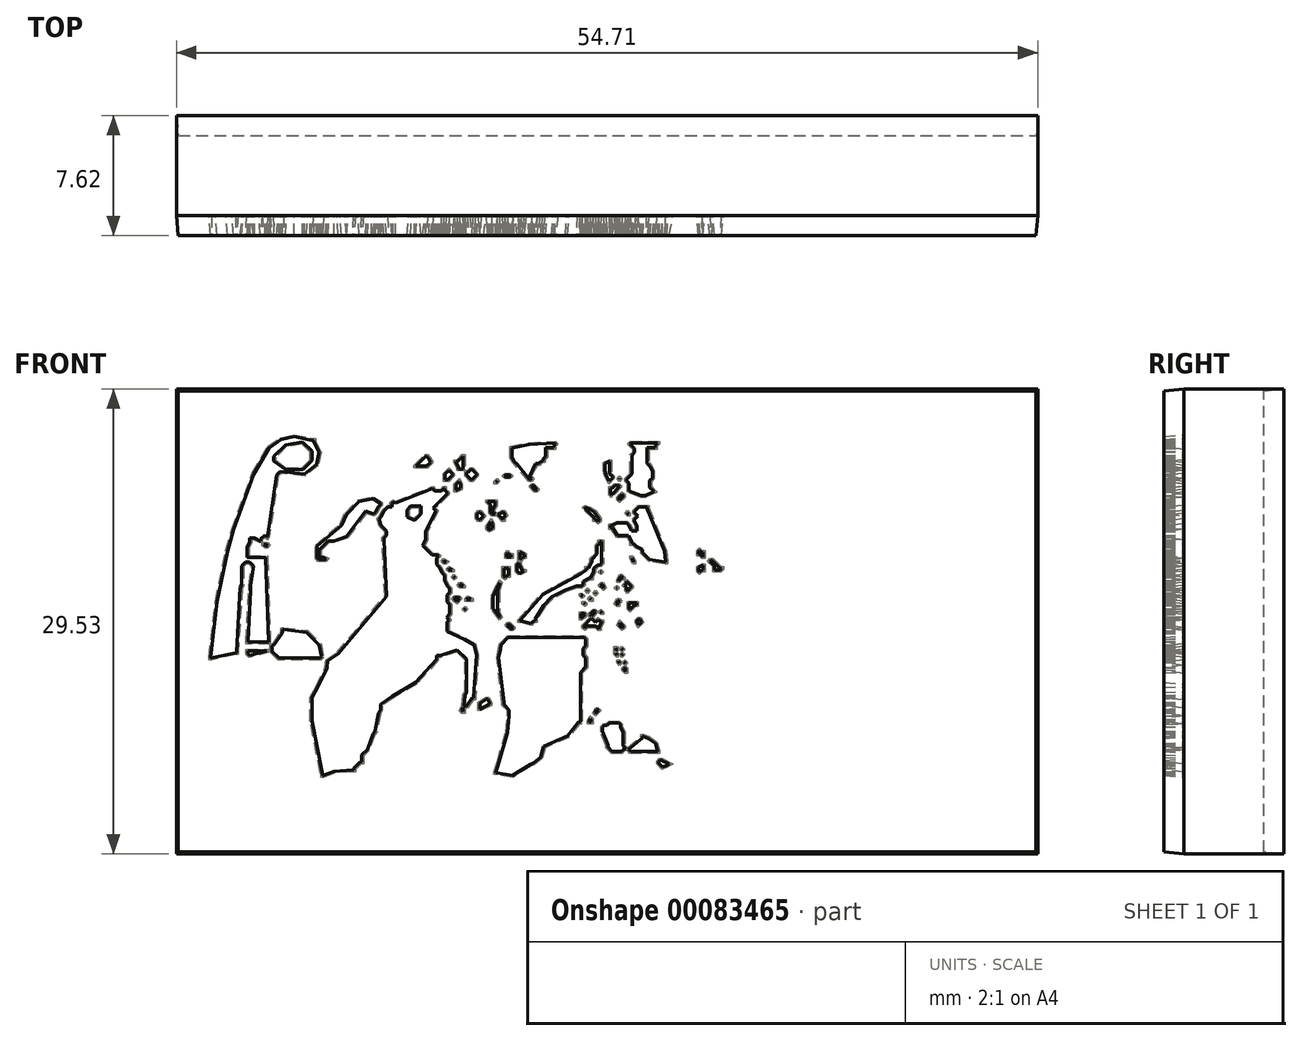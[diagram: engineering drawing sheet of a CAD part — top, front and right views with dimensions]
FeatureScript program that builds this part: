
annotation { "Feature Type Name" : "Feature", "Feature Type Description" : "" }
export const myFeature = defineFeature(function(context is Context, id is Id, definition is map)
    precondition{}
    {
        {
            var Q0;
            Q0=qCreatedBy(makeId("Front.planeOp"),FACE);
            var sketch = newSketch(context, id + "F0", { "sketchPlane" : qUnion([Q0])});
            skLineSegment(sketch, "E0", {"start": v(8.64, 12.87) * mm, "end": v(8.47, 12.87) * mm});
            skLineSegment(sketch, "E1", {"start": v(8.8, 12.87) * mm, "end": v(8.64, 12.87) * mm});
            skLineSegment(sketch, "E2", {"start": v(8.97, 12.87) * mm, "end": v(8.8, 12.87) * mm});
            skLineSegment(sketch, "E3", {"start": v(11, 12.87) * mm, "end": v(10.84, 13.04) * mm});
            skLineSegment(sketch, "E4", {"start": v(10.84, 13.04) * mm, "end": v(9.14, 13.04) * mm});
            skLineSegment(sketch, "E5", {"start": v(9.14, 13.04) * mm, "end": v(8.97, 12.87) * mm});
            skLineSegment(sketch, "E6", {"start": v(11.18, 12.87) * mm, "end": v(11, 12.87) * mm});
            skLineSegment(sketch, "E7", {"start": v(12.53, 12.87) * mm, "end": v(12.36, 12.87) * mm});
            skLineSegment(sketch, "E8", {"start": v(12.7, 12.87) * mm, "end": v(12.53, 12.87) * mm});
            skLineSegment(sketch, "E9", {"start": v(20.32, 12.87) * mm, "end": v(20.15, 12.87) * mm});
            skLineSegment(sketch, "E10", {"start": v(20.49, 12.87) * mm, "end": v(20.32, 12.87) * mm});
            skLineSegment(sketch, "E11", {"start": v(21.5, 12.87) * mm, "end": v(21.34, 13.04) * mm});
            skLineSegment(sketch, "E12", {"start": v(21.34, 13.04) * mm, "end": v(20.83, 13.04) * mm});
            skLineSegment(sketch, "E13", {"start": v(20.83, 13.04) * mm, "end": v(20.49, 12.87) * mm});
            skLineSegment(sketch, "E14", {"start": v(21.67, 12.87) * mm, "end": v(21.5, 12.87) * mm});
            skLineSegment(sketch, "E15", {"start": v(7.11, 12.7) * mm, "end": v(6.94, 12.7) * mm});
            skLineSegment(sketch, "E16", {"start": v(7.28, 12.7) * mm, "end": v(7.11, 12.7) * mm});
            skLineSegment(sketch, "E17", {"start": v(7.45, 12.7) * mm, "end": v(7.28, 12.7) * mm});
            skLineSegment(sketch, "E18", {"start": v(7.79, 12.7) * mm, "end": v(7.62, 12.87) * mm});
            skLineSegment(sketch, "E19", {"start": v(7.62, 12.87) * mm, "end": v(7.45, 12.7) * mm});
            skLineSegment(sketch, "E20", {"start": v(8.13, 12.7) * mm, "end": v(7.79, 12.7) * mm});
            skLineSegment(sketch, "E21", {"start": v(8.3, 12.7) * mm, "end": v(8.13, 12.7) * mm});
            skLineSegment(sketch, "E22", {"start": v(8.3, 12.7) * mm, "end": v(8.47, 12.87) * mm});
            skLineSegment(sketch, "E23", {"start": v(8.64, 12.7) * mm, "end": v(8.64, 12.87) * mm});
            skLineSegment(sketch, "E24", {"start": v(8.97, 12.7) * mm, "end": v(8.97, 12.87) * mm});
            skLineSegment(sketch, "E25", {"start": v(11, 12.7) * mm, "end": v(11, 12.87) * mm});
            skLineSegment(sketch, "E26", {"start": v(11.51, 12.7) * mm, "end": v(11.18, 12.87) * mm});
            skLineSegment(sketch, "E27", {"start": v(11.68, 12.7) * mm, "end": v(11.51, 12.7) * mm});
            skLineSegment(sketch, "E28", {"start": v(11.68, 12.7) * mm, "end": v(11.85, 12.87) * mm});
            skLineSegment(sketch, "E29", {"start": v(11.85, 12.87) * mm, "end": v(12.36, 12.87) * mm});
            skLineSegment(sketch, "E30", {"start": v(12.53, 12.7) * mm, "end": v(12.53, 12.87) * mm});
            skLineSegment(sketch, "E31", {"start": v(12.7, 12.87) * mm, "end": v(13.89, 12.7) * mm});
            skLineSegment(sketch, "E32", {"start": v(13.89, 12.7) * mm, "end": v(15.58, 12.79) * mm});
            skLineSegment(sketch, "E33", {"start": v(15.58, 12.79) * mm, "end": v(20.15, 12.87) * mm});
            skLineSegment(sketch, "E34", {"start": v(20.32, 12.7) * mm, "end": v(20.32, 12.87) * mm});
            skLineSegment(sketch, "E35", {"start": v(21.5, 12.7) * mm, "end": v(21.5, 12.87) * mm});
            skLineSegment(sketch, "E36", {"start": v(-18.8, 12.53) * mm, "end": v(-18.97, 12.53) * mm});
            skLineSegment(sketch, "E37", {"start": v(-18.63, 12.53) * mm, "end": v(-18.8, 12.53) * mm});
            skLineSegment(sketch, "E38", {"start": v(-0.5, 12.53) * mm, "end": v(-0.68, 12.7) * mm});
            skLineSegment(sketch, "E39", {"start": v(-0.68, 12.7) * mm, "end": v(-1.02, 12.53) * mm});
            skLineSegment(sketch, "E40", {"start": v(7.11, 12.53) * mm, "end": v(7.11, 12.7) * mm});
            skLineSegment(sketch, "E41", {"start": v(7.62, 12.53) * mm, "end": v(7.45, 12.7) * mm});
            skLineSegment(sketch, "E42", {"start": v(7.62, 12.53) * mm, "end": v(7.79, 12.7) * mm});
            skLineSegment(sketch, "E43", {"start": v(8.3, 12.53) * mm, "end": v(8.3, 12.7) * mm});
            skLineSegment(sketch, "E44", {"start": v(8.47, 12.53) * mm, "end": v(8.3, 12.53) * mm});
            skLineSegment(sketch, "E45", {"start": v(8.64, 12.53) * mm, "end": v(8.47, 12.53) * mm});
            skLineSegment(sketch, "E46", {"start": v(8.64, 12.53) * mm, "end": v(8.64, 12.7) * mm});
            skLineSegment(sketch, "E47", {"start": v(9.14, 12.53) * mm, "end": v(8.97, 12.7) * mm});
            skLineSegment(sketch, "E48", {"start": v(9.31, 12.53) * mm, "end": v(9.14, 12.53) * mm});
            skLineSegment(sketch, "E49", {"start": v(21.5, 12.53) * mm, "end": v(21.34, 12.53) * mm});
            skLineSegment(sketch, "E50", {"start": v(21.5, 12.53) * mm, "end": v(21.5, 12.7) * mm});
            skLineSegment(sketch, "E51", {"start": v(-18.8, 12.36) * mm, "end": v(-18.8, 12.53) * mm});
            skLineSegment(sketch, "E52", {"start": v(-0.85, 12.36) * mm, "end": v(-1.02, 12.53) * mm});
            skLineSegment(sketch, "E53", {"start": v(-0.68, 12.36) * mm, "end": v(-0.85, 12.36) * mm});
            skLineSegment(sketch, "E54", {"start": v(-0.68, 12.36) * mm, "end": v(-0.5, 12.53) * mm});
            skLineSegment(sketch, "E55", {"start": v(0.85, 12.36) * mm, "end": v(0.68, 12.53) * mm});
            skLineSegment(sketch, "E56", {"start": v(0.68, 12.53) * mm, "end": v(-0.5, 12.53) * mm});
            skLineSegment(sketch, "E57", {"start": v(3.05, 12.36) * mm, "end": v(2.88, 12.36) * mm});
            skLineSegment(sketch, "E58", {"start": v(3.22, 12.36) * mm, "end": v(3.05, 12.36) * mm});
            skLineSegment(sketch, "E59", {"start": v(3.22, 12.36) * mm, "end": v(6.94, 12.7) * mm});
            skLineSegment(sketch, "E60", {"start": v(6.94, 12.36) * mm, "end": v(7.11, 12.53) * mm});
            skLineSegment(sketch, "E61", {"start": v(7.28, 12.36) * mm, "end": v(7.11, 12.53) * mm});
            skLineSegment(sketch, "E62", {"start": v(7.28, 12.36) * mm, "end": v(7.62, 12.53) * mm});
            skLineSegment(sketch, "E63", {"start": v(8.64, 12.36) * mm, "end": v(8.64, 12.53) * mm});
            skLineSegment(sketch, "E64", {"start": v(9.14, 12.36) * mm, "end": v(9.14, 12.53) * mm});
            skLineSegment(sketch, "E65", {"start": v(11.35, 12.36) * mm, "end": v(11.51, 12.7) * mm});
            skLineSegment(sketch, "E66", {"start": v(-8.47, 12.2) * mm, "end": v(-8.64, 12.36) * mm});
            skLineSegment(sketch, "E67", {"start": v(-8.64, 12.36) * mm, "end": v(-10.5, 12.36) * mm});
            skLineSegment(sketch, "E68", {"start": v(-10.5, 12.36) * mm, "end": v(-10.67, 12.2) * mm});
            skLineSegment(sketch, "E69", {"start": v(-10.67, 12.2) * mm, "end": v(-15.92, 12.2) * mm});
            skLineSegment(sketch, "E70", {"start": v(-15.92, 12.2) * mm, "end": v(-16.77, 12.45) * mm});
            skLineSegment(sketch, "E71", {"start": v(-16.77, 12.45) * mm, "end": v(-18.63, 12.53) * mm});
            skLineSegment(sketch, "E72", {"start": v(-8.3, 12.2) * mm, "end": v(-8.47, 12.2) * mm});
            skLineSegment(sketch, "E73", {"start": v(-8.13, 12.2) * mm, "end": v(-8.3, 12.2) * mm});
            skLineSegment(sketch, "E74", {"start": v(-7.96, 12.2) * mm, "end": v(-8.13, 12.2) * mm});
            skLineSegment(sketch, "E75", {"start": v(-7.45, 12.2) * mm, "end": v(-7.96, 12.2) * mm});
            skLineSegment(sketch, "E76", {"start": v(-7.28, 12.2) * mm, "end": v(-7.45, 12.2) * mm});
            skLineSegment(sketch, "E77", {"start": v(-7.11, 12.2) * mm, "end": v(-7.28, 12.2) * mm});
            skLineSegment(sketch, "E78", {"start": v(-3.22, 12.2) * mm, "end": v(-3.39, 12.2) * mm});
            skLineSegment(sketch, "E79", {"start": v(-3.22, 12.2) * mm, "end": v(-1.02, 12.53) * mm});
            skLineSegment(sketch, "E80", {"start": v(-0.85, 12.2) * mm, "end": v(-0.85, 12.36) * mm});
            skLineSegment(sketch, "E81", {"start": v(0.85, 12.2) * mm, "end": v(0.85, 12.36) * mm});
            skLineSegment(sketch, "E82", {"start": v(1.02, 12.2) * mm, "end": v(0.85, 12.2) * mm});
            skLineSegment(sketch, "E83", {"start": v(1.02, 12.2) * mm, "end": v(1.19, 12.36) * mm});
            skLineSegment(sketch, "E84", {"start": v(1.19, 12.36) * mm, "end": v(2.88, 12.36) * mm});
            skLineSegment(sketch, "E85", {"start": v(3.05, 12.2) * mm, "end": v(3.05, 12.36) * mm});
            skLineSegment(sketch, "E86", {"start": v(6.77, 12.2) * mm, "end": v(6.94, 12.36) * mm});
            skLineSegment(sketch, "E87", {"start": v(7.11, 12.2) * mm, "end": v(6.94, 12.36) * mm});
            skLineSegment(sketch, "E88", {"start": v(7.11, 12.2) * mm, "end": v(7.28, 12.36) * mm});
            skLineSegment(sketch, "E89", {"start": v(8.13, 12.2) * mm, "end": v(8.3, 12.53) * mm});
            skLineSegment(sketch, "E90", {"start": v(9.65, 12.2) * mm, "end": v(9.82, 12.36) * mm});
            skLineSegment(sketch, "E91", {"start": v(9.82, 12.36) * mm, "end": v(9.65, 12.53) * mm});
            skLineSegment(sketch, "E92", {"start": v(9.65, 12.53) * mm, "end": v(9.31, 12.53) * mm});
            skLineSegment(sketch, "E93", {"start": v(11.18, 12.2) * mm, "end": v(11, 12.36) * mm});
            skLineSegment(sketch, "E94", {"start": v(11, 12.36) * mm, "end": v(11, 12.7) * mm});
            skLineSegment(sketch, "E95", {"start": v(11.35, 12.2) * mm, "end": v(11.18, 12.2) * mm});
            skLineSegment(sketch, "E96", {"start": v(11.35, 12.2) * mm, "end": v(11.35, 12.36) * mm});
            skLineSegment(sketch, "E97", {"start": v(12.02, 12.2) * mm, "end": v(12.02, 12.36) * mm});
            skLineSegment(sketch, "E98", {"start": v(12.02, 12.36) * mm, "end": v(11.68, 12.7) * mm});
            skLineSegment(sketch, "E99", {"start": v(-8.64, 12.02) * mm, "end": v(-8.47, 12.2) * mm});
            skLineSegment(sketch, "E100", {"start": v(-8.13, 12.02) * mm, "end": v(-8.13, 12.2) * mm});
            skLineSegment(sketch, "E101", {"start": v(-7.28, 12.02) * mm, "end": v(-7.28, 12.2) * mm});
            skLineSegment(sketch, "E102", {"start": v(-6.94, 12.02) * mm, "end": v(-7.11, 12.2) * mm});
            skLineSegment(sketch, "E103", {"start": v(-6.77, 12.02) * mm, "end": v(-6.94, 12.02) * mm});
            skLineSegment(sketch, "E104", {"start": v(-6.6, 12.02) * mm, "end": v(-6.77, 12.02) * mm});
            skLineSegment(sketch, "E105", {"start": v(-6.43, 12.02) * mm, "end": v(-6.6, 12.02) * mm});
            skLineSegment(sketch, "E106", {"start": v(-6.43, 12.02) * mm, "end": v(-5.26, 12.26) * mm});
            skLineSegment(sketch, "E107", {"start": v(-5.26, 12.26) * mm, "end": v(-3.56, 12.36) * mm});
            skLineSegment(sketch, "E108", {"start": v(-3.56, 12.36) * mm, "end": v(-3.39, 12.2) * mm});
            skLineSegment(sketch, "E109", {"start": v(-3.56, 12.02) * mm, "end": v(-3.39, 12.2) * mm});
            skLineSegment(sketch, "E110", {"start": v(-3.22, 12.02) * mm, "end": v(-3.22, 12.2) * mm});
            skLineSegment(sketch, "E111", {"start": v(2.88, 12.02) * mm, "end": v(3.05, 12.2) * mm});
            skLineSegment(sketch, "E112", {"start": v(3.22, 12.02) * mm, "end": v(3.05, 12.2) * mm});
            skLineSegment(sketch, "E113", {"start": v(6.77, 12.02) * mm, "end": v(6.77, 12.2) * mm});
            skLineSegment(sketch, "E114", {"start": v(6.94, 12.02) * mm, "end": v(6.77, 12.02) * mm});
            skLineSegment(sketch, "E115", {"start": v(6.94, 12.02) * mm, "end": v(7.11, 12.2) * mm});
            skLineSegment(sketch, "E116", {"start": v(8.13, 12.02) * mm, "end": v(7.96, 12.02) * mm});
            skLineSegment(sketch, "E117", {"start": v(8.13, 12.02) * mm, "end": v(8.13, 12.2) * mm});
            skLineSegment(sketch, "E118", {"start": v(8.64, 12.02) * mm, "end": v(8.64, 12.36) * mm});
            skLineSegment(sketch, "E119", {"start": v(9.14, 12.02) * mm, "end": v(9.14, 12.36) * mm});
            skLineSegment(sketch, "E120", {"start": v(9.65, 12.02) * mm, "end": v(9.48, 12.02) * mm});
            skLineSegment(sketch, "E121", {"start": v(9.65, 12.02) * mm, "end": v(9.65, 12.2) * mm});
            skLineSegment(sketch, "E122", {"start": v(9.82, 12.02) * mm, "end": v(9.65, 12.02) * mm});
            skLineSegment(sketch, "E123", {"start": v(11.35, 12.2) * mm, "end": v(11.51, 12.02) * mm});
            skLineSegment(sketch, "E124", {"start": v(11.51, 12.02) * mm, "end": v(11.85, 12.02) * mm});
            skLineSegment(sketch, "E125", {"start": v(11.85, 12.02) * mm, "end": v(12.02, 12.2) * mm});
            skLineSegment(sketch, "E126", {"start": v(-8.8, 11.85) * mm, "end": v(-8.64, 12.02) * mm});
            skLineSegment(sketch, "E127", {"start": v(-8.47, 11.85) * mm, "end": v(-8.64, 12.02) * mm});
            skLineSegment(sketch, "E128", {"start": v(-8.47, 11.85) * mm, "end": v(-8.13, 12.02) * mm});
            skLineSegment(sketch, "E129", {"start": v(-7.28, 12.02) * mm, "end": v(-7.11, 11.85) * mm});
            skLineSegment(sketch, "E130", {"start": v(-7.11, 11.85) * mm, "end": v(-6.94, 12.02) * mm});
            skLineSegment(sketch, "E131", {"start": v(-6.77, 11.85) * mm, "end": v(-6.77, 12.02) * mm});
            skLineSegment(sketch, "E132", {"start": v(-6.43, 11.85) * mm, "end": v(-6.43, 12.02) * mm});
            skLineSegment(sketch, "E133", {"start": v(-3.73, 11.85) * mm, "end": v(-3.9, 11.85) * mm});
            skLineSegment(sketch, "E134", {"start": v(-3.56, 11.85) * mm, "end": v(-3.73, 11.85) * mm});
            skLineSegment(sketch, "E135", {"start": v(-3.56, 11.85) * mm, "end": v(-3.56, 12.02) * mm});
            skLineSegment(sketch, "E136", {"start": v(-3.22, 11.85) * mm, "end": v(-3.22, 12.02) * mm});
            skLineSegment(sketch, "E137", {"start": v(-3.05, 11.85) * mm, "end": v(-3.22, 11.85) * mm});
            skLineSegment(sketch, "E138", {"start": v(2.7, 11.85) * mm, "end": v(2.54, 11.85) * mm});
            skLineSegment(sketch, "E139", {"start": v(2.88, 11.85) * mm, "end": v(2.7, 11.85) * mm});
            skLineSegment(sketch, "E140", {"start": v(2.88, 11.85) * mm, "end": v(2.88, 12.02) * mm});
            skLineSegment(sketch, "E141", {"start": v(3.22, 11.85) * mm, "end": v(3.22, 12.02) * mm});
            skLineSegment(sketch, "E142", {"start": v(3.39, 11.85) * mm, "end": v(3.22, 11.85) * mm});
            skLineSegment(sketch, "E143", {"start": v(8.64, 11.85) * mm, "end": v(8.64, 12.02) * mm});
            skLineSegment(sketch, "E144", {"start": v(8.8, 11.85) * mm, "end": v(8.64, 11.85) * mm});
            skLineSegment(sketch, "E145", {"start": v(8.97, 11.85) * mm, "end": v(8.8, 11.85) * mm});
            skLineSegment(sketch, "E146", {"start": v(9.14, 11.85) * mm, "end": v(8.97, 11.85) * mm});
            skLineSegment(sketch, "E147", {"start": v(9.14, 11.85) * mm, "end": v(9.14, 12.02) * mm});
            skLineSegment(sketch, "E148", {"start": v(9.31, 11.85) * mm, "end": v(9.14, 11.85) * mm});
            skLineSegment(sketch, "E149", {"start": v(9.31, 11.85) * mm, "end": v(9.48, 12.02) * mm});
            skLineSegment(sketch, "E150", {"start": v(-8.97, 11.68) * mm, "end": v(-8.8, 11.85) * mm});
            skLineSegment(sketch, "E151", {"start": v(-8.64, 11.68) * mm, "end": v(-8.8, 11.85) * mm});
            skLineSegment(sketch, "E152", {"start": v(-8.64, 11.68) * mm, "end": v(-8.47, 11.85) * mm});
            skLineSegment(sketch, "E153", {"start": v(-4.06, 11.68) * mm, "end": v(-4.06, 11.85) * mm});
            skLineSegment(sketch, "E154", {"start": v(-4.06, 11.85) * mm, "end": v(-3.9, 11.85) * mm});
            skLineSegment(sketch, "E155", {"start": v(-3.56, 11.68) * mm, "end": v(-3.56, 11.85) * mm});
            skLineSegment(sketch, "E156", {"start": v(-3.22, 11.68) * mm, "end": v(-3.22, 11.85) * mm});
            skLineSegment(sketch, "E157", {"start": v(-2.7, 11.68) * mm, "end": v(-2.7, 11.85) * mm});
            skLineSegment(sketch, "E158", {"start": v(-2.7, 11.85) * mm, "end": v(-2.88, 12.02) * mm});
            skLineSegment(sketch, "E159", {"start": v(-2.88, 12.02) * mm, "end": v(-3.05, 11.85) * mm});
            skLineSegment(sketch, "E160", {"start": v(2.37, 11.68) * mm, "end": v(2.37, 11.85) * mm});
            skLineSegment(sketch, "E161", {"start": v(2.37, 11.85) * mm, "end": v(2.54, 11.85) * mm});
            skLineSegment(sketch, "E162", {"start": v(2.88, 11.68) * mm, "end": v(2.88, 11.85) * mm});
            skLineSegment(sketch, "E163", {"start": v(3.22, 11.68) * mm, "end": v(3.22, 11.85) * mm});
            skLineSegment(sketch, "E164", {"start": v(3.73, 11.68) * mm, "end": v(3.73, 11.85) * mm});
            skLineSegment(sketch, "E165", {"start": v(3.73, 11.85) * mm, "end": v(3.56, 12.02) * mm});
            skLineSegment(sketch, "E166", {"start": v(3.56, 12.02) * mm, "end": v(3.39, 11.85) * mm});
            skLineSegment(sketch, "E167", {"start": v(8.47, 11.68) * mm, "end": v(8.13, 12.02) * mm});
            skLineSegment(sketch, "E168", {"start": v(8.47, 11.68) * mm, "end": v(8.64, 11.85) * mm});
            skLineSegment(sketch, "E169", {"start": v(9.14, 11.68) * mm, "end": v(9.14, 11.85) * mm});
            skLineSegment(sketch, "E170", {"start": v(22.52, 11.68) * mm, "end": v(21.5, 12.53) * mm});
            skLineSegment(sketch, "E171", {"start": v(-11.68, 11.51) * mm, "end": v(-11.51, 11.68) * mm});
            skLineSegment(sketch, "E172", {"start": v(-11.35, 11.51) * mm, "end": v(-11.51, 11.68) * mm});
            skLineSegment(sketch, "E173", {"start": v(-9.31, 11.51) * mm, "end": v(-9.48, 11.51) * mm});
            skLineSegment(sketch, "E174", {"start": v(-9.14, 11.51) * mm, "end": v(-9.31, 11.51) * mm});
            skLineSegment(sketch, "E175", {"start": v(-9.14, 11.51) * mm, "end": v(-8.97, 11.68) * mm});
            skLineSegment(sketch, "E176", {"start": v(-8.8, 11.51) * mm, "end": v(-8.97, 11.68) * mm});
            skLineSegment(sketch, "E177", {"start": v(-8.8, 11.51) * mm, "end": v(-8.64, 11.68) * mm});
            skLineSegment(sketch, "E178", {"start": v(-4.06, 11.51) * mm, "end": v(-4.06, 11.68) * mm});
            skLineSegment(sketch, "E179", {"start": v(-3.22, 11.51) * mm, "end": v(-3.22, 11.68) * mm});
            skLineSegment(sketch, "E180", {"start": v(-1.19, 11.51) * mm, "end": v(-0.85, 12.2) * mm});
            skLineSegment(sketch, "E181", {"start": v(1.19, 11.51) * mm, "end": v(1.02, 11.51) * mm});
            skLineSegment(sketch, "E182", {"start": v(1.19, 11.51) * mm, "end": v(1.35, 11.68) * mm});
            skLineSegment(sketch, "E183", {"start": v(1.35, 11.68) * mm, "end": v(1.35, 11.85) * mm});
            skLineSegment(sketch, "E184", {"start": v(1.35, 11.85) * mm, "end": v(1.02, 12.2) * mm});
            skLineSegment(sketch, "E185", {"start": v(2.37, 11.51) * mm, "end": v(2.37, 11.68) * mm});
            skLineSegment(sketch, "E186", {"start": v(2.54, 11.51) * mm, "end": v(2.37, 11.51) * mm});
            skLineSegment(sketch, "E187", {"start": v(2.88, 11.51) * mm, "end": v(2.88, 11.68) * mm});
            skLineSegment(sketch, "E188", {"start": v(3.73, 11.51) * mm, "end": v(3.56, 11.51) * mm});
            skLineSegment(sketch, "E189", {"start": v(3.73, 11.51) * mm, "end": v(3.73, 11.68) * mm});
            skLineSegment(sketch, "E190", {"start": v(6.43, 11.51) * mm, "end": v(6.77, 12.02) * mm});
            skLineSegment(sketch, "E191", {"start": v(8.64, 11.51) * mm, "end": v(8.47, 11.68) * mm});
            skLineSegment(sketch, "E192", {"start": v(8.8, 11.51) * mm, "end": v(8.64, 11.51) * mm});
            skLineSegment(sketch, "E193", {"start": v(9.14, 11.51) * mm, "end": v(9.14, 11.68) * mm});
            skLineSegment(sketch, "E194", {"start": v(9.31, 11.51) * mm, "end": v(9.14, 11.51) * mm});
            skLineSegment(sketch, "E195", {"start": v(9.48, 11.51) * mm, "end": v(9.31, 11.51) * mm});
            skLineSegment(sketch, "E196", {"start": v(9.65, 11.51) * mm, "end": v(9.48, 11.51) * mm});
            skLineSegment(sketch, "E197", {"start": v(9.82, 11.51) * mm, "end": v(9.65, 11.51) * mm});
            skLineSegment(sketch, "E198", {"start": v(9.82, 11.51) * mm, "end": v(10, 11.51) * mm});
            skLineSegment(sketch, "E199", {"start": v(10, 11.51) * mm, "end": v(10.16, 11.68) * mm});
            skLineSegment(sketch, "E200", {"start": v(10.16, 11.68) * mm, "end": v(9.82, 12.02) * mm});
            skLineSegment(sketch, "E201", {"start": v(22.52, 11.51) * mm, "end": v(22.52, 11.68) * mm});
            skLineSegment(sketch, "E202", {"start": v(22.7, 11.51) * mm, "end": v(22.52, 11.51) * mm});
            skLineSegment(sketch, "E203", {"start": v(-11.51, 11.35) * mm, "end": v(-11.68, 11.51) * mm});
            skLineSegment(sketch, "E204", {"start": v(-11.51, 11.35) * mm, "end": v(-11.35, 11.51) * mm});
            skLineSegment(sketch, "E205", {"start": v(-9.31, 11.35) * mm, "end": v(-9.31, 11.51) * mm});
            skLineSegment(sketch, "E206", {"start": v(-8.97, 11.35) * mm, "end": v(-9.14, 11.51) * mm});
            skLineSegment(sketch, "E207", {"start": v(-8.8, 11.35) * mm, "end": v(-8.97, 11.35) * mm});
            skLineSegment(sketch, "E208", {"start": v(-8.8, 11.35) * mm, "end": v(-8.8, 11.51) * mm});
            skLineSegment(sketch, "E209", {"start": v(-6.43, 11.35) * mm, "end": v(-6.43, 11.85) * mm});
            skLineSegment(sketch, "E210", {"start": v(-4.06, 11.35) * mm, "end": v(-4.06, 11.51) * mm});
            skLineSegment(sketch, "E211", {"start": v(-3.9, 11.35) * mm, "end": v(-4.06, 11.35) * mm});
            skLineSegment(sketch, "E212", {"start": v(-3.56, 11.35) * mm, "end": v(-3.56, 11.68) * mm});
            skLineSegment(sketch, "E213", {"start": v(-3.22, 11.35) * mm, "end": v(-3.22, 11.51) * mm});
            skLineSegment(sketch, "E214", {"start": v(-3.05, 11.35) * mm, "end": v(-3.22, 11.35) * mm});
            skLineSegment(sketch, "E215", {"start": v(-3.05, 11.35) * mm, "end": v(-2.7, 11.68) * mm});
            skLineSegment(sketch, "E216", {"start": v(-1.19, 11.35) * mm, "end": v(-1.19, 11.51) * mm});
            skLineSegment(sketch, "E217", {"start": v(-1.02, 11.35) * mm, "end": v(-1.19, 11.35) * mm});
            skLineSegment(sketch, "E218", {"start": v(-1.02, 11.35) * mm, "end": v(0.85, 12.2) * mm});
            skLineSegment(sketch, "E219", {"start": v(0.17, 11.35) * mm, "end": v(0.34, 11.51) * mm});
            skLineSegment(sketch, "E220", {"start": v(0.34, 11.51) * mm, "end": v(1.02, 11.51) * mm});
            skLineSegment(sketch, "E221", {"start": v(1.19, 11.35) * mm, "end": v(1.19, 11.51) * mm});
            skLineSegment(sketch, "E222", {"start": v(2.37, 11.35) * mm, "end": v(2.37, 11.51) * mm});
            skLineSegment(sketch, "E223", {"start": v(2.7, 11.35) * mm, "end": v(2.54, 11.51) * mm});
            skLineSegment(sketch, "E224", {"start": v(2.88, 11.35) * mm, "end": v(2.7, 11.35) * mm});
            skLineSegment(sketch, "E225", {"start": v(2.88, 11.35) * mm, "end": v(2.88, 11.51) * mm});
            skLineSegment(sketch, "E226", {"start": v(3.39, 11.35) * mm, "end": v(3.22, 11.68) * mm});
            skLineSegment(sketch, "E227", {"start": v(3.39, 11.35) * mm, "end": v(3.56, 11.51) * mm});
            skLineSegment(sketch, "E228", {"start": v(6.43, 11.35) * mm, "end": v(6.27, 11.35) * mm});
            skLineSegment(sketch, "E229", {"start": v(6.43, 11.35) * mm, "end": v(6.43, 11.51) * mm});
            skLineSegment(sketch, "E230", {"start": v(7.96, 11.35) * mm, "end": v(7.62, 11.68) * mm});
            skLineSegment(sketch, "E231", {"start": v(7.62, 11.68) * mm, "end": v(7.96, 12.02) * mm});
            skLineSegment(sketch, "E232", {"start": v(8.13, 11.35) * mm, "end": v(7.96, 11.35) * mm});
            skLineSegment(sketch, "E233", {"start": v(8.13, 11.35) * mm, "end": v(8.47, 11.68) * mm});
            skLineSegment(sketch, "E234", {"start": v(8.64, 11.35) * mm, "end": v(8.64, 11.51) * mm});
            skLineSegment(sketch, "E235", {"start": v(8.97, 11.35) * mm, "end": v(8.8, 11.51) * mm});
            skLineSegment(sketch, "E236", {"start": v(8.97, 11.35) * mm, "end": v(9.14, 11.51) * mm});
            skLineSegment(sketch, "E237", {"start": v(9.65, 11.35) * mm, "end": v(9.65, 11.51) * mm});
            skLineSegment(sketch, "E238", {"start": v(-10, 11.18) * mm, "end": v(-10.16, 11.18) * mm});
            skLineSegment(sketch, "E239", {"start": v(-9.82, 11.18) * mm, "end": v(-10, 11.18) * mm});
            skLineSegment(sketch, "E240", {"start": v(-9.82, 11.18) * mm, "end": v(-9.48, 11.51) * mm});
            skLineSegment(sketch, "E241", {"start": v(-9.31, 11.18) * mm, "end": v(-9.31, 11.35) * mm});
            skLineSegment(sketch, "E242", {"start": v(-9.14, 11.18) * mm, "end": v(-9.31, 11.18) * mm});
            skLineSegment(sketch, "E243", {"start": v(-9.14, 11.18) * mm, "end": v(-8.97, 11.35) * mm});
            skLineSegment(sketch, "E244", {"start": v(-8.8, 11.18) * mm, "end": v(-8.8, 11.35) * mm});
            skLineSegment(sketch, "E245", {"start": v(-6.6, 11.18) * mm, "end": v(-6.77, 11.35) * mm});
            skLineSegment(sketch, "E246", {"start": v(-6.77, 11.35) * mm, "end": v(-6.77, 11.85) * mm});
            skLineSegment(sketch, "E247", {"start": v(-6.6, 11.18) * mm, "end": v(-6.43, 11.35) * mm});
            skLineSegment(sketch, "E248", {"start": v(-4.23, 11.18) * mm, "end": v(-4.06, 11.35) * mm});
            skLineSegment(sketch, "E249", {"start": v(-3.73, 11.18) * mm, "end": v(-3.9, 11.35) * mm});
            skLineSegment(sketch, "E250", {"start": v(-3.73, 11.18) * mm, "end": v(-3.56, 11.35) * mm});
            skLineSegment(sketch, "E251", {"start": v(-3.39, 11.18) * mm, "end": v(-3.56, 11.35) * mm});
            skLineSegment(sketch, "E252", {"start": v(-3.39, 11.18) * mm, "end": v(-3.22, 11.35) * mm});
            skLineSegment(sketch, "E253", {"start": v(-1.19, 11.18) * mm, "end": v(-1.19, 11.35) * mm});
            skLineSegment(sketch, "E254", {"start": v(0, 11.18) * mm, "end": v(-0.17, 11.18) * mm});
            skLineSegment(sketch, "E255", {"start": v(0, 11.18) * mm, "end": v(0.17, 11.35) * mm});
            skLineSegment(sketch, "E256", {"start": v(1.19, 11.18) * mm, "end": v(1.19, 11.35) * mm});
            skLineSegment(sketch, "E257", {"start": v(3.05, 11.18) * mm, "end": v(2.88, 11.35) * mm});
            skLineSegment(sketch, "E258", {"start": v(3.39, 11.18) * mm, "end": v(3.39, 11.35) * mm});
            skLineSegment(sketch, "E259", {"start": v(6.43, 11.18) * mm, "end": v(6.43, 11.35) * mm});
            skLineSegment(sketch, "E260", {"start": v(7.96, 11.18) * mm, "end": v(7.96, 11.35) * mm});
            skLineSegment(sketch, "E261", {"start": v(-11.35, 11) * mm, "end": v(-11.51, 11.35) * mm});
            skLineSegment(sketch, "E262", {"start": v(-11.35, 11) * mm, "end": v(-11.18, 11.18) * mm});
            skLineSegment(sketch, "E263", {"start": v(-11.18, 11.18) * mm, "end": v(-11.35, 11.51) * mm});
            skLineSegment(sketch, "E264", {"start": v(-10.33, 11) * mm, "end": v(-10.33, 11.18) * mm});
            skLineSegment(sketch, "E265", {"start": v(-10.33, 11.18) * mm, "end": v(-10.16, 11.18) * mm});
            skLineSegment(sketch, "E266", {"start": v(-10, 11) * mm, "end": v(-10, 11.18) * mm});
            skLineSegment(sketch, "E267", {"start": v(-9.31, 11) * mm, "end": v(-9.31, 11.18) * mm});
            skLineSegment(sketch, "E268", {"start": v(-6.27, 11) * mm, "end": v(-6.43, 11.35) * mm});
            skLineSegment(sketch, "E269", {"start": v(-4.23, 11) * mm, "end": v(-4.4, 11) * mm});
            skLineSegment(sketch, "E270", {"start": v(-4.23, 11) * mm, "end": v(-4.23, 11.18) * mm});
            skLineSegment(sketch, "E271", {"start": v(-3.9, 11) * mm, "end": v(-3.73, 11.18) * mm});
            skLineSegment(sketch, "E272", {"start": v(-3.39, 11) * mm, "end": v(-3.39, 11.18) * mm});
            skLineSegment(sketch, "E273", {"start": v(-2.7, 11) * mm, "end": v(-3.05, 11.35) * mm});
            skLineSegment(sketch, "E274", {"start": v(-2.54, 11) * mm, "end": v(-2.7, 11) * mm});
            skLineSegment(sketch, "E275", {"start": v(-2.54, 11) * mm, "end": v(-2.37, 11.18) * mm});
            skLineSegment(sketch, "E276", {"start": v(-2.37, 11.18) * mm, "end": v(-2.37, 11.35) * mm});
            skLineSegment(sketch, "E277", {"start": v(-2.37, 11.35) * mm, "end": v(-2.7, 11.68) * mm});
            skLineSegment(sketch, "E278", {"start": v(-0.5, 11) * mm, "end": v(-0.68, 11) * mm});
            skLineSegment(sketch, "E279", {"start": v(-0.5, 11) * mm, "end": v(-0.17, 11.18) * mm});
            skLineSegment(sketch, "E280", {"start": v(0, 11) * mm, "end": v(0, 11.18) * mm});
            skLineSegment(sketch, "E281", {"start": v(0.34, 11) * mm, "end": v(0.17, 11.35) * mm});
            skLineSegment(sketch, "E282", {"start": v(1.19, 11) * mm, "end": v(1.02, 11) * mm});
            skLineSegment(sketch, "E283", {"start": v(1.19, 11) * mm, "end": v(1.19, 11.18) * mm});
            skLineSegment(sketch, "E284", {"start": v(2.88, 11) * mm, "end": v(2.7, 11) * mm});
            skLineSegment(sketch, "E285", {"start": v(2.88, 11) * mm, "end": v(3.05, 11.18) * mm});
            skLineSegment(sketch, "E286", {"start": v(3.22, 11) * mm, "end": v(3.05, 11.18) * mm});
            skLineSegment(sketch, "E287", {"start": v(3.22, 11) * mm, "end": v(3.39, 11.18) * mm});
            skLineSegment(sketch, "E288", {"start": v(3.56, 11) * mm, "end": v(3.39, 11.18) * mm});
            skLineSegment(sketch, "E289", {"start": v(3.56, 11) * mm, "end": v(3.9, 11.35) * mm});
            skLineSegment(sketch, "E290", {"start": v(3.9, 11.35) * mm, "end": v(3.73, 11.51) * mm});
            skLineSegment(sketch, "E291", {"start": v(6.1, 11) * mm, "end": v(6.27, 11.35) * mm});
            skLineSegment(sketch, "E292", {"start": v(7.96, 11) * mm, "end": v(7.96, 11.18) * mm});
            skLineSegment(sketch, "E293", {"start": v(8.64, 11) * mm, "end": v(8.64, 11.35) * mm});
            skLineSegment(sketch, "E294", {"start": v(9.14, 11) * mm, "end": v(8.97, 11.35) * mm});
            skLineSegment(sketch, "E295", {"start": v(9.82, 11) * mm, "end": v(9.65, 11.35) * mm});
            skLineSegment(sketch, "E296", {"start": v(13.38, 11) * mm, "end": v(13.38, 11.35) * mm});
            skLineSegment(sketch, "E297", {"start": v(13.38, 11.35) * mm, "end": v(13.04, 11.68) * mm});
            skLineSegment(sketch, "E298", {"start": v(13.04, 11.68) * mm, "end": v(12.36, 11.68) * mm});
            skLineSegment(sketch, "E299", {"start": v(12.36, 11.68) * mm, "end": v(12.02, 12.2) * mm});
            skLineSegment(sketch, "E300", {"start": v(21.34, 12.53) * mm, "end": v(21, 12.53) * mm});
            skLineSegment(sketch, "E301", {"start": v(21, 12.53) * mm, "end": v(20.62, 12.04) * mm});
            skLineSegment(sketch, "E302", {"start": v(20.62, 12.04) * mm, "end": v(20.49, 11.85) * mm});
            skLineSegment(sketch, "E303", {"start": v(20.49, 11.85) * mm, "end": v(20.66, 11.35) * mm});
            skLineSegment(sketch, "E304", {"start": v(20.66, 11.35) * mm, "end": v(21, 11) * mm});
            skLineSegment(sketch, "E305", {"start": v(21, 11) * mm, "end": v(21.84, 11) * mm});
            skLineSegment(sketch, "E306", {"start": v(21.84, 11) * mm, "end": v(22.34, 11.38) * mm});
            skLineSegment(sketch, "E307", {"start": v(22.34, 11.38) * mm, "end": v(22.52, 11.51) * mm});
            skLineSegment(sketch, "E308", {"start": v(-12.53, 10.84) * mm, "end": v(-11.85, 11.51) * mm});
            skLineSegment(sketch, "E309", {"start": v(-11.85, 11.51) * mm, "end": v(-11.68, 11.51) * mm});
            skLineSegment(sketch, "E310", {"start": v(-8.8, 10.84) * mm, "end": v(-8.8, 11.18) * mm});
            skLineSegment(sketch, "E311", {"start": v(-6.43, 10.84) * mm, "end": v(-6.6, 11.18) * mm});
            skLineSegment(sketch, "E312", {"start": v(-6.43, 10.84) * mm, "end": v(-6.27, 11) * mm});
            skLineSegment(sketch, "E313", {"start": v(-6.1, 10.84) * mm, "end": v(-6.27, 11) * mm});
            skLineSegment(sketch, "E314", {"start": v(-4.57, 10.84) * mm, "end": v(-4.74, 10.84) * mm});
            skLineSegment(sketch, "E315", {"start": v(-4.57, 10.84) * mm, "end": v(-4.4, 11) * mm});
            skLineSegment(sketch, "E316", {"start": v(-4.06, 10.84) * mm, "end": v(-4.23, 11) * mm});
            skLineSegment(sketch, "E317", {"start": v(-4.06, 10.84) * mm, "end": v(-3.9, 11) * mm});
            skLineSegment(sketch, "E318", {"start": v(-3.73, 10.84) * mm, "end": v(-3.9, 11) * mm});
            skLineSegment(sketch, "E319", {"start": v(-3.56, 10.84) * mm, "end": v(-3.73, 10.84) * mm});
            skLineSegment(sketch, "E320", {"start": v(-3.56, 10.84) * mm, "end": v(-3.39, 11) * mm});
            skLineSegment(sketch, "E321", {"start": v(-2.54, 10.84) * mm, "end": v(-2.54, 11) * mm});
            skLineSegment(sketch, "E322", {"start": v(-1.19, 10.84) * mm, "end": v(-1.19, 11.18) * mm});
            skLineSegment(sketch, "E323", {"start": v(-0.85, 10.84) * mm, "end": v(-0.68, 11) * mm});
            skLineSegment(sketch, "E324", {"start": v(-0.5, 10.84) * mm, "end": v(-0.5, 11) * mm});
            skLineSegment(sketch, "E325", {"start": v(0, 10.84) * mm, "end": v(0, 11) * mm});
            skLineSegment(sketch, "E326", {"start": v(0.17, 10.84) * mm, "end": v(0, 10.84) * mm});
            skLineSegment(sketch, "E327", {"start": v(0.34, 10.84) * mm, "end": v(0.17, 10.84) * mm});
            skLineSegment(sketch, "E328", {"start": v(0.34, 10.84) * mm, "end": v(0.34, 11) * mm});
            skLineSegment(sketch, "E329", {"start": v(0.5, 10.84) * mm, "end": v(0.34, 10.84) * mm});
            skLineSegment(sketch, "E330", {"start": v(0.5, 10.84) * mm, "end": v(1.02, 11) * mm});
            skLineSegment(sketch, "E331", {"start": v(1.19, 10.84) * mm, "end": v(1.19, 11) * mm});
            skLineSegment(sketch, "E332", {"start": v(2.54, 10.84) * mm, "end": v(2.37, 11) * mm});
            skLineSegment(sketch, "E333", {"start": v(2.37, 11) * mm, "end": v(2.37, 11.35) * mm});
            skLineSegment(sketch, "E334", {"start": v(2.54, 10.84) * mm, "end": v(2.7, 11) * mm});
            skLineSegment(sketch, "E335", {"start": v(2.88, 10.84) * mm, "end": v(2.88, 11) * mm});
            skLineSegment(sketch, "E336", {"start": v(6.27, 10.84) * mm, "end": v(6.1, 11) * mm});
            skLineSegment(sketch, "E337", {"start": v(6.27, 10.84) * mm, "end": v(6.43, 11.18) * mm});
            skLineSegment(sketch, "E338", {"start": v(8.13, 10.84) * mm, "end": v(7.96, 10.84) * mm});
            skLineSegment(sketch, "E339", {"start": v(7.96, 10.84) * mm, "end": v(7.96, 11) * mm});
            skLineSegment(sketch, "E340", {"start": v(8.47, 10.84) * mm, "end": v(8.13, 10.84) * mm});
            skLineSegment(sketch, "E341", {"start": v(8.64, 10.84) * mm, "end": v(8.47, 10.84) * mm});
            skLineSegment(sketch, "E342", {"start": v(8.64, 10.84) * mm, "end": v(8.64, 11) * mm});
            skLineSegment(sketch, "E343", {"start": v(9.14, 10.84) * mm, "end": v(9.14, 11) * mm});
            skLineSegment(sketch, "E344", {"start": v(9.31, 10.84) * mm, "end": v(9.14, 10.84) * mm});
            skLineSegment(sketch, "E345", {"start": v(9.65, 10.84) * mm, "end": v(9.31, 10.84) * mm});
            skLineSegment(sketch, "E346", {"start": v(9.82, 10.84) * mm, "end": v(9.65, 10.84) * mm});
            skLineSegment(sketch, "E347", {"start": v(9.82, 10.84) * mm, "end": v(9.82, 11) * mm});
            skLineSegment(sketch, "E348", {"start": v(10, 10.84) * mm, "end": v(9.82, 10.84) * mm});
            skLineSegment(sketch, "E349", {"start": v(13.38, 10.84) * mm, "end": v(13.2, 10.84) * mm});
            skLineSegment(sketch, "E350", {"start": v(13.38, 10.84) * mm, "end": v(13.38, 11) * mm});
            skLineSegment(sketch, "E351", {"start": v(14.56, 10.84) * mm, "end": v(14.22, 11.68) * mm});
            skLineSegment(sketch, "E352", {"start": v(14.22, 11.68) * mm, "end": v(13.56, 12.06) * mm});
            skLineSegment(sketch, "E353", {"start": v(13.56, 12.06) * mm, "end": v(13.36, 12.13) * mm});
            skLineSegment(sketch, "E354", {"start": v(13.36, 12.13) * mm, "end": v(12.87, 12.2) * mm});
            skLineSegment(sketch, "E355", {"start": v(12.87, 12.2) * mm, "end": v(12.53, 12.53) * mm});
            skLineSegment(sketch, "E356", {"start": v(12.53, 12.53) * mm, "end": v(12.53, 12.7) * mm});
            skLineSegment(sketch, "E357", {"start": v(-21.34, 11.18) * mm, "end": v(-20.84, 10.8) * mm});
            skLineSegment(sketch, "E358", {"start": v(-20.84, 10.8) * mm, "end": v(-20.66, 10.67) * mm});
            skLineSegment(sketch, "E359", {"start": v(-20.66, 10.67) * mm, "end": v(-19.64, 10.67) * mm});
            skLineSegment(sketch, "E360", {"start": v(-19.64, 10.67) * mm, "end": v(-19.13, 11.18) * mm});
            skLineSegment(sketch, "E361", {"start": v(-19.13, 11.18) * mm, "end": v(-19.13, 11.68) * mm});
            skLineSegment(sketch, "E362", {"start": v(-19.13, 11.68) * mm, "end": v(-19.64, 12.2) * mm});
            skLineSegment(sketch, "E363", {"start": v(-19.64, 12.2) * mm, "end": v(-20.66, 12.02) * mm});
            skLineSegment(sketch, "E364", {"start": v(-20.66, 12.02) * mm, "end": v(-21.34, 11.35) * mm});
            skLineSegment(sketch, "E365", {"start": v(-21.34, 11.35) * mm, "end": v(-21.34, 11.18) * mm});
            skLineSegment(sketch, "E366", {"start": v(-12.53, 10.67) * mm, "end": v(-12.53, 10.84) * mm});
            skLineSegment(sketch, "E367", {"start": v(-12.36, 10.67) * mm, "end": v(-12.53, 10.67) * mm});
            skLineSegment(sketch, "E368", {"start": v(-12.36, 10.67) * mm, "end": v(-11.68, 10.67) * mm});
            skLineSegment(sketch, "E369", {"start": v(-11.68, 10.67) * mm, "end": v(-11.35, 11) * mm});
            skLineSegment(sketch, "E370", {"start": v(-10.33, 10.67) * mm, "end": v(-10.33, 11) * mm});
            skLineSegment(sketch, "E371", {"start": v(-9.82, 10.67) * mm, "end": v(-10, 11) * mm});
            skLineSegment(sketch, "E372", {"start": v(-9.31, 10.67) * mm, "end": v(-9.31, 11) * mm});
            skLineSegment(sketch, "E373", {"start": v(-8.8, 10.67) * mm, "end": v(-8.97, 10.67) * mm});
            skLineSegment(sketch, "E374", {"start": v(-8.8, 10.67) * mm, "end": v(-8.8, 10.84) * mm});
            skLineSegment(sketch, "E375", {"start": v(-6.27, 10.67) * mm, "end": v(-6.43, 10.84) * mm});
            skLineSegment(sketch, "E376", {"start": v(-6.27, 10.67) * mm, "end": v(-6.1, 10.84) * mm});
            skLineSegment(sketch, "E377", {"start": v(-4.57, 10.67) * mm, "end": v(-4.57, 10.84) * mm});
            skLineSegment(sketch, "E378", {"start": v(-4.06, 10.67) * mm, "end": v(-4.06, 10.84) * mm});
            skLineSegment(sketch, "E379", {"start": v(-3.73, 10.67) * mm, "end": v(-3.73, 10.84) * mm});
            skLineSegment(sketch, "E380", {"start": v(-3.22, 10.67) * mm, "end": v(-3.39, 11) * mm});
            skLineSegment(sketch, "E381", {"start": v(-2.54, 10.67) * mm, "end": v(-2.54, 10.84) * mm});
            skLineSegment(sketch, "E382", {"start": v(-1.19, 10.67) * mm, "end": v(-1.19, 10.84) * mm});
            skLineSegment(sketch, "E383", {"start": v(-1.02, 10.67) * mm, "end": v(-1.19, 10.67) * mm});
            skLineSegment(sketch, "E384", {"start": v(-1.02, 10.67) * mm, "end": v(-0.85, 10.84) * mm});
            skLineSegment(sketch, "E385", {"start": v(-0.68, 10.67) * mm, "end": v(-0.85, 10.84) * mm});
            skLineSegment(sketch, "E386", {"start": v(-0.5, 10.67) * mm, "end": v(-0.68, 10.67) * mm});
            skLineSegment(sketch, "E387", {"start": v(-0.5, 10.67) * mm, "end": v(-0.5, 10.84) * mm});
            skLineSegment(sketch, "E388", {"start": v(0, 10.67) * mm, "end": v(0, 10.84) * mm});
            skLineSegment(sketch, "E389", {"start": v(2.88, 10.67) * mm, "end": v(2.88, 10.84) * mm});
            skLineSegment(sketch, "E390", {"start": v(3.39, 10.67) * mm, "end": v(3.22, 11) * mm});
            skLineSegment(sketch, "E391", {"start": v(3.39, 10.67) * mm, "end": v(3.56, 11) * mm});
            skLineSegment(sketch, "E392", {"start": v(5.93, 10.67) * mm, "end": v(6.1, 11) * mm});
            skLineSegment(sketch, "E393", {"start": v(8.64, 10.67) * mm, "end": v(8.64, 10.84) * mm});
            skLineSegment(sketch, "E394", {"start": v(9.82, 10.67) * mm, "end": v(9.82, 10.84) * mm});
            skLineSegment(sketch, "E395", {"start": v(10.16, 10.67) * mm, "end": v(10, 10.84) * mm});
            skLineSegment(sketch, "E396", {"start": v(10.33, 10.67) * mm, "end": v(10.16, 10.67) * mm});
            skLineSegment(sketch, "E397", {"start": v(13.04, 10.67) * mm, "end": v(13.2, 10.84) * mm});
            skLineSegment(sketch, "E398", {"start": v(13.38, 10.67) * mm, "end": v(13.38, 10.84) * mm});
            skLineSegment(sketch, "E399", {"start": v(-12.53, 10.5) * mm, "end": v(-12.53, 10.67) * mm});
            skLineSegment(sketch, "E400", {"start": v(-9.82, 10.5) * mm, "end": v(-9.82, 10.67) * mm});
            skLineSegment(sketch, "E401", {"start": v(-9.65, 10.5) * mm, "end": v(-9.82, 10.5) * mm});
            skLineSegment(sketch, "E402", {"start": v(-9.48, 10.5) * mm, "end": v(-9.65, 10.5) * mm});
            skLineSegment(sketch, "E403", {"start": v(-9.31, 10.5) * mm, "end": v(-9.48, 10.5) * mm});
            skLineSegment(sketch, "E404", {"start": v(-9.31, 10.5) * mm, "end": v(-9.31, 10.67) * mm});
            skLineSegment(sketch, "E405", {"start": v(-9.14, 10.5) * mm, "end": v(-9.31, 10.5) * mm});
            skLineSegment(sketch, "E406", {"start": v(-9.14, 10.5) * mm, "end": v(-8.97, 10.67) * mm});
            skLineSegment(sketch, "E407", {"start": v(-4.91, 10.5) * mm, "end": v(-4.74, 10.84) * mm});
            skLineSegment(sketch, "E408", {"start": v(-3.9, 10.5) * mm, "end": v(-4.06, 10.5) * mm});
            skLineSegment(sketch, "E409", {"start": v(-4.06, 10.5) * mm, "end": v(-4.06, 10.67) * mm});
            skLineSegment(sketch, "E410", {"start": v(-3.73, 10.5) * mm, "end": v(-3.9, 10.5) * mm});
            skLineSegment(sketch, "E411", {"start": v(-3.73, 10.5) * mm, "end": v(-3.73, 10.67) * mm});
            skLineSegment(sketch, "E412", {"start": v(-3.22, 10.5) * mm, "end": v(-3.22, 10.67) * mm});
            skLineSegment(sketch, "E413", {"start": v(-3.05, 10.5) * mm, "end": v(-3.22, 10.5) * mm});
            skLineSegment(sketch, "E414", {"start": v(-2.7, 10.5) * mm, "end": v(-3.05, 10.5) * mm});
            skLineSegment(sketch, "E415", {"start": v(-2.7, 10.5) * mm, "end": v(-2.54, 10.5) * mm});
            skLineSegment(sketch, "E416", {"start": v(-2.54, 10.5) * mm, "end": v(-2.54, 10.67) * mm});
            skLineSegment(sketch, "E417", {"start": v(-1.19, 10.5) * mm, "end": v(-1.19, 10.67) * mm});
            skLineSegment(sketch, "E418", {"start": v(-0.5, 10.5) * mm, "end": v(-0.5, 10.67) * mm});
            skLineSegment(sketch, "E419", {"start": v(2.7, 10.5) * mm, "end": v(2.54, 10.84) * mm});
            skLineSegment(sketch, "E420", {"start": v(2.7, 10.5) * mm, "end": v(2.88, 10.67) * mm});
            skLineSegment(sketch, "E421", {"start": v(2.88, 10.67) * mm, "end": v(3.05, 10.5) * mm});
            skLineSegment(sketch, "E422", {"start": v(3.05, 10.5) * mm, "end": v(3.39, 10.67) * mm});
            skLineSegment(sketch, "E423", {"start": v(5.76, 10.5) * mm, "end": v(5.93, 10.67) * mm});
            skLineSegment(sketch, "E424", {"start": v(6.1, 10.5) * mm, "end": v(5.93, 10.67) * mm});
            skLineSegment(sketch, "E425", {"start": v(6.1, 10.5) * mm, "end": v(6.27, 10.84) * mm});
            skLineSegment(sketch, "E426", {"start": v(8.64, 10.67) * mm, "end": v(8.8, 10.5) * mm});
            skLineSegment(sketch, "E427", {"start": v(8.8, 10.5) * mm, "end": v(9.14, 10.84) * mm});
            skLineSegment(sketch, "E428", {"start": v(10.33, 10.5) * mm, "end": v(10.33, 10.67) * mm});
            skLineSegment(sketch, "E429", {"start": v(11.51, 10.5) * mm, "end": v(11.2, 10.7) * mm});
            skLineSegment(sketch, "E430", {"start": v(11.2, 10.7) * mm, "end": v(11, 10.84) * mm});
            skLineSegment(sketch, "E431", {"start": v(11, 10.84) * mm, "end": v(10.5, 10.84) * mm});
            skLineSegment(sketch, "E432", {"start": v(10.5, 10.84) * mm, "end": v(10.33, 10.67) * mm});
            skLineSegment(sketch, "E433", {"start": v(11.68, 10.5) * mm, "end": v(11.51, 10.5) * mm});
            skLineSegment(sketch, "E434", {"start": v(11.85, 10.5) * mm, "end": v(11.68, 10.5) * mm});
            skLineSegment(sketch, "E435", {"start": v(12.87, 10.5) * mm, "end": v(12.53, 10.67) * mm});
            skLineSegment(sketch, "E436", {"start": v(12.53, 10.67) * mm, "end": v(12.18, 10.55) * mm});
            skLineSegment(sketch, "E437", {"start": v(12.18, 10.55) * mm, "end": v(11.85, 10.5) * mm});
            skLineSegment(sketch, "E438", {"start": v(13.04, 10.5) * mm, "end": v(12.87, 10.5) * mm});
            skLineSegment(sketch, "E439", {"start": v(13.04, 10.5) * mm, "end": v(13.04, 10.67) * mm});
            skLineSegment(sketch, "E440", {"start": v(22.52, 10.5) * mm, "end": v(22.52, 10.67) * mm});
            skLineSegment(sketch, "E441", {"start": v(22.52, 10.67) * mm, "end": v(22.35, 10.67) * mm});
            skLineSegment(sketch, "E442", {"start": v(-10, 10.33) * mm, "end": v(-10.33, 10.67) * mm});
            skLineSegment(sketch, "E443", {"start": v(-10, 10.33) * mm, "end": v(-9.82, 10.5) * mm});
            skLineSegment(sketch, "E444", {"start": v(-9.31, 10.33) * mm, "end": v(-9.31, 10.5) * mm});
            skLineSegment(sketch, "E445", {"start": v(-6.43, 10.33) * mm, "end": v(-6.27, 10.67) * mm});
            skLineSegment(sketch, "E446", {"start": v(-4.74, 10.33) * mm, "end": v(-4.91, 10.5) * mm});
            skLineSegment(sketch, "E447", {"start": v(-4.74, 10.33) * mm, "end": v(-4.57, 10.67) * mm});
            skLineSegment(sketch, "E448", {"start": v(-3.22, 10.33) * mm, "end": v(-3.22, 10.5) * mm});
            skLineSegment(sketch, "E449", {"start": v(5.59, 10.33) * mm, "end": v(5.76, 10.5) * mm});
            skLineSegment(sketch, "E450", {"start": v(5.93, 10.33) * mm, "end": v(5.76, 10.5) * mm});
            skLineSegment(sketch, "E451", {"start": v(5.93, 10.33) * mm, "end": v(6.1, 10.5) * mm});
            skLineSegment(sketch, "E452", {"start": v(9.65, 10.33) * mm, "end": v(9.82, 10.67) * mm});
            skLineSegment(sketch, "E453", {"start": v(11.68, 10.33) * mm, "end": v(11.68, 10.5) * mm});
            skLineSegment(sketch, "E454", {"start": v(13.72, 10.33) * mm, "end": v(13.38, 10.67) * mm});
            skLineSegment(sketch, "E455", {"start": v(13.89, 10.33) * mm, "end": v(13.72, 10.33) * mm});
            skLineSegment(sketch, "E456", {"start": v(13.89, 10.33) * mm, "end": v(14.56, 10.84) * mm});
            skLineSegment(sketch, "E457", {"start": v(20.32, 12.7) * mm, "end": v(20.18, 12.34) * mm});
            skLineSegment(sketch, "E458", {"start": v(20.18, 12.34) * mm, "end": v(19.98, 11.68) * mm});
            skLineSegment(sketch, "E459", {"start": v(19.98, 11.68) * mm, "end": v(20.15, 11.18) * mm});
            skLineSegment(sketch, "E460", {"start": v(20.15, 11.18) * mm, "end": v(20.83, 10.5) * mm});
            skLineSegment(sketch, "E461", {"start": v(20.83, 10.5) * mm, "end": v(21.34, 10.33) * mm});
            skLineSegment(sketch, "E462", {"start": v(21.34, 10.33) * mm, "end": v(22.2, 10.63) * mm});
            skLineSegment(sketch, "E463", {"start": v(22.2, 10.63) * mm, "end": v(22.35, 10.67) * mm});
            skLineSegment(sketch, "E464", {"start": v(-10, 10.16) * mm, "end": v(-10, 10.33) * mm});
            skLineSegment(sketch, "E465", {"start": v(-9.82, 10.16) * mm, "end": v(-10, 10.16) * mm});
            skLineSegment(sketch, "E466", {"start": v(-9.31, 10.16) * mm, "end": v(-9.48, 10.16) * mm});
            skLineSegment(sketch, "E467", {"start": v(-9.31, 10.16) * mm, "end": v(-9.31, 10.33) * mm});
            skLineSegment(sketch, "E468", {"start": v(-6.94, 10.16) * mm, "end": v(-6.77, 10.33) * mm});
            skLineSegment(sketch, "E469", {"start": v(-6.77, 10.33) * mm, "end": v(-6.43, 10.33) * mm});
            skLineSegment(sketch, "E470", {"start": v(-6.27, 10.16) * mm, "end": v(-6.43, 10.33) * mm});
            skLineSegment(sketch, "E471", {"start": v(-3.73, 10.5) * mm, "end": v(-3.39, 10.16) * mm});
            skLineSegment(sketch, "E472", {"start": v(-3.39, 10.16) * mm, "end": v(-3.22, 10.33) * mm});
            skLineSegment(sketch, "E473", {"start": v(0.17, 10.16) * mm, "end": v(0, 10.33) * mm});
            skLineSegment(sketch, "E474", {"start": v(0, 10.33) * mm, "end": v(0, 10.67) * mm});
            skLineSegment(sketch, "E475", {"start": v(5.76, 10.16) * mm, "end": v(5.59, 10.33) * mm});
            skLineSegment(sketch, "E476", {"start": v(5.93, 10.16) * mm, "end": v(5.76, 10.16) * mm});
            skLineSegment(sketch, "E477", {"start": v(5.93, 10.16) * mm, "end": v(5.93, 10.33) * mm});
            skLineSegment(sketch, "E478", {"start": v(6.1, 10.16) * mm, "end": v(5.93, 10.16) * mm});
            skLineSegment(sketch, "E479", {"start": v(9.65, 10.16) * mm, "end": v(9.65, 10.33) * mm});
            skLineSegment(sketch, "E480", {"start": v(9.82, 10.16) * mm, "end": v(9.65, 10.16) * mm});
            skLineSegment(sketch, "E481", {"start": v(10, 10.16) * mm, "end": v(9.82, 10.16) * mm});
            skLineSegment(sketch, "E482", {"start": v(10, 10.16) * mm, "end": v(10.33, 10.5) * mm});
            skLineSegment(sketch, "E483", {"start": v(13.89, 10.16) * mm, "end": v(13.89, 10.33) * mm});
            skLineSegment(sketch, "E484", {"start": v(-10.67, 10) * mm, "end": v(-10.67, 10.33) * mm});
            skLineSegment(sketch, "E485", {"start": v(-10.67, 10.33) * mm, "end": v(-10.33, 10.67) * mm});
            skLineSegment(sketch, "E486", {"start": v(-9.65, 10) * mm, "end": v(-9.82, 10.16) * mm});
            skLineSegment(sketch, "E487", {"start": v(-9.65, 10) * mm, "end": v(-9.48, 10.16) * mm});
            skLineSegment(sketch, "E488", {"start": v(-7.28, 10) * mm, "end": v(-6.94, 10.16) * mm});
            skLineSegment(sketch, "E489", {"start": v(-6.77, 10) * mm, "end": v(-6.94, 10.16) * mm});
            skLineSegment(sketch, "E490", {"start": v(-6.77, 10) * mm, "end": v(-6.43, 10) * mm});
            skLineSegment(sketch, "E491", {"start": v(-6.43, 10) * mm, "end": v(-6.27, 10.16) * mm});
            skLineSegment(sketch, "E492", {"start": v(-4.91, 10) * mm, "end": v(-5.08, 10.16) * mm});
            skLineSegment(sketch, "E493", {"start": v(-5.08, 10.16) * mm, "end": v(-4.91, 10.5) * mm});
            skLineSegment(sketch, "E494", {"start": v(-4.91, 10) * mm, "end": v(-4.74, 10.33) * mm});
            skLineSegment(sketch, "E495", {"start": v(0.17, 10) * mm, "end": v(0.17, 10.16) * mm});
            skLineSegment(sketch, "E496", {"start": v(0.34, 10) * mm, "end": v(0.17, 10) * mm});
            skLineSegment(sketch, "E497", {"start": v(0.68, 10) * mm, "end": v(0.5, 10.16) * mm});
            skLineSegment(sketch, "E498", {"start": v(0.5, 10.16) * mm, "end": v(0.34, 10) * mm});
            skLineSegment(sketch, "E499", {"start": v(0.85, 10) * mm, "end": v(0.68, 10) * mm});
            skLineSegment(sketch, "E500", {"start": v(0.85, 10) * mm, "end": v(1.19, 10.33) * mm});
            skLineSegment(sketch, "E501", {"start": v(1.19, 10.33) * mm, "end": v(1.19, 10.84) * mm});
            skLineSegment(sketch, "E502", {"start": v(2.7, 10) * mm, "end": v(2.7, 10.5) * mm});
            skLineSegment(sketch, "E503", {"start": v(5.42, 10) * mm, "end": v(5.59, 10.33) * mm});
            skLineSegment(sketch, "E504", {"start": v(5.93, 10) * mm, "end": v(5.93, 10.16) * mm});
            skLineSegment(sketch, "E505", {"start": v(6.27, 10) * mm, "end": v(6.1, 10.16) * mm});
            skLineSegment(sketch, "E506", {"start": v(10, 10) * mm, "end": v(10, 10.16) * mm});
            skLineSegment(sketch, "E507", {"start": v(11.68, 10) * mm, "end": v(11.68, 10.33) * mm});
            skLineSegment(sketch, "E508", {"start": v(-10.67, 9.82) * mm, "end": v(-10.67, 10) * mm});
            skLineSegment(sketch, "E509", {"start": v(-10.5, 9.82) * mm, "end": v(-10.67, 9.82) * mm});
            skLineSegment(sketch, "E510", {"start": v(-10.33, 9.82) * mm, "end": v(-10.5, 9.82) * mm});
            skLineSegment(sketch, "E511", {"start": v(-10.33, 9.82) * mm, "end": v(-10, 10.16) * mm});
            skLineSegment(sketch, "E512", {"start": v(-8.97, 9.82) * mm, "end": v(-9.31, 10.16) * mm});
            skLineSegment(sketch, "E513", {"start": v(-8.8, 9.82) * mm, "end": v(-8.97, 9.82) * mm});
            skLineSegment(sketch, "E514", {"start": v(-8.8, 9.82) * mm, "end": v(-8.47, 10.16) * mm});
            skLineSegment(sketch, "E515", {"start": v(-8.47, 10.16) * mm, "end": v(-8.47, 10.33) * mm});
            skLineSegment(sketch, "E516", {"start": v(-8.47, 10.33) * mm, "end": v(-8.8, 10.67) * mm});
            skLineSegment(sketch, "E517", {"start": v(-7.45, 9.82) * mm, "end": v(-7.28, 10) * mm});
            skLineSegment(sketch, "E518", {"start": v(-7.11, 9.82) * mm, "end": v(-7.28, 10) * mm});
            skLineSegment(sketch, "E519", {"start": v(-7.11, 9.82) * mm, "end": v(-6.77, 10) * mm});
            skLineSegment(sketch, "E520", {"start": v(-5.25, 9.82) * mm, "end": v(-6.1, 10.84) * mm});
            skLineSegment(sketch, "E521", {"start": v(-5.08, 9.82) * mm, "end": v(-5.25, 9.82) * mm});
            skLineSegment(sketch, "E522", {"start": v(-5.08, 9.82) * mm, "end": v(-4.91, 10) * mm});
            skLineSegment(sketch, "E523", {"start": v(0, 9.82) * mm, "end": v(0.17, 10) * mm});
            skLineSegment(sketch, "E524", {"start": v(0.5, 9.82) * mm, "end": v(0.34, 10) * mm});
            skLineSegment(sketch, "E525", {"start": v(0.5, 9.82) * mm, "end": v(0.68, 10) * mm});
            skLineSegment(sketch, "E526", {"start": v(0.85, 9.82) * mm, "end": v(0.85, 10) * mm});
            skLineSegment(sketch, "E527", {"start": v(5.25, 9.82) * mm, "end": v(5.42, 10) * mm});
            skLineSegment(sketch, "E528", {"start": v(5.59, 9.82) * mm, "end": v(5.42, 10) * mm});
            skLineSegment(sketch, "E529", {"start": v(5.76, 9.82) * mm, "end": v(5.59, 9.82) * mm});
            skLineSegment(sketch, "E530", {"start": v(5.93, 9.82) * mm, "end": v(5.76, 9.82) * mm});
            skLineSegment(sketch, "E531", {"start": v(5.93, 9.82) * mm, "end": v(5.93, 10) * mm});
            skLineSegment(sketch, "E532", {"start": v(6.1, 9.82) * mm, "end": v(5.93, 9.82) * mm});
            skLineSegment(sketch, "E533", {"start": v(6.27, 9.82) * mm, "end": v(6.1, 9.82) * mm});
            skLineSegment(sketch, "E534", {"start": v(6.27, 9.82) * mm, "end": v(6.27, 10) * mm});
            skLineSegment(sketch, "E535", {"start": v(6.43, 9.82) * mm, "end": v(6.27, 9.82) * mm});
            skLineSegment(sketch, "E536", {"start": v(6.6, 9.82) * mm, "end": v(6.43, 9.82) * mm});
            skLineSegment(sketch, "E537", {"start": v(6.94, 9.82) * mm, "end": v(6.77, 10) * mm});
            skLineSegment(sketch, "E538", {"start": v(6.77, 10) * mm, "end": v(6.6, 9.82) * mm});
            skLineSegment(sketch, "E539", {"start": v(10.16, 9.82) * mm, "end": v(10, 10) * mm});
            skLineSegment(sketch, "E540", {"start": v(11.51, 9.82) * mm, "end": v(11.68, 10) * mm});
            skLineSegment(sketch, "E541", {"start": v(11.85, 9.82) * mm, "end": v(11.68, 10) * mm});
            skLineSegment(sketch, "E542", {"start": v(-11, 9.65) * mm, "end": v(-11.18, 9.65) * mm});
            skLineSegment(sketch, "E543", {"start": v(-10.84, 9.65) * mm, "end": v(-11, 9.65) * mm});
            skLineSegment(sketch, "E544", {"start": v(-10.84, 9.65) * mm, "end": v(-10.67, 9.82) * mm});
            skLineSegment(sketch, "E545", {"start": v(-10.33, 9.65) * mm, "end": v(-10.33, 9.82) * mm});
            skLineSegment(sketch, "E546", {"start": v(-10, 9.65) * mm, "end": v(-9.65, 10) * mm});
            skLineSegment(sketch, "E547", {"start": v(-9.48, 9.65) * mm, "end": v(-9.65, 10) * mm});
            skLineSegment(sketch, "E548", {"start": v(-8.8, 9.65) * mm, "end": v(-8.8, 9.82) * mm});
            skLineSegment(sketch, "E549", {"start": v(-7.45, 9.65) * mm, "end": v(-7.45, 9.82) * mm});
            skLineSegment(sketch, "E550", {"start": v(-7.28, 9.65) * mm, "end": v(-7.45, 9.65) * mm});
            skLineSegment(sketch, "E551", {"start": v(-7.28, 9.65) * mm, "end": v(-7.11, 9.82) * mm});
            skLineSegment(sketch, "E552", {"start": v(-5.08, 9.65) * mm, "end": v(-5.08, 9.82) * mm});
            skLineSegment(sketch, "E553", {"start": v(-4.91, 9.65) * mm, "end": v(-5.08, 9.65) * mm});
            skLineSegment(sketch, "E554", {"start": v(-0.17, 9.65) * mm, "end": v(-0.46, 10.18) * mm});
            skLineSegment(sketch, "E555", {"start": v(-0.46, 10.18) * mm, "end": v(-0.5, 10.5) * mm});
            skLineSegment(sketch, "E556", {"start": v(-0.17, 9.65) * mm, "end": v(0, 9.82) * mm});
            skLineSegment(sketch, "E557", {"start": v(0.17, 9.65) * mm, "end": v(0, 9.82) * mm});
            skLineSegment(sketch, "E558", {"start": v(0.34, 9.65) * mm, "end": v(0.17, 9.65) * mm});
            skLineSegment(sketch, "E559", {"start": v(0.5, 9.65) * mm, "end": v(0.34, 9.65) * mm});
            skLineSegment(sketch, "E560", {"start": v(0.5, 9.65) * mm, "end": v(0.5, 9.82) * mm});
            skLineSegment(sketch, "E561", {"start": v(1.02, 9.65) * mm, "end": v(0.85, 9.82) * mm});
            skLineSegment(sketch, "E562", {"start": v(4.91, 9.65) * mm, "end": v(5.25, 9.82) * mm});
            skLineSegment(sketch, "E563", {"start": v(5.42, 9.65) * mm, "end": v(5.25, 9.82) * mm});
            skLineSegment(sketch, "E564", {"start": v(5.42, 9.65) * mm, "end": v(5.59, 9.82) * mm});
            skLineSegment(sketch, "E565", {"start": v(6.77, 9.65) * mm, "end": v(6.6, 9.82) * mm});
            skLineSegment(sketch, "E566", {"start": v(6.77, 9.65) * mm, "end": v(6.94, 9.82) * mm});
            skLineSegment(sketch, "E567", {"start": v(7.11, 9.65) * mm, "end": v(6.94, 9.82) * mm});
            skLineSegment(sketch, "E568", {"start": v(9.82, 9.65) * mm, "end": v(9.48, 10) * mm});
            skLineSegment(sketch, "E569", {"start": v(9.48, 10) * mm, "end": v(9.65, 10.16) * mm});
            skLineSegment(sketch, "E570", {"start": v(10, 9.65) * mm, "end": v(9.82, 9.65) * mm});
            skLineSegment(sketch, "E571", {"start": v(10, 9.65) * mm, "end": v(10.16, 9.82) * mm});
            skLineSegment(sketch, "E572", {"start": v(11.68, 9.65) * mm, "end": v(11.51, 9.82) * mm});
            skLineSegment(sketch, "E573", {"start": v(11.85, 9.65) * mm, "end": v(11.68, 9.65) * mm});
            skLineSegment(sketch, "E574", {"start": v(11.85, 9.65) * mm, "end": v(11.85, 9.82) * mm});
            skLineSegment(sketch, "E575", {"start": v(12.02, 9.65) * mm, "end": v(11.85, 9.65) * mm});
            skLineSegment(sketch, "E576", {"start": v(14.4, 9.65) * mm, "end": v(13.89, 10.16) * mm});
            skLineSegment(sketch, "E577", {"start": v(14.56, 9.65) * mm, "end": v(14.4, 9.65) * mm});
            skLineSegment(sketch, "E578", {"start": v(14.73, 9.65) * mm, "end": v(14.56, 9.65) * mm});
            skLineSegment(sketch, "E579", {"start": v(-11.35, 9.48) * mm, "end": v(-11.18, 9.65) * mm});
            skLineSegment(sketch, "E580", {"start": v(-11, 9.48) * mm, "end": v(-11, 9.65) * mm});
            skLineSegment(sketch, "E581", {"start": v(-10.67, 9.48) * mm, "end": v(-10.84, 9.65) * mm});
            skLineSegment(sketch, "E582", {"start": v(-10.5, 9.48) * mm, "end": v(-10.67, 9.48) * mm});
            skLineSegment(sketch, "E583", {"start": v(-10.5, 9.48) * mm, "end": v(-10.33, 9.65) * mm});
            skLineSegment(sketch, "E584", {"start": v(-10.16, 9.48) * mm, "end": v(-10.33, 9.65) * mm});
            skLineSegment(sketch, "E585", {"start": v(-10, 9.48) * mm, "end": v(-10.16, 9.48) * mm});
            skLineSegment(sketch, "E586", {"start": v(-10, 9.48) * mm, "end": v(-10, 9.65) * mm});
            skLineSegment(sketch, "E587", {"start": v(-9.48, 9.48) * mm, "end": v(-9.48, 9.65) * mm});
            skLineSegment(sketch, "E588", {"start": v(-9.31, 9.48) * mm, "end": v(-9.48, 9.48) * mm});
            skLineSegment(sketch, "E589", {"start": v(-5.25, 9.48) * mm, "end": v(-6.27, 10.16) * mm});
            skLineSegment(sketch, "E590", {"start": v(-5.25, 9.48) * mm, "end": v(-5.08, 9.65) * mm});
            skLineSegment(sketch, "E591", {"start": v(-0.17, 9.48) * mm, "end": v(-0.34, 9.48) * mm});
            skLineSegment(sketch, "E592", {"start": v(-0.17, 9.48) * mm, "end": v(-0.17, 9.65) * mm});
            skLineSegment(sketch, "E593", {"start": v(0, 9.48) * mm, "end": v(-0.17, 9.48) * mm});
            skLineSegment(sketch, "E594", {"start": v(0, 9.48) * mm, "end": v(0.17, 9.65) * mm});
            skLineSegment(sketch, "E595", {"start": v(0.68, 9.48) * mm, "end": v(0.5, 9.65) * mm});
            skLineSegment(sketch, "E596", {"start": v(0.85, 9.48) * mm, "end": v(0.68, 9.48) * mm});
            skLineSegment(sketch, "E597", {"start": v(1.02, 9.48) * mm, "end": v(0.85, 9.48) * mm});
            skLineSegment(sketch, "E598", {"start": v(1.02, 9.48) * mm, "end": v(1.02, 9.65) * mm});
            skLineSegment(sketch, "E599", {"start": v(2.88, 9.48) * mm, "end": v(2.88, 9.82) * mm});
            skLineSegment(sketch, "E600", {"start": v(2.88, 9.82) * mm, "end": v(2.7, 10) * mm});
            skLineSegment(sketch, "E601", {"start": v(4.74, 9.48) * mm, "end": v(4.91, 9.65) * mm});
            skLineSegment(sketch, "E602", {"start": v(5.08, 9.48) * mm, "end": v(4.91, 9.65) * mm});
            skLineSegment(sketch, "E603", {"start": v(5.08, 9.48) * mm, "end": v(5.42, 9.65) * mm});
            skLineSegment(sketch, "E604", {"start": v(6.94, 9.48) * mm, "end": v(6.77, 9.65) * mm});
            skLineSegment(sketch, "E605", {"start": v(6.94, 9.48) * mm, "end": v(7.11, 9.65) * mm});
            skLineSegment(sketch, "E606", {"start": v(7.28, 9.48) * mm, "end": v(7.11, 9.65) * mm});
            skLineSegment(sketch, "E607", {"start": v(10, 9.48) * mm, "end": v(10, 9.65) * mm});
            skLineSegment(sketch, "E608", {"start": v(10.16, 9.82) * mm, "end": v(10.52, 9.69) * mm});
            skLineSegment(sketch, "E609", {"start": v(10.52, 9.69) * mm, "end": v(11, 9.48) * mm});
            skLineSegment(sketch, "E610", {"start": v(11, 9.48) * mm, "end": v(11.51, 9.82) * mm});
            skLineSegment(sketch, "E611", {"start": v(11.85, 9.48) * mm, "end": v(11.85, 9.65) * mm});
            skLineSegment(sketch, "E612", {"start": v(14.56, 9.48) * mm, "end": v(14.56, 9.65) * mm});
            skLineSegment(sketch, "E613", {"start": v(-11.18, 9.31) * mm, "end": v(-11.35, 9.48) * mm});
            skLineSegment(sketch, "E614", {"start": v(-11, 9.31) * mm, "end": v(-11.18, 9.31) * mm});
            skLineSegment(sketch, "E615", {"start": v(-11, 9.31) * mm, "end": v(-11, 9.48) * mm});
            skLineSegment(sketch, "E616", {"start": v(-10.84, 9.31) * mm, "end": v(-11, 9.31) * mm});
            skLineSegment(sketch, "E617", {"start": v(-10.84, 9.31) * mm, "end": v(-10.67, 9.48) * mm});
            skLineSegment(sketch, "E618", {"start": v(-10.5, 9.31) * mm, "end": v(-10.5, 9.48) * mm});
            skLineSegment(sketch, "E619", {"start": v(-10, 9.31) * mm, "end": v(-10, 9.48) * mm});
            skLineSegment(sketch, "E620", {"start": v(-9.48, 9.31) * mm, "end": v(-9.48, 9.48) * mm});
            skLineSegment(sketch, "E621", {"start": v(-9.31, 9.48) * mm, "end": v(-9.16, 9.45) * mm});
            skLineSegment(sketch, "E622", {"start": v(-9.16, 9.45) * mm, "end": v(-8.97, 9.31) * mm});
            skLineSegment(sketch, "E623", {"start": v(-8.97, 9.31) * mm, "end": v(-8.8, 9.65) * mm});
            skLineSegment(sketch, "E624", {"start": v(-4.57, 9.31) * mm, "end": v(-4.91, 9.65) * mm});
            skLineSegment(sketch, "E625", {"start": v(-0.17, 9.31) * mm, "end": v(-0.17, 9.48) * mm});
            skLineSegment(sketch, "E626", {"start": v(0.5, 9.31) * mm, "end": v(0.68, 9.48) * mm});
            skLineSegment(sketch, "E627", {"start": v(1.02, 9.31) * mm, "end": v(1.02, 9.48) * mm});
            skLineSegment(sketch, "E628", {"start": v(2.7, 9.31) * mm, "end": v(2.54, 9.48) * mm});
            skLineSegment(sketch, "E629", {"start": v(2.54, 9.48) * mm, "end": v(2.54, 9.82) * mm});
            skLineSegment(sketch, "E630", {"start": v(2.54, 9.82) * mm, "end": v(2.7, 10) * mm});
            skLineSegment(sketch, "E631", {"start": v(2.7, 9.31) * mm, "end": v(2.88, 9.48) * mm});
            skLineSegment(sketch, "E632", {"start": v(3.05, 9.31) * mm, "end": v(2.88, 9.48) * mm});
            skLineSegment(sketch, "E633", {"start": v(4.23, 9.31) * mm, "end": v(4.4, 9.48) * mm});
            skLineSegment(sketch, "E634", {"start": v(4.4, 9.48) * mm, "end": v(4.74, 9.48) * mm});
            skLineSegment(sketch, "E635", {"start": v(4.91, 9.31) * mm, "end": v(4.74, 9.48) * mm});
            skLineSegment(sketch, "E636", {"start": v(4.91, 9.31) * mm, "end": v(5.08, 9.48) * mm});
            skLineSegment(sketch, "E637", {"start": v(7.11, 9.31) * mm, "end": v(6.94, 9.48) * mm});
            skLineSegment(sketch, "E638", {"start": v(7.28, 9.31) * mm, "end": v(7.11, 9.31) * mm});
            skLineSegment(sketch, "E639", {"start": v(7.28, 9.31) * mm, "end": v(7.28, 9.48) * mm});
            skLineSegment(sketch, "E640", {"start": v(-10.33, 9.14) * mm, "end": v(-10.5, 9.31) * mm});
            skLineSegment(sketch, "E641", {"start": v(-10, 9.14) * mm, "end": v(-10, 9.31) * mm});
            skLineSegment(sketch, "E642", {"start": v(-9.82, 9.14) * mm, "end": v(-10, 9.14) * mm});
            skLineSegment(sketch, "E643", {"start": v(-9.82, 9.14) * mm, "end": v(-9.48, 9.31) * mm});
            skLineSegment(sketch, "E644", {"start": v(-4.74, 9.14) * mm, "end": v(-4.91, 9.14) * mm});
            skLineSegment(sketch, "E645", {"start": v(-4.91, 9.14) * mm, "end": v(-5.25, 9.48) * mm});
            skLineSegment(sketch, "E646", {"start": v(-4.74, 9.14) * mm, "end": v(-4.57, 9.31) * mm});
            skLineSegment(sketch, "E647", {"start": v(0.34, 9.14) * mm, "end": v(0.5, 9.31) * mm});
            skLineSegment(sketch, "E648", {"start": v(0.68, 9.14) * mm, "end": v(0.5, 9.31) * mm});
            skLineSegment(sketch, "E649", {"start": v(1.02, 9.14) * mm, "end": v(1.02, 9.31) * mm});
            skLineSegment(sketch, "E650", {"start": v(2.88, 9.14) * mm, "end": v(2.7, 9.31) * mm});
            skLineSegment(sketch, "E651", {"start": v(3.05, 9.14) * mm, "end": v(2.88, 9.14) * mm});
            skLineSegment(sketch, "E652", {"start": v(3.05, 9.14) * mm, "end": v(3.05, 9.31) * mm});
            skLineSegment(sketch, "E653", {"start": v(3.22, 9.14) * mm, "end": v(3.05, 9.14) * mm});
            skLineSegment(sketch, "E654", {"start": v(3.22, 9.14) * mm, "end": v(4.23, 9.31) * mm});
            skLineSegment(sketch, "E655", {"start": v(4.4, 9.14) * mm, "end": v(4.23, 9.31) * mm});
            skLineSegment(sketch, "E656", {"start": v(4.4, 9.14) * mm, "end": v(4.74, 9.14) * mm});
            skLineSegment(sketch, "E657", {"start": v(4.74, 9.14) * mm, "end": v(4.91, 9.31) * mm});
            skLineSegment(sketch, "E658", {"start": v(7.28, 9.14) * mm, "end": v(7.28, 9.31) * mm});
            skLineSegment(sketch, "E659", {"start": v(14.4, 9.14) * mm, "end": v(14.56, 9.48) * mm});
            skLineSegment(sketch, "E660", {"start": v(-15.07, 8.97) * mm, "end": v(-15.07, 9.48) * mm});
            skLineSegment(sketch, "E661", {"start": v(-15.07, 9.48) * mm, "end": v(-14.24, 10.2) * mm});
            skLineSegment(sketch, "E662", {"start": v(-14.24, 10.2) * mm, "end": v(-14.04, 10.3) * mm});
            skLineSegment(sketch, "E663", {"start": v(-14.04, 10.3) * mm, "end": v(-12.7, 11.68) * mm});
            skLineSegment(sketch, "E664", {"start": v(-12.7, 11.68) * mm, "end": v(-11.68, 11.85) * mm});
            skLineSegment(sketch, "E665", {"start": v(-11.68, 11.85) * mm, "end": v(-11.51, 11.68) * mm});
            skLineSegment(sketch, "E666", {"start": v(-10.33, 8.97) * mm, "end": v(-10.33, 9.14) * mm});
            skLineSegment(sketch, "E667", {"start": v(-10.16, 8.97) * mm, "end": v(-10.33, 8.97) * mm});
            skLineSegment(sketch, "E668", {"start": v(-10.16, 8.97) * mm, "end": v(-10, 9.14) * mm});
            skLineSegment(sketch, "E669", {"start": v(-1.86, 8.97) * mm, "end": v(-1.65, 9.96) * mm});
            skLineSegment(sketch, "E670", {"start": v(-1.65, 9.96) * mm, "end": v(-1.19, 10.5) * mm});
            skLineSegment(sketch, "E671", {"start": v(0.17, 8.97) * mm, "end": v(0.34, 9.14) * mm});
            skLineSegment(sketch, "E672", {"start": v(0.5, 8.97) * mm, "end": v(0.34, 9.14) * mm});
            skLineSegment(sketch, "E673", {"start": v(0.5, 8.97) * mm, "end": v(0.68, 9.14) * mm});
            skLineSegment(sketch, "E674", {"start": v(0.85, 8.97) * mm, "end": v(0.68, 9.14) * mm});
            skLineSegment(sketch, "E675", {"start": v(0.85, 8.97) * mm, "end": v(1.02, 9.14) * mm});
            skLineSegment(sketch, "E676", {"start": v(7.45, 8.97) * mm, "end": v(7.28, 9.14) * mm});
            skLineSegment(sketch, "E677", {"start": v(13.72, 8.97) * mm, "end": v(13.5, 9.96) * mm});
            skLineSegment(sketch, "E678", {"start": v(13.5, 9.96) * mm, "end": v(13.04, 10.5) * mm});
            skLineSegment(sketch, "E679", {"start": v(14.4, 8.97) * mm, "end": v(14.22, 8.97) * mm});
            skLineSegment(sketch, "E680", {"start": v(14.4, 8.97) * mm, "end": v(14.4, 9.14) * mm});
            skLineSegment(sketch, "E681", {"start": v(-15.07, 8.8) * mm, "end": v(-15.24, 8.8) * mm});
            skLineSegment(sketch, "E682", {"start": v(-15.07, 8.8) * mm, "end": v(-15.07, 8.97) * mm});
            skLineSegment(sketch, "E683", {"start": v(-14.05, 8.8) * mm, "end": v(-14.05, 9.31) * mm});
            skLineSegment(sketch, "E684", {"start": v(-14.05, 9.31) * mm, "end": v(-13.89, 9.48) * mm});
            skLineSegment(sketch, "E685", {"start": v(-13.89, 9.48) * mm, "end": v(-13.2, 9.65) * mm});
            skLineSegment(sketch, "E686", {"start": v(-13.2, 9.65) * mm, "end": v(-12.53, 10.5) * mm});
            skLineSegment(sketch, "E687", {"start": v(-10.16, 8.8) * mm, "end": v(-10.16, 8.97) * mm});
            skLineSegment(sketch, "E688", {"start": v(-7.96, 8.8) * mm, "end": v(-7.75, 9.29) * mm});
            skLineSegment(sketch, "E689", {"start": v(-7.75, 9.29) * mm, "end": v(-7.45, 9.65) * mm});
            skLineSegment(sketch, "E690", {"start": v(-1.86, 8.8) * mm, "end": v(-1.86, 8.97) * mm});
            skLineSegment(sketch, "E691", {"start": v(-1.7, 8.8) * mm, "end": v(-1.86, 8.8) * mm});
            skLineSegment(sketch, "E692", {"start": v(-1.7, 8.8) * mm, "end": v(-0.88, 9.02) * mm});
            skLineSegment(sketch, "E693", {"start": v(-0.88, 9.02) * mm, "end": v(-0.34, 9.48) * mm});
            skLineSegment(sketch, "E694", {"start": v(-0.17, 9.31) * mm, "end": v(-0.17, 8.97) * mm});
            skLineSegment(sketch, "E695", {"start": v(-0.17, 8.97) * mm, "end": v(0, 8.8) * mm});
            skLineSegment(sketch, "E696", {"start": v(0, 8.8) * mm, "end": v(0.17, 8.97) * mm});
            skLineSegment(sketch, "E697", {"start": v(0.34, 8.8) * mm, "end": v(0.17, 8.97) * mm});
            skLineSegment(sketch, "E698", {"start": v(0.34, 8.8) * mm, "end": v(0.5, 8.97) * mm});
            skLineSegment(sketch, "E699", {"start": v(1.86, 8.8) * mm, "end": v(1.02, 9.14) * mm});
            skLineSegment(sketch, "E700", {"start": v(2.2, 8.8) * mm, "end": v(1.86, 8.8) * mm});
            skLineSegment(sketch, "E701", {"start": v(2.2, 8.8) * mm, "end": v(2.88, 9.14) * mm});
            skLineSegment(sketch, "E702", {"start": v(7.28, 8.8) * mm, "end": v(7.11, 8.8) * mm});
            skLineSegment(sketch, "E703", {"start": v(7.45, 8.8) * mm, "end": v(7.28, 8.8) * mm});
            skLineSegment(sketch, "E704", {"start": v(7.45, 8.8) * mm, "end": v(7.45, 8.97) * mm});
            skLineSegment(sketch, "E705", {"start": v(7.62, 8.8) * mm, "end": v(7.45, 8.8) * mm});
            skLineSegment(sketch, "E706", {"start": v(7.96, 8.8) * mm, "end": v(7.79, 8.97) * mm});
            skLineSegment(sketch, "E707", {"start": v(7.79, 8.97) * mm, "end": v(7.62, 8.8) * mm});
            skLineSegment(sketch, "E708", {"start": v(11.85, 9.48) * mm, "end": v(11.85, 9.31) * mm});
            skLineSegment(sketch, "E709", {"start": v(11.85, 9.31) * mm, "end": v(12.36, 8.8) * mm});
            skLineSegment(sketch, "E710", {"start": v(12.36, 8.8) * mm, "end": v(12.7, 8.8) * mm});
            skLineSegment(sketch, "E711", {"start": v(12.7, 8.8) * mm, "end": v(12.9, 9.13) * mm});
            skLineSegment(sketch, "E712", {"start": v(12.9, 9.13) * mm, "end": v(13.04, 9.31) * mm});
            skLineSegment(sketch, "E713", {"start": v(13.04, 9.31) * mm, "end": v(12.7, 9.65) * mm});
            skLineSegment(sketch, "E714", {"start": v(12.7, 9.65) * mm, "end": v(12.02, 9.65) * mm});
            skLineSegment(sketch, "E715", {"start": v(13.89, 8.8) * mm, "end": v(13.72, 8.8) * mm});
            skLineSegment(sketch, "E716", {"start": v(13.72, 8.8) * mm, "end": v(13.72, 8.97) * mm});
            skLineSegment(sketch, "E717", {"start": v(13.89, 8.8) * mm, "end": v(14.22, 8.97) * mm});
            skLineSegment(sketch, "E718", {"start": v(-14.22, 8.64) * mm, "end": v(-14.05, 8.8) * mm});
            skLineSegment(sketch, "E719", {"start": v(-13.89, 8.64) * mm, "end": v(-14.05, 8.8) * mm});
            skLineSegment(sketch, "E720", {"start": v(-7.96, 8.64) * mm, "end": v(-8.13, 8.64) * mm});
            skLineSegment(sketch, "E721", {"start": v(-7.96, 8.64) * mm, "end": v(-7.96, 8.8) * mm});
            skLineSegment(sketch, "E722", {"start": v(-7.79, 8.64) * mm, "end": v(-7.96, 8.64) * mm});
            skLineSegment(sketch, "E723", {"start": v(-7.28, 8.64) * mm, "end": v(-7.79, 8.64) * mm});
            skLineSegment(sketch, "E724", {"start": v(-2.2, 8.64) * mm, "end": v(-4.57, 9.31) * mm});
            skLineSegment(sketch, "E725", {"start": v(-2.03, 8.64) * mm, "end": v(-2.2, 8.64) * mm});
            skLineSegment(sketch, "E726", {"start": v(-2.03, 8.64) * mm, "end": v(-1.86, 8.8) * mm});
            skLineSegment(sketch, "E727", {"start": v(2.37, 8.64) * mm, "end": v(2.2, 8.8) * mm});
            skLineSegment(sketch, "E728", {"start": v(2.54, 8.64) * mm, "end": v(2.37, 8.64) * mm});
            skLineSegment(sketch, "E729", {"start": v(2.54, 8.64) * mm, "end": v(3.2, 8.7) * mm});
            skLineSegment(sketch, "E730", {"start": v(3.2, 8.7) * mm, "end": v(4.22, 9) * mm});
            skLineSegment(sketch, "E731", {"start": v(4.22, 9) * mm, "end": v(4.4, 9.14) * mm});
            skLineSegment(sketch, "E732", {"start": v(6.94, 8.64) * mm, "end": v(6.94, 8.8) * mm});
            skLineSegment(sketch, "E733", {"start": v(6.94, 8.8) * mm, "end": v(7.11, 8.8) * mm});
            skLineSegment(sketch, "E734", {"start": v(7.45, 8.64) * mm, "end": v(7.45, 8.8) * mm});
            skLineSegment(sketch, "E735", {"start": v(7.96, 8.64) * mm, "end": v(7.96, 8.8) * mm});
            skLineSegment(sketch, "E736", {"start": v(8.13, 8.64) * mm, "end": v(7.96, 8.64) * mm});
            skLineSegment(sketch, "E737", {"start": v(8.13, 8.64) * mm, "end": v(8.47, 8.8) * mm});
            skLineSegment(sketch, "E738", {"start": v(8.64, 8.64) * mm, "end": v(8.64, 8.8) * mm});
            skLineSegment(sketch, "E739", {"start": v(8.64, 8.8) * mm, "end": v(8.47, 8.8) * mm});
            skLineSegment(sketch, "E740", {"start": v(14.9, 8.64) * mm, "end": v(14.4, 8.97) * mm});
            skLineSegment(sketch, "E741", {"start": v(-14.56, 8.47) * mm, "end": v(-15.07, 8.8) * mm});
            skLineSegment(sketch, "E742", {"start": v(-14.4, 8.47) * mm, "end": v(-14.56, 8.47) * mm});
            skLineSegment(sketch, "E743", {"start": v(-14.4, 8.47) * mm, "end": v(-14.22, 8.64) * mm});
            skLineSegment(sketch, "E744", {"start": v(-14.05, 8.47) * mm, "end": v(-14.22, 8.64) * mm});
            skLineSegment(sketch, "E745", {"start": v(-14.05, 8.47) * mm, "end": v(-13.89, 8.64) * mm});
            skLineSegment(sketch, "E746", {"start": v(-13.89, 8.64) * mm, "end": v(-13.72, 8.55) * mm});
            skLineSegment(sketch, "E747", {"start": v(-13.72, 8.55) * mm, "end": v(-11.35, 9.48) * mm});
            skLineSegment(sketch, "E748", {"start": v(-7.96, 8.47) * mm, "end": v(-7.96, 8.64) * mm});
            skLineSegment(sketch, "E749", {"start": v(-7.28, 8.47) * mm, "end": v(-7.28, 8.64) * mm});
            skLineSegment(sketch, "E750", {"start": v(-7.11, 8.47) * mm, "end": v(-7.28, 8.47) * mm});
            skLineSegment(sketch, "E751", {"start": v(-2.03, 8.47) * mm, "end": v(-2.03, 8.64) * mm});
            skLineSegment(sketch, "E752", {"start": v(-1.86, 8.47) * mm, "end": v(-2.03, 8.47) * mm});
            skLineSegment(sketch, "E753", {"start": v(0.34, 8.8) * mm, "end": v(0.34, 8.64) * mm});
            skLineSegment(sketch, "E754", {"start": v(0.34, 8.64) * mm, "end": v(0.5, 8.47) * mm});
            skLineSegment(sketch, "E755", {"start": v(0.5, 8.47) * mm, "end": v(0.85, 8.8) * mm});
            skLineSegment(sketch, "E756", {"start": v(0.85, 8.8) * mm, "end": v(0.85, 8.97) * mm});
            skLineSegment(sketch, "E757", {"start": v(1.52, 8.47) * mm, "end": v(1.86, 8.8) * mm});
            skLineSegment(sketch, "E758", {"start": v(2.37, 8.47) * mm, "end": v(2.37, 8.64) * mm});
            skLineSegment(sketch, "E759", {"start": v(7.96, 8.47) * mm, "end": v(7.96, 8.64) * mm});
            skLineSegment(sketch, "E760", {"start": v(8.64, 8.47) * mm, "end": v(8.64, 8.64) * mm});
            skLineSegment(sketch, "E761", {"start": v(-14.56, 8.3) * mm, "end": v(-14.56, 8.47) * mm});
            skLineSegment(sketch, "E762", {"start": v(-14.22, 8.3) * mm, "end": v(-14.4, 8.47) * mm});
            skLineSegment(sketch, "E763", {"start": v(-14.05, 8.3) * mm, "end": v(-14.22, 8.3) * mm});
            skLineSegment(sketch, "E764", {"start": v(-14.05, 8.3) * mm, "end": v(-14.05, 8.47) * mm});
            skLineSegment(sketch, "E765", {"start": v(-11, 8.3) * mm, "end": v(-10.33, 8.97) * mm});
            skLineSegment(sketch, "E766", {"start": v(-7.28, 8.3) * mm, "end": v(-7.28, 8.47) * mm});
            skLineSegment(sketch, "E767", {"start": v(-2.2, 8.3) * mm, "end": v(-2.03, 8.47) * mm});
            skLineSegment(sketch, "E768", {"start": v(-1.7, 8.3) * mm, "end": v(-1.86, 8.47) * mm});
            skLineSegment(sketch, "E769", {"start": v(1.7, 8.3) * mm, "end": v(1.52, 8.47) * mm});
            skLineSegment(sketch, "E770", {"start": v(2.2, 8.3) * mm, "end": v(1.7, 8.3) * mm});
            skLineSegment(sketch, "E771", {"start": v(2.37, 8.3) * mm, "end": v(2.2, 8.3) * mm});
            skLineSegment(sketch, "E772", {"start": v(2.37, 8.3) * mm, "end": v(2.37, 8.47) * mm});
            skLineSegment(sketch, "E773", {"start": v(6.94, 8.3) * mm, "end": v(6.94, 8.64) * mm});
            skLineSegment(sketch, "E774", {"start": v(7.62, 8.3) * mm, "end": v(7.45, 8.64) * mm});
            skLineSegment(sketch, "E775", {"start": v(7.96, 8.3) * mm, "end": v(7.96, 8.47) * mm});
            skLineSegment(sketch, "E776", {"start": v(8.64, 8.3) * mm, "end": v(8.47, 8.3) * mm});
            skLineSegment(sketch, "E777", {"start": v(8.64, 8.3) * mm, "end": v(8.64, 8.47) * mm});
            skLineSegment(sketch, "E778", {"start": v(-14.73, 8.13) * mm, "end": v(-14.56, 8.3) * mm});
            skLineSegment(sketch, "E779", {"start": v(-14.4, 8.13) * mm, "end": v(-14.56, 8.3) * mm});
            skLineSegment(sketch, "E780", {"start": v(-14.4, 8.13) * mm, "end": v(-14.22, 8.3) * mm});
            skLineSegment(sketch, "E781", {"start": v(-14.05, 8.13) * mm, "end": v(-14.05, 8.3) * mm});
            skLineSegment(sketch, "E782", {"start": v(-11.18, 8.13) * mm, "end": v(-11, 8.3) * mm});
            skLineSegment(sketch, "E783", {"start": v(-10.84, 8.13) * mm, "end": v(-11, 8.3) * mm});
            skLineSegment(sketch, "E784", {"start": v(-10.84, 8.13) * mm, "end": v(-10.67, 8.13) * mm});
            skLineSegment(sketch, "E785", {"start": v(-10.67, 8.13) * mm, "end": v(-10.16, 8.64) * mm});
            skLineSegment(sketch, "E786", {"start": v(-10.16, 8.64) * mm, "end": v(-10.16, 8.8) * mm});
            skLineSegment(sketch, "E787", {"start": v(-8.47, 8.13) * mm, "end": v(-8.47, 8.3) * mm});
            skLineSegment(sketch, "E788", {"start": v(-8.47, 8.3) * mm, "end": v(-8.13, 8.64) * mm});
            skLineSegment(sketch, "E789", {"start": v(-6.77, 8.13) * mm, "end": v(-6.77, 8.47) * mm});
            skLineSegment(sketch, "E790", {"start": v(-6.77, 8.47) * mm, "end": v(-6.94, 8.64) * mm});
            skLineSegment(sketch, "E791", {"start": v(-6.94, 8.64) * mm, "end": v(-7.11, 8.47) * mm});
            skLineSegment(sketch, "E792", {"start": v(-2.37, 8.13) * mm, "end": v(-2.56, 8.25) * mm});
            skLineSegment(sketch, "E793", {"start": v(-2.56, 8.25) * mm, "end": v(-4.38, 8.84) * mm});
            skLineSegment(sketch, "E794", {"start": v(-4.38, 8.84) * mm, "end": v(-4.74, 9.14) * mm});
            skLineSegment(sketch, "E795", {"start": v(-2.37, 8.13) * mm, "end": v(-2.2, 8.3) * mm});
            skLineSegment(sketch, "E796", {"start": v(-1.86, 8.13) * mm, "end": v(-2.2, 8.3) * mm});
            skLineSegment(sketch, "E797", {"start": v(-1.86, 8.13) * mm, "end": v(-1.7, 8.3) * mm});
            skLineSegment(sketch, "E798", {"start": v(2.37, 8.13) * mm, "end": v(2.37, 8.3) * mm});
            skLineSegment(sketch, "E799", {"start": v(6.94, 8.13) * mm, "end": v(6.94, 8.3) * mm});
            skLineSegment(sketch, "E800", {"start": v(7.11, 8.13) * mm, "end": v(6.94, 8.13) * mm});
            skLineSegment(sketch, "E801", {"start": v(7.62, 8.13) * mm, "end": v(7.62, 8.3) * mm});
            skLineSegment(sketch, "E802", {"start": v(7.79, 8.13) * mm, "end": v(7.62, 8.13) * mm});
            skLineSegment(sketch, "E803", {"start": v(7.96, 8.13) * mm, "end": v(7.79, 8.13) * mm});
            skLineSegment(sketch, "E804", {"start": v(7.96, 8.13) * mm, "end": v(7.96, 8.3) * mm});
            skLineSegment(sketch, "E805", {"start": v(14.56, 8.13) * mm, "end": v(14.56, 8.3) * mm});
            skLineSegment(sketch, "E806", {"start": v(14.56, 8.3) * mm, "end": v(14.9, 8.64) * mm});
            skLineSegment(sketch, "E807", {"start": v(17.44, 8.13) * mm, "end": v(17.1, 8.13) * mm});
            skLineSegment(sketch, "E808", {"start": v(17.1, 8.13) * mm, "end": v(16.76, 8.47) * mm});
            skLineSegment(sketch, "E809", {"start": v(17.44, 8.13) * mm, "end": v(17.61, 8.3) * mm});
            skLineSegment(sketch, "E810", {"start": v(17.61, 8.3) * mm, "end": v(17.61, 8.64) * mm});
            skLineSegment(sketch, "E811", {"start": v(17.61, 8.64) * mm, "end": v(17.44, 8.8) * mm});
            skLineSegment(sketch, "E812", {"start": v(17.44, 8.8) * mm, "end": v(15.92, 8.8) * mm});
            skLineSegment(sketch, "E813", {"start": v(15.92, 8.8) * mm, "end": v(15.4, 9.31) * mm});
            skLineSegment(sketch, "E814", {"start": v(15.4, 9.31) * mm, "end": v(15.4, 9.48) * mm});
            skLineSegment(sketch, "E815", {"start": v(15.4, 9.48) * mm, "end": v(14.9, 9.74) * mm});
            skLineSegment(sketch, "E816", {"start": v(14.9, 9.74) * mm, "end": v(14.73, 9.65) * mm});
            skLineSegment(sketch, "E817", {"start": v(-14.56, 7.96) * mm, "end": v(-14.73, 8.13) * mm});
            skLineSegment(sketch, "E818", {"start": v(-14.56, 7.96) * mm, "end": v(-14.4, 8.13) * mm});
            skLineSegment(sketch, "E819", {"start": v(-12.2, 7.96) * mm, "end": v(-12.2, 8.13) * mm});
            skLineSegment(sketch, "E820", {"start": v(-12.2, 8.13) * mm, "end": v(-12.36, 8.13) * mm});
            skLineSegment(sketch, "E821", {"start": v(-11.68, 7.96) * mm, "end": v(-11.18, 8.13) * mm});
            skLineSegment(sketch, "E822", {"start": v(-11, 7.96) * mm, "end": v(-11.18, 8.13) * mm});
            skLineSegment(sketch, "E823", {"start": v(-11, 7.96) * mm, "end": v(-10.84, 8.13) * mm});
            skLineSegment(sketch, "E824", {"start": v(-8.47, 7.96) * mm, "end": v(-8.47, 8.13) * mm});
            skLineSegment(sketch, "E825", {"start": v(-8.3, 7.96) * mm, "end": v(-8.47, 7.96) * mm});
            skLineSegment(sketch, "E826", {"start": v(-6.77, 7.96) * mm, "end": v(-6.94, 7.96) * mm});
            skLineSegment(sketch, "E827", {"start": v(-6.77, 7.96) * mm, "end": v(-6.77, 8.13) * mm});
            skLineSegment(sketch, "E828", {"start": v(1.02, 7.96) * mm, "end": v(1.02, 8.13) * mm});
            skLineSegment(sketch, "E829", {"start": v(1.02, 8.13) * mm, "end": v(1.35, 8.47) * mm});
            skLineSegment(sketch, "E830", {"start": v(1.35, 8.47) * mm, "end": v(1.52, 8.47) * mm});
            skLineSegment(sketch, "E831", {"start": v(1.35, 7.96) * mm, "end": v(1.7, 8.3) * mm});
            skLineSegment(sketch, "E832", {"start": v(7.45, 7.96) * mm, "end": v(7.11, 8.13) * mm});
            skLineSegment(sketch, "E833", {"start": v(7.45, 7.96) * mm, "end": v(7.62, 8.13) * mm});
            skLineSegment(sketch, "E834", {"start": v(8.13, 7.96) * mm, "end": v(7.96, 8.13) * mm});
            skLineSegment(sketch, "E835", {"start": v(8.13, 7.96) * mm, "end": v(8.47, 8.3) * mm});
            skLineSegment(sketch, "E836", {"start": v(11.51, 7.96) * mm, "end": v(10, 9.48) * mm});
            skLineSegment(sketch, "E837", {"start": v(11.68, 7.96) * mm, "end": v(11.51, 7.96) * mm});
            skLineSegment(sketch, "E838", {"start": v(11.85, 7.96) * mm, "end": v(11.68, 7.96) * mm});
            skLineSegment(sketch, "E839", {"start": v(12.02, 7.96) * mm, "end": v(11.85, 7.96) * mm});
            skLineSegment(sketch, "E840", {"start": v(12.02, 7.96) * mm, "end": v(12.2, 8.13) * mm});
            skLineSegment(sketch, "E841", {"start": v(12.2, 8.13) * mm, "end": v(12.53, 8.13) * mm});
            skLineSegment(sketch, "E842", {"start": v(14.73, 7.96) * mm, "end": v(14.56, 7.96) * mm});
            skLineSegment(sketch, "E843", {"start": v(14.56, 7.96) * mm, "end": v(14.56, 8.13) * mm});
            skLineSegment(sketch, "E844", {"start": v(14.9, 7.96) * mm, "end": v(14.73, 7.96) * mm});
            skLineSegment(sketch, "E845", {"start": v(14.9, 7.96) * mm, "end": v(15.24, 8.13) * mm});
            skLineSegment(sketch, "E846", {"start": v(15.24, 8.13) * mm, "end": v(15.4, 8.47) * mm});
            skLineSegment(sketch, "E847", {"start": v(15.4, 8.47) * mm, "end": v(15.24, 8.64) * mm});
            skLineSegment(sketch, "E848", {"start": v(15.24, 8.64) * mm, "end": v(14.9, 8.64) * mm});
            skLineSegment(sketch, "E849", {"start": v(17.44, 8.13) * mm, "end": v(17.61, 7.96) * mm});
            skLineSegment(sketch, "E850", {"start": v(17.61, 7.96) * mm, "end": v(17.95, 7.96) * mm});
            skLineSegment(sketch, "E851", {"start": v(17.95, 7.96) * mm, "end": v(18.12, 8.13) * mm});
            skLineSegment(sketch, "E852", {"start": v(18.12, 8.13) * mm, "end": v(18.12, 8.8) * mm});
            skLineSegment(sketch, "E853", {"start": v(18.12, 8.8) * mm, "end": v(17.78, 9.14) * mm});
            skLineSegment(sketch, "E854", {"start": v(17.78, 9.14) * mm, "end": v(17.43, 9.25) * mm});
            skLineSegment(sketch, "E855", {"start": v(17.43, 9.25) * mm, "end": v(16.6, 9.48) * mm});
            skLineSegment(sketch, "E856", {"start": v(16.6, 9.48) * mm, "end": v(16.29, 10) * mm});
            skLineSegment(sketch, "E857", {"start": v(16.29, 10) * mm, "end": v(15.75, 10.67) * mm});
            skLineSegment(sketch, "E858", {"start": v(15.75, 10.67) * mm, "end": v(14.56, 10.84) * mm});
            skLineSegment(sketch, "E859", {"start": v(-14.9, 7.79) * mm, "end": v(-14.73, 8.13) * mm});
            skLineSegment(sketch, "E860", {"start": v(-7.79, 7.79) * mm, "end": v(-7.79, 8.3) * mm});
            skLineSegment(sketch, "E861", {"start": v(-7.79, 8.3) * mm, "end": v(-7.96, 8.47) * mm});
            skLineSegment(sketch, "E862", {"start": v(-7.28, 7.79) * mm, "end": v(-7.45, 7.96) * mm});
            skLineSegment(sketch, "E863", {"start": v(-7.45, 7.96) * mm, "end": v(-7.28, 8.3) * mm});
            skLineSegment(sketch, "E864", {"start": v(-7.28, 7.79) * mm, "end": v(-6.94, 7.96) * mm});
            skLineSegment(sketch, "E865", {"start": v(0.85, 7.79) * mm, "end": v(1.02, 7.96) * mm});
            skLineSegment(sketch, "E866", {"start": v(1.19, 7.79) * mm, "end": v(1.02, 7.96) * mm});
            skLineSegment(sketch, "E867", {"start": v(1.35, 7.79) * mm, "end": v(1.19, 7.79) * mm});
            skLineSegment(sketch, "E868", {"start": v(1.35, 7.79) * mm, "end": v(1.35, 7.96) * mm});
            skLineSegment(sketch, "E869", {"start": v(7.62, 7.79) * mm, "end": v(7.45, 7.96) * mm});
            skLineSegment(sketch, "E870", {"start": v(7.79, 7.79) * mm, "end": v(7.62, 7.79) * mm});
            skLineSegment(sketch, "E871", {"start": v(7.96, 7.79) * mm, "end": v(7.79, 7.79) * mm});
            skLineSegment(sketch, "E872", {"start": v(7.96, 7.79) * mm, "end": v(8.13, 7.96) * mm});
            skLineSegment(sketch, "E873", {"start": v(8.64, 7.79) * mm, "end": v(8.8, 7.96) * mm});
            skLineSegment(sketch, "E874", {"start": v(8.8, 7.96) * mm, "end": v(8.64, 8.3) * mm});
            skLineSegment(sketch, "E875", {"start": v(11.51, 7.79) * mm, "end": v(11.51, 7.96) * mm});
            skLineSegment(sketch, "E876", {"start": v(12.02, 7.79) * mm, "end": v(12.02, 7.96) * mm});
            skLineSegment(sketch, "E877", {"start": v(14.9, 7.79) * mm, "end": v(14.9, 7.96) * mm});
            skLineSegment(sketch, "E878", {"start": v(-15.07, 7.62) * mm, "end": v(-14.9, 7.79) * mm});
            skLineSegment(sketch, "E879", {"start": v(-14.73, 7.62) * mm, "end": v(-14.9, 7.79) * mm});
            skLineSegment(sketch, "E880", {"start": v(-14.73, 7.62) * mm, "end": v(-14.56, 7.96) * mm});
            skLineSegment(sketch, "E881", {"start": v(-7.96, 7.62) * mm, "end": v(-8.3, 7.96) * mm});
            skLineSegment(sketch, "E882", {"start": v(-7.96, 7.62) * mm, "end": v(-7.79, 7.79) * mm});
            skLineSegment(sketch, "E883", {"start": v(-7.62, 7.62) * mm, "end": v(-7.79, 7.79) * mm});
            skLineSegment(sketch, "E884", {"start": v(-7.45, 7.62) * mm, "end": v(-7.62, 7.62) * mm});
            skLineSegment(sketch, "E885", {"start": v(-7.28, 7.62) * mm, "end": v(-7.45, 7.62) * mm});
            skLineSegment(sketch, "E886", {"start": v(-7.28, 7.62) * mm, "end": v(-7.28, 7.79) * mm});
            skLineSegment(sketch, "E887", {"start": v(1.02, 7.62) * mm, "end": v(0.85, 7.79) * mm});
            skLineSegment(sketch, "E888", {"start": v(1.19, 7.62) * mm, "end": v(1.02, 7.62) * mm});
            skLineSegment(sketch, "E889", {"start": v(1.19, 7.62) * mm, "end": v(1.19, 7.79) * mm});
            skLineSegment(sketch, "E890", {"start": v(6.94, 7.62) * mm, "end": v(6.77, 7.79) * mm});
            skLineSegment(sketch, "E891", {"start": v(6.77, 7.79) * mm, "end": v(6.94, 8.13) * mm});
            skLineSegment(sketch, "E892", {"start": v(7.11, 7.62) * mm, "end": v(6.94, 7.62) * mm});
            skLineSegment(sketch, "E893", {"start": v(7.11, 7.62) * mm, "end": v(7.45, 7.96) * mm});
            skLineSegment(sketch, "E894", {"start": v(7.62, 7.62) * mm, "end": v(7.62, 7.79) * mm});
            skLineSegment(sketch, "E895", {"start": v(7.96, 7.62) * mm, "end": v(7.96, 7.79) * mm});
            skLineSegment(sketch, "E896", {"start": v(8.47, 7.62) * mm, "end": v(8.13, 7.96) * mm});
            skLineSegment(sketch, "E897", {"start": v(8.64, 7.62) * mm, "end": v(8.47, 7.62) * mm});
            skLineSegment(sketch, "E898", {"start": v(8.64, 7.62) * mm, "end": v(8.64, 7.79) * mm});
            skLineSegment(sketch, "E899", {"start": v(11.35, 7.62) * mm, "end": v(11.51, 7.79) * mm});
            skLineSegment(sketch, "E900", {"start": v(11.68, 7.62) * mm, "end": v(11.51, 7.79) * mm});
            skLineSegment(sketch, "E901", {"start": v(11.85, 7.62) * mm, "end": v(11.68, 7.62) * mm});
            skLineSegment(sketch, "E902", {"start": v(12.02, 7.62) * mm, "end": v(11.85, 7.62) * mm});
            skLineSegment(sketch, "E903", {"start": v(12.02, 7.62) * mm, "end": v(12.02, 7.79) * mm});
            skLineSegment(sketch, "E904", {"start": v(-14.9, 7.45) * mm, "end": v(-15.07, 7.62) * mm});
            skLineSegment(sketch, "E905", {"start": v(-14.9, 7.45) * mm, "end": v(-14.73, 7.62) * mm});
            skLineSegment(sketch, "E906", {"start": v(-12.36, 8.13) * mm, "end": v(-12.7, 8.13) * mm});
            skLineSegment(sketch, "E907", {"start": v(-12.7, 8.13) * mm, "end": v(-12.87, 7.96) * mm});
            skLineSegment(sketch, "E908", {"start": v(-12.87, 7.96) * mm, "end": v(-12.87, 7.62) * mm});
            skLineSegment(sketch, "E909", {"start": v(-12.87, 7.62) * mm, "end": v(-12.53, 7.45) * mm});
            skLineSegment(sketch, "E910", {"start": v(-12.53, 7.45) * mm, "end": v(-12.2, 7.79) * mm});
            skLineSegment(sketch, "E911", {"start": v(-12.2, 7.79) * mm, "end": v(-12.2, 7.96) * mm});
            skLineSegment(sketch, "E912", {"start": v(-7.62, 7.45) * mm, "end": v(-7.62, 7.62) * mm});
            skLineSegment(sketch, "E913", {"start": v(-6.77, 7.45) * mm, "end": v(-6.6, 7.62) * mm});
            skLineSegment(sketch, "E914", {"start": v(-6.6, 7.62) * mm, "end": v(-6.77, 7.96) * mm});
            skLineSegment(sketch, "E915", {"start": v(-1.19, 7.45) * mm, "end": v(-1.86, 8.13) * mm});
            skLineSegment(sketch, "E916", {"start": v(-0.68, 7.45) * mm, "end": v(-1.02, 7.96) * mm});
            skLineSegment(sketch, "E917", {"start": v(-1.02, 7.96) * mm, "end": v(-1.34, 8.16) * mm});
            skLineSegment(sketch, "E918", {"start": v(-1.34, 8.16) * mm, "end": v(-1.7, 8.3) * mm});
            skLineSegment(sketch, "E919", {"start": v(0.5, 7.45) * mm, "end": v(0.85, 7.79) * mm});
            skLineSegment(sketch, "E920", {"start": v(1.02, 7.45) * mm, "end": v(1.02, 7.62) * mm});
            skLineSegment(sketch, "E921", {"start": v(1.35, 7.45) * mm, "end": v(1.19, 7.62) * mm});
            skLineSegment(sketch, "E922", {"start": v(1.35, 7.45) * mm, "end": v(1.52, 7.62) * mm});
            skLineSegment(sketch, "E923", {"start": v(1.52, 7.62) * mm, "end": v(1.35, 7.79) * mm});
            skLineSegment(sketch, "E924", {"start": v(7.11, 7.45) * mm, "end": v(7.11, 7.62) * mm});
            skLineSegment(sketch, "E925", {"start": v(8.64, 7.45) * mm, "end": v(8.64, 7.62) * mm});
            skLineSegment(sketch, "E926", {"start": v(11.35, 7.45) * mm, "end": v(11.35, 7.62) * mm});
            skLineSegment(sketch, "E927", {"start": v(11.51, 7.45) * mm, "end": v(11.35, 7.45) * mm});
            skLineSegment(sketch, "E928", {"start": v(11.68, 7.45) * mm, "end": v(11.51, 7.45) * mm});
            skLineSegment(sketch, "E929", {"start": v(11.68, 7.45) * mm, "end": v(11.68, 7.62) * mm});
            skLineSegment(sketch, "E930", {"start": v(12.02, 7.45) * mm, "end": v(12.02, 7.62) * mm});
            skLineSegment(sketch, "E931", {"start": v(-8.47, 7.28) * mm, "end": v(-8.64, 7.45) * mm});
            skLineSegment(sketch, "E932", {"start": v(-8.64, 7.45) * mm, "end": v(-8.64, 7.79) * mm});
            skLineSegment(sketch, "E933", {"start": v(-8.64, 7.79) * mm, "end": v(-8.47, 7.96) * mm});
            skLineSegment(sketch, "E934", {"start": v(-8.3, 7.28) * mm, "end": v(-8.47, 7.28) * mm});
            skLineSegment(sketch, "E935", {"start": v(-8.3, 7.28) * mm, "end": v(-7.96, 7.62) * mm});
            skLineSegment(sketch, "E936", {"start": v(-6.94, 7.28) * mm, "end": v(-7.28, 7.62) * mm});
            skLineSegment(sketch, "E937", {"start": v(-6.77, 7.28) * mm, "end": v(-6.94, 7.28) * mm});
            skLineSegment(sketch, "E938", {"start": v(-6.77, 7.28) * mm, "end": v(-6.77, 7.45) * mm});
            skLineSegment(sketch, "E939", {"start": v(-1.19, 7.28) * mm, "end": v(-1.19, 7.45) * mm});
            skLineSegment(sketch, "E940", {"start": v(-1.02, 7.28) * mm, "end": v(-1.19, 7.28) * mm});
            skLineSegment(sketch, "E941", {"start": v(-0.68, 7.28) * mm, "end": v(-0.68, 7.45) * mm});
            skLineSegment(sketch, "E942", {"start": v(-0.5, 7.28) * mm, "end": v(-0.68, 7.28) * mm});
            skLineSegment(sketch, "E943", {"start": v(0.5, 7.28) * mm, "end": v(0.34, 7.28) * mm});
            skLineSegment(sketch, "E944", {"start": v(0.5, 7.28) * mm, "end": v(0.5, 7.45) * mm});
            skLineSegment(sketch, "E945", {"start": v(0.68, 7.28) * mm, "end": v(0.5, 7.28) * mm});
            skLineSegment(sketch, "E946", {"start": v(0.85, 7.28) * mm, "end": v(0.68, 7.28) * mm});
            skLineSegment(sketch, "E947", {"start": v(1.02, 7.28) * mm, "end": v(0.85, 7.28) * mm});
            skLineSegment(sketch, "E948", {"start": v(1.02, 7.28) * mm, "end": v(1.02, 7.45) * mm});
            skLineSegment(sketch, "E949", {"start": v(1.35, 7.28) * mm, "end": v(1.35, 7.45) * mm});
            skLineSegment(sketch, "E950", {"start": v(7.45, 7.28) * mm, "end": v(7.62, 7.62) * mm});
            skLineSegment(sketch, "E951", {"start": v(8.13, 7.28) * mm, "end": v(7.96, 7.62) * mm});
            skLineSegment(sketch, "E952", {"start": v(8.64, 7.28) * mm, "end": v(8.64, 7.45) * mm});
            skLineSegment(sketch, "E953", {"start": v(11.35, 7.28) * mm, "end": v(11.35, 7.45) * mm});
            skLineSegment(sketch, "E954", {"start": v(11.85, 7.28) * mm, "end": v(11.68, 7.45) * mm});
            skLineSegment(sketch, "E955", {"start": v(12.02, 7.28) * mm, "end": v(11.85, 7.28) * mm});
            skLineSegment(sketch, "E956", {"start": v(12.02, 7.28) * mm, "end": v(12.02, 7.45) * mm});
            skLineSegment(sketch, "E957", {"start": v(-8.47, 7.11) * mm, "end": v(-8.47, 7.28) * mm});
            skLineSegment(sketch, "E958", {"start": v(-7.45, 7.11) * mm, "end": v(-7.62, 7.45) * mm});
            skLineSegment(sketch, "E959", {"start": v(-6.77, 7.11) * mm, "end": v(-6.77, 7.28) * mm});
            skLineSegment(sketch, "E960", {"start": v(-1.19, 7.11) * mm, "end": v(-1.19, 7.28) * mm});
            skLineSegment(sketch, "E961", {"start": v(-1.02, 7.28) * mm, "end": v(-0.85, 7.11) * mm});
            skLineSegment(sketch, "E962", {"start": v(-0.85, 7.11) * mm, "end": v(-0.68, 7.28) * mm});
            skLineSegment(sketch, "E963", {"start": v(-0.34, 7.11) * mm, "end": v(-0.5, 7.28) * mm});
            skLineSegment(sketch, "E964", {"start": v(-0.17, 7.11) * mm, "end": v(-0.34, 7.11) * mm});
            skLineSegment(sketch, "E965", {"start": v(0, 7.11) * mm, "end": v(-0.17, 7.11) * mm});
            skLineSegment(sketch, "E966", {"start": v(0, 7.11) * mm, "end": v(0.34, 7.28) * mm});
            skLineSegment(sketch, "E967", {"start": v(1.19, 7.11) * mm, "end": v(1.02, 7.28) * mm});
            skLineSegment(sketch, "E968", {"start": v(1.19, 7.11) * mm, "end": v(1.35, 7.28) * mm});
            skLineSegment(sketch, "E969", {"start": v(7.28, 7.11) * mm, "end": v(7.11, 7.11) * mm});
            skLineSegment(sketch, "E970", {"start": v(7.11, 7.11) * mm, "end": v(6.94, 7.28) * mm});
            skLineSegment(sketch, "E971", {"start": v(6.94, 7.28) * mm, "end": v(7.11, 7.45) * mm});
            skLineSegment(sketch, "E972", {"start": v(7.45, 7.11) * mm, "end": v(7.28, 7.11) * mm});
            skLineSegment(sketch, "E973", {"start": v(7.45, 7.11) * mm, "end": v(7.45, 7.28) * mm});
            skLineSegment(sketch, "E974", {"start": v(8.13, 7.11) * mm, "end": v(8.13, 7.28) * mm});
            skLineSegment(sketch, "E975", {"start": v(8.3, 7.11) * mm, "end": v(8.13, 7.11) * mm});
            skLineSegment(sketch, "E976", {"start": v(8.47, 7.11) * mm, "end": v(8.3, 7.11) * mm});
            skLineSegment(sketch, "E977", {"start": v(8.47, 7.11) * mm, "end": v(8.64, 7.11) * mm});
            skLineSegment(sketch, "E978", {"start": v(8.64, 7.11) * mm, "end": v(8.64, 7.28) * mm});
            skLineSegment(sketch, "E979", {"start": v(11.35, 7.11) * mm, "end": v(11.35, 7.28) * mm});
            skLineSegment(sketch, "E980", {"start": v(11.51, 7.11) * mm, "end": v(11.35, 7.11) * mm});
            skLineSegment(sketch, "E981", {"start": v(11.68, 7.11) * mm, "end": v(11.51, 7.11) * mm});
            skLineSegment(sketch, "E982", {"start": v(11.68, 7.11) * mm, "end": v(11.85, 7.28) * mm});
            skLineSegment(sketch, "E983", {"start": v(12.02, 7.11) * mm, "end": v(12.02, 7.28) * mm});
            skLineSegment(sketch, "E984", {"start": v(22.7, 7.11) * mm, "end": v(22.52, 10.5) * mm});
            skLineSegment(sketch, "E985", {"start": v(23.37, 7.11) * mm, "end": v(23.12, 10.5) * mm});
            skLineSegment(sketch, "E986", {"start": v(23.12, 10.5) * mm, "end": v(22.98, 10.99) * mm});
            skLineSegment(sketch, "E987", {"start": v(22.98, 10.99) * mm, "end": v(22.7, 11.51) * mm});
            skLineSegment(sketch, "E988", {"start": v(-14.73, 6.94) * mm, "end": v(-14.9, 7.45) * mm});
            skLineSegment(sketch, "E989", {"start": v(-14.05, 6.94) * mm, "end": v(-14.05, 8.13) * mm});
            skLineSegment(sketch, "E990", {"start": v(-8.3, 6.94) * mm, "end": v(-8.47, 6.94) * mm});
            skLineSegment(sketch, "E991", {"start": v(-8.47, 6.94) * mm, "end": v(-8.47, 7.11) * mm});
            skLineSegment(sketch, "E992", {"start": v(-8.13, 6.94) * mm, "end": v(-8.3, 6.94) * mm});
            skLineSegment(sketch, "E993", {"start": v(-7.96, 6.94) * mm, "end": v(-8.13, 6.94) * mm});
            skLineSegment(sketch, "E994", {"start": v(-7.96, 6.94) * mm, "end": v(-7.62, 7.45) * mm});
            skLineSegment(sketch, "E995", {"start": v(-7.45, 6.94) * mm, "end": v(-7.45, 7.11) * mm});
            skLineSegment(sketch, "E996", {"start": v(-7.28, 6.94) * mm, "end": v(-7.45, 6.94) * mm});
            skLineSegment(sketch, "E997", {"start": v(-6.94, 6.94) * mm, "end": v(-7.28, 6.94) * mm});
            skLineSegment(sketch, "E998", {"start": v(-6.94, 6.94) * mm, "end": v(-6.77, 6.94) * mm});
            skLineSegment(sketch, "E999", {"start": v(-6.77, 6.94) * mm, "end": v(-6.77, 7.11) * mm});
            skLineSegment(sketch, "E1000", {"start": v(-1.7, 6.94) * mm, "end": v(-1.7, 7.11) * mm});
            skLineSegment(sketch, "E1001", {"start": v(-1.7, 7.11) * mm, "end": v(-2.03, 7.45) * mm});
            skLineSegment(sketch, "E1002", {"start": v(-0.17, 6.94) * mm, "end": v(-0.17, 7.11) * mm});
            skLineSegment(sketch, "E1003", {"start": v(1.52, 6.94) * mm, "end": v(1.35, 7.28) * mm});
            skLineSegment(sketch, "E1004", {"start": v(7.45, 7.11) * mm, "end": v(7.62, 6.94) * mm});
            skLineSegment(sketch, "E1005", {"start": v(7.62, 6.94) * mm, "end": v(7.96, 6.94) * mm});
            skLineSegment(sketch, "E1006", {"start": v(7.96, 6.94) * mm, "end": v(8.13, 7.11) * mm});
            skLineSegment(sketch, "E1007", {"start": v(11.35, 6.94) * mm, "end": v(11.35, 7.11) * mm});
            skLineSegment(sketch, "E1008", {"start": v(11.85, 6.94) * mm, "end": v(11.68, 7.11) * mm});
            skLineSegment(sketch, "E1009", {"start": v(12.02, 6.94) * mm, "end": v(11.85, 6.94) * mm});
            skLineSegment(sketch, "E1010", {"start": v(12.02, 6.94) * mm, "end": v(12.02, 7.11) * mm});
            skLineSegment(sketch, "E1011", {"start": v(22.7, 6.94) * mm, "end": v(22.7, 7.11) * mm});
            skLineSegment(sketch, "E1012", {"start": v(22.86, 6.94) * mm, "end": v(22.7, 6.94) * mm});
            skLineSegment(sketch, "E1013", {"start": v(23.2, 6.94) * mm, "end": v(22.86, 6.94) * mm});
            skLineSegment(sketch, "E1014", {"start": v(23.37, 6.94) * mm, "end": v(23.2, 6.94) * mm});
            skLineSegment(sketch, "E1015", {"start": v(23.37, 6.94) * mm, "end": v(23.37, 7.11) * mm});
            skLineSegment(sketch, "E1016", {"start": v(-14.9, 6.77) * mm, "end": v(-14.73, 6.94) * mm});
            skLineSegment(sketch, "E1017", {"start": v(-7.96, 6.77) * mm, "end": v(-7.96, 6.94) * mm});
            skLineSegment(sketch, "E1018", {"start": v(-7.45, 6.77) * mm, "end": v(-7.45, 6.94) * mm});
            skLineSegment(sketch, "E1019", {"start": v(-1.7, 6.77) * mm, "end": v(-1.7, 6.94) * mm});
            skLineSegment(sketch, "E1020", {"start": v(-1.52, 6.77) * mm, "end": v(-1.7, 6.77) * mm});
            skLineSegment(sketch, "E1021", {"start": v(-1.52, 6.77) * mm, "end": v(-1.35, 6.77) * mm});
            skLineSegment(sketch, "E1022", {"start": v(-1.35, 6.77) * mm, "end": v(-1.19, 7.11) * mm});
            skLineSegment(sketch, "E1023", {"start": v(-0.17, 6.77) * mm, "end": v(-0.17, 6.94) * mm});
            skLineSegment(sketch, "E1024", {"start": v(0, 6.77) * mm, "end": v(-0.17, 6.77) * mm});
            skLineSegment(sketch, "E1025", {"start": v(1.35, 6.77) * mm, "end": v(1.19, 7.11) * mm});
            skLineSegment(sketch, "E1026", {"start": v(1.52, 6.77) * mm, "end": v(1.35, 6.77) * mm});
            skLineSegment(sketch, "E1027", {"start": v(1.52, 6.77) * mm, "end": v(1.52, 6.94) * mm});
            skLineSegment(sketch, "E1028", {"start": v(11.35, 6.77) * mm, "end": v(11.35, 6.94) * mm});
            skLineSegment(sketch, "E1029", {"start": v(11.51, 6.77) * mm, "end": v(11.35, 6.77) * mm});
            skLineSegment(sketch, "E1030", {"start": v(11.51, 6.77) * mm, "end": v(11.85, 6.94) * mm});
            skLineSegment(sketch, "E1031", {"start": v(12.02, 6.77) * mm, "end": v(12.02, 6.94) * mm});
            skLineSegment(sketch, "E1032", {"start": v(22.7, 6.77) * mm, "end": v(22.7, 6.94) * mm});
            skLineSegment(sketch, "E1033", {"start": v(23.37, 6.77) * mm, "end": v(23.37, 6.94) * mm});
            skLineSegment(sketch, "E1034", {"start": v(-14.9, 6.6) * mm, "end": v(-15.07, 6.6) * mm});
            skLineSegment(sketch, "E1035", {"start": v(-14.9, 6.6) * mm, "end": v(-14.9, 6.77) * mm});
            skLineSegment(sketch, "E1036", {"start": v(-11.68, 6.6) * mm, "end": v(-11, 7.96) * mm});
            skLineSegment(sketch, "E1037", {"start": v(-7.96, 6.77) * mm, "end": v(-7.79, 6.6) * mm});
            skLineSegment(sketch, "E1038", {"start": v(-7.79, 6.6) * mm, "end": v(-7.45, 6.77) * mm});
            skLineSegment(sketch, "E1039", {"start": v(-0.17, 6.6) * mm, "end": v(-0.17, 6.77) * mm});
            skLineSegment(sketch, "E1040", {"start": v(11.35, 6.6) * mm, "end": v(11.35, 6.77) * mm});
            skLineSegment(sketch, "E1041", {"start": v(12.02, 6.6) * mm, "end": v(12.02, 6.77) * mm});
            skLineSegment(sketch, "E1042", {"start": v(23.37, 6.6) * mm, "end": v(23.37, 6.77) * mm});
            skLineSegment(sketch, "E1043", {"start": v(-14.9, 6.43) * mm, "end": v(-14.9, 6.6) * mm});
            skLineSegment(sketch, "E1044", {"start": v(-11.68, 6.43) * mm, "end": v(-11.68, 6.6) * mm});
            skLineSegment(sketch, "E1045", {"start": v(-11.51, 6.43) * mm, "end": v(-11.68, 6.43) * mm});
            skLineSegment(sketch, "E1046", {"start": v(11.35, 6.43) * mm, "end": v(11.35, 6.6) * mm});
            skLineSegment(sketch, "E1047", {"start": v(11.51, 6.43) * mm, "end": v(11.35, 6.43) * mm});
            skLineSegment(sketch, "E1048", {"start": v(11.85, 6.43) * mm, "end": v(11.51, 6.43) * mm});
            skLineSegment(sketch, "E1049", {"start": v(12.02, 6.43) * mm, "end": v(11.85, 6.43) * mm});
            skLineSegment(sketch, "E1050", {"start": v(12.02, 6.43) * mm, "end": v(12.02, 6.6) * mm});
            skLineSegment(sketch, "E1051", {"start": v(22.86, 6.43) * mm, "end": v(22.7, 6.77) * mm});
            skLineSegment(sketch, "E1052", {"start": v(23.03, 6.43) * mm, "end": v(22.86, 6.43) * mm});
            skLineSegment(sketch, "E1053", {"start": v(23.2, 6.43) * mm, "end": v(23.03, 6.43) * mm});
            skLineSegment(sketch, "E1054", {"start": v(23.37, 6.43) * mm, "end": v(23.2, 6.43) * mm});
            skLineSegment(sketch, "E1055", {"start": v(23.37, 6.43) * mm, "end": v(23.37, 6.6) * mm});
            skLineSegment(sketch, "E1056", {"start": v(-22.86, 6.27) * mm, "end": v(-22.46, 8.28) * mm});
            skLineSegment(sketch, "E1057", {"start": v(-22.46, 8.28) * mm, "end": v(-21.81, 10.31) * mm});
            skLineSegment(sketch, "E1058", {"start": v(-21.81, 10.31) * mm, "end": v(-21.34, 11.18) * mm});
            skLineSegment(sketch, "E1059", {"start": v(-15.07, 6.27) * mm, "end": v(-15.24, 6.27) * mm});
            skLineSegment(sketch, "E1060", {"start": v(-15.24, 6.27) * mm, "end": v(-15.4, 6.43) * mm});
            skLineSegment(sketch, "E1061", {"start": v(-15.4, 6.43) * mm, "end": v(-15.07, 6.6) * mm});
            skLineSegment(sketch, "E1062", {"start": v(-14.9, 6.27) * mm, "end": v(-15.07, 6.27) * mm});
            skLineSegment(sketch, "E1063", {"start": v(-14.9, 6.27) * mm, "end": v(-14.9, 6.43) * mm});
            skLineSegment(sketch, "E1064", {"start": v(-14.73, 6.27) * mm, "end": v(-14.9, 6.27) * mm});
            skLineSegment(sketch, "E1065", {"start": v(-14.56, 6.27) * mm, "end": v(-14.73, 6.27) * mm});
            skLineSegment(sketch, "E1066", {"start": v(-14.56, 6.27) * mm, "end": v(-14.4, 6.43) * mm});
            skLineSegment(sketch, "E1067", {"start": v(-14.4, 6.43) * mm, "end": v(-14.4, 6.6) * mm});
            skLineSegment(sketch, "E1068", {"start": v(-14.4, 6.6) * mm, "end": v(-14.73, 6.94) * mm});
            skLineSegment(sketch, "E1069", {"start": v(-11.68, 6.27) * mm, "end": v(-11.68, 6.43) * mm});
            skLineSegment(sketch, "E1070", {"start": v(0.34, 6.27) * mm, "end": v(0, 6.77) * mm});
            skLineSegment(sketch, "E1071", {"start": v(0.5, 6.27) * mm, "end": v(0.34, 6.27) * mm});
            skLineSegment(sketch, "E1072", {"start": v(0.68, 6.27) * mm, "end": v(0.5, 6.27) * mm});
            skLineSegment(sketch, "E1073", {"start": v(0.85, 6.27) * mm, "end": v(0.68, 6.27) * mm});
            skLineSegment(sketch, "E1074", {"start": v(1.02, 6.27) * mm, "end": v(0.85, 6.27) * mm});
            skLineSegment(sketch, "E1075", {"start": v(11.35, 6.27) * mm, "end": v(11.35, 6.43) * mm});
            skLineSegment(sketch, "E1076", {"start": v(12.2, 6.27) * mm, "end": v(12.02, 6.43) * mm});
            skLineSegment(sketch, "E1077", {"start": v(22.86, 6.27) * mm, "end": v(22.86, 6.43) * mm});
            skLineSegment(sketch, "E1078", {"start": v(23.37, 6.27) * mm, "end": v(23.37, 6.43) * mm});
            skLineSegment(sketch, "E1079", {"start": v(-22.86, 6.1) * mm, "end": v(-22.86, 6.27) * mm});
            skLineSegment(sketch, "E1080", {"start": v(-22.7, 6.1) * mm, "end": v(-22.86, 6.1) * mm});
            skLineSegment(sketch, "E1081", {"start": v(-21.84, 6.1) * mm, "end": v(-22.01, 6.27) * mm});
            skLineSegment(sketch, "E1082", {"start": v(-22.01, 6.27) * mm, "end": v(-22.18, 6.1) * mm});
            skLineSegment(sketch, "E1083", {"start": v(-21.84, 6.1) * mm, "end": v(-21.75, 6.28) * mm});
            skLineSegment(sketch, "E1084", {"start": v(-21.75, 6.28) * mm, "end": v(-21.17, 10.16) * mm});
            skLineSegment(sketch, "E1085", {"start": v(-21.17, 10.16) * mm, "end": v(-21, 10.33) * mm});
            skLineSegment(sketch, "E1086", {"start": v(-21, 10.33) * mm, "end": v(-19.47, 10.16) * mm});
            skLineSegment(sketch, "E1087", {"start": v(-19.47, 10.16) * mm, "end": v(-18.63, 10.84) * mm});
            skLineSegment(sketch, "E1088", {"start": v(-18.63, 10.84) * mm, "end": v(-18.46, 11.68) * mm});
            skLineSegment(sketch, "E1089", {"start": v(-18.46, 11.68) * mm, "end": v(-18.8, 12.36) * mm});
            skLineSegment(sketch, "E1090", {"start": v(-14.56, 6.1) * mm, "end": v(-14.56, 6.27) * mm});
            skLineSegment(sketch, "E1091", {"start": v(-11.68, 6.1) * mm, "end": v(-11.68, 6.27) * mm});
            skLineSegment(sketch, "E1092", {"start": v(-0.85, 6.1) * mm, "end": v(-1.02, 6.1) * mm});
            skLineSegment(sketch, "E1093", {"start": v(-0.68, 6.1) * mm, "end": v(-0.85, 6.1) * mm});
            skLineSegment(sketch, "E1094", {"start": v(-0.5, 6.1) * mm, "end": v(-0.68, 6.1) * mm});
            skLineSegment(sketch, "E1095", {"start": v(-0.5, 6.1) * mm, "end": v(-0.17, 6.6) * mm});
            skLineSegment(sketch, "E1096", {"start": v(0.5, 6.1) * mm, "end": v(0.5, 6.27) * mm});
            skLineSegment(sketch, "E1097", {"start": v(0.85, 6.1) * mm, "end": v(0.85, 6.27) * mm});
            skLineSegment(sketch, "E1098", {"start": v(11.18, 6.1) * mm, "end": v(11.35, 6.27) * mm});
            skLineSegment(sketch, "E1099", {"start": v(11.51, 6.1) * mm, "end": v(11.35, 6.27) * mm});
            skLineSegment(sketch, "E1100", {"start": v(12.02, 6.1) * mm, "end": v(11.51, 6.1) * mm});
            skLineSegment(sketch, "E1101", {"start": v(12.2, 6.1) * mm, "end": v(12.02, 6.1) * mm});
            skLineSegment(sketch, "E1102", {"start": v(12.2, 6.1) * mm, "end": v(12.2, 6.27) * mm});
            skLineSegment(sketch, "E1103", {"start": v(22.7, 6.1) * mm, "end": v(22.86, 6.27) * mm});
            skLineSegment(sketch, "E1104", {"start": v(23.54, 6.1) * mm, "end": v(23.37, 6.27) * mm});
            skLineSegment(sketch, "E1105", {"start": v(-22.86, 5.93) * mm, "end": v(-22.86, 6.1) * mm});
            skLineSegment(sketch, "E1106", {"start": v(-22.35, 5.93) * mm, "end": v(-22.7, 6.1) * mm});
            skLineSegment(sketch, "E1107", {"start": v(-22.18, 5.93) * mm, "end": v(-22.35, 5.93) * mm});
            skLineSegment(sketch, "E1108", {"start": v(-22.18, 5.93) * mm, "end": v(-22.18, 6.1) * mm});
            skLineSegment(sketch, "E1109", {"start": v(-22.01, 5.93) * mm, "end": v(-22.18, 5.93) * mm});
            skLineSegment(sketch, "E1110", {"start": v(-21.84, 5.93) * mm, "end": v(-22.01, 5.93) * mm});
            skLineSegment(sketch, "E1111", {"start": v(-21.84, 5.93) * mm, "end": v(-21.84, 6.1) * mm});
            skLineSegment(sketch, "E1112", {"start": v(-17.61, 5.93) * mm, "end": v(-16.75, 6.23) * mm});
            skLineSegment(sketch, "E1113", {"start": v(-16.75, 6.23) * mm, "end": v(-15.58, 7.79) * mm});
            skLineSegment(sketch, "E1114", {"start": v(-15.58, 7.79) * mm, "end": v(-15.07, 7.62) * mm});
            skLineSegment(sketch, "E1115", {"start": v(-11.51, 5.93) * mm, "end": v(-11.68, 6.1) * mm});
            skLineSegment(sketch, "E1116", {"start": v(-11.18, 5.93) * mm, "end": v(-11.18, 6.1) * mm});
            skLineSegment(sketch, "E1117", {"start": v(-11.18, 6.1) * mm, "end": v(-11.51, 6.43) * mm});
            skLineSegment(sketch, "E1118", {"start": v(-3.22, 5.93) * mm, "end": v(-1.7, 6.77) * mm});
            skLineSegment(sketch, "E1119", {"start": v(-1.35, 5.93) * mm, "end": v(-1.02, 6.1) * mm});
            skLineSegment(sketch, "E1120", {"start": v(-0.85, 5.93) * mm, "end": v(-0.85, 6.1) * mm});
            skLineSegment(sketch, "E1121", {"start": v(-0.5, 5.93) * mm, "end": v(-0.5, 6.1) * mm});
            skLineSegment(sketch, "E1122", {"start": v(0.5, 5.93) * mm, "end": v(0.5, 6.1) * mm});
            skLineSegment(sketch, "E1123", {"start": v(0.85, 5.93) * mm, "end": v(0.85, 6.1) * mm});
            skLineSegment(sketch, "E1124", {"start": v(1.19, 5.93) * mm, "end": v(1.02, 6.27) * mm});
            skLineSegment(sketch, "E1125", {"start": v(11.18, 5.93) * mm, "end": v(11.18, 6.1) * mm});
            skLineSegment(sketch, "E1126", {"start": v(11.35, 5.93) * mm, "end": v(11.18, 5.93) * mm});
            skLineSegment(sketch, "E1127", {"start": v(11.35, 5.93) * mm, "end": v(11.51, 6.1) * mm});
            skLineSegment(sketch, "E1128", {"start": v(12.2, 5.93) * mm, "end": v(12.2, 6.1) * mm});
            skLineSegment(sketch, "E1129", {"start": v(22.7, 5.93) * mm, "end": v(22.7, 6.1) * mm});
            skLineSegment(sketch, "E1130", {"start": v(22.86, 5.93) * mm, "end": v(22.7, 5.93) * mm});
            skLineSegment(sketch, "E1131", {"start": v(23.37, 5.93) * mm, "end": v(22.86, 5.93) * mm});
            skLineSegment(sketch, "E1132", {"start": v(23.54, 5.93) * mm, "end": v(23.37, 5.93) * mm});
            skLineSegment(sketch, "E1133", {"start": v(23.54, 5.93) * mm, "end": v(23.54, 6.1) * mm});
            skLineSegment(sketch, "E1134", {"start": v(-22.18, 5.76) * mm, "end": v(-22.18, 5.93) * mm});
            skLineSegment(sketch, "E1135", {"start": v(-11.51, 5.76) * mm, "end": v(-11.51, 5.93) * mm});
            skLineSegment(sketch, "E1136", {"start": v(-11.35, 5.76) * mm, "end": v(-11.51, 5.76) * mm});
            skLineSegment(sketch, "E1137", {"start": v(-11.35, 5.76) * mm, "end": v(-11.18, 5.93) * mm});
            skLineSegment(sketch, "E1138", {"start": v(-1.35, 5.76) * mm, "end": v(-1.35, 5.93) * mm});
            skLineSegment(sketch, "E1139", {"start": v(-1.19, 5.76) * mm, "end": v(-1.35, 5.76) * mm});
            skLineSegment(sketch, "E1140", {"start": v(-1.02, 5.76) * mm, "end": v(-1.19, 5.76) * mm});
            skLineSegment(sketch, "E1141", {"start": v(-1.02, 5.76) * mm, "end": v(-0.85, 5.93) * mm});
            skLineSegment(sketch, "E1142", {"start": v(-0.5, 5.76) * mm, "end": v(-0.5, 5.93) * mm});
            skLineSegment(sketch, "E1143", {"start": v(-0.34, 5.76) * mm, "end": v(-0.5, 5.76) * mm});
            skLineSegment(sketch, "E1144", {"start": v(0.34, 5.76) * mm, "end": v(-0.34, 5.76) * mm});
            skLineSegment(sketch, "E1145", {"start": v(0.5, 5.76) * mm, "end": v(0.34, 5.76) * mm});
            skLineSegment(sketch, "E1146", {"start": v(0.5, 5.76) * mm, "end": v(0.5, 5.93) * mm});
            skLineSegment(sketch, "E1147", {"start": v(0.85, 5.76) * mm, "end": v(0.85, 5.93) * mm});
            skLineSegment(sketch, "E1148", {"start": v(1.02, 5.76) * mm, "end": v(0.85, 5.76) * mm});
            skLineSegment(sketch, "E1149", {"start": v(1.19, 5.76) * mm, "end": v(1.02, 5.76) * mm});
            skLineSegment(sketch, "E1150", {"start": v(1.19, 5.76) * mm, "end": v(1.19, 5.93) * mm});
            skLineSegment(sketch, "E1151", {"start": v(1.35, 5.76) * mm, "end": v(1.19, 5.76) * mm});
            skLineSegment(sketch, "E1152", {"start": v(5.93, 5.76) * mm, "end": v(5.93, 5.93) * mm});
            skLineSegment(sketch, "E1153", {"start": v(5.93, 5.93) * mm, "end": v(6.1, 5.93) * mm});
            skLineSegment(sketch, "E1154", {"start": v(6.27, 5.76) * mm, "end": v(6.27, 5.93) * mm});
            skLineSegment(sketch, "E1155", {"start": v(6.27, 5.93) * mm, "end": v(6.1, 5.93) * mm});
            skLineSegment(sketch, "E1156", {"start": v(11.18, 5.76) * mm, "end": v(11.18, 5.93) * mm});
            skLineSegment(sketch, "E1157", {"start": v(12.02, 5.76) * mm, "end": v(11.51, 5.76) * mm});
            skLineSegment(sketch, "E1158", {"start": v(11.51, 5.76) * mm, "end": v(11.35, 5.93) * mm});
            skLineSegment(sketch, "E1159", {"start": v(12.2, 5.76) * mm, "end": v(12.02, 5.76) * mm});
            skLineSegment(sketch, "E1160", {"start": v(12.2, 5.76) * mm, "end": v(12.2, 5.93) * mm});
            skLineSegment(sketch, "E1161", {"start": v(22.7, 5.76) * mm, "end": v(22.7, 5.93) * mm});
            skLineSegment(sketch, "E1162", {"start": v(23.54, 5.76) * mm, "end": v(23.54, 5.93) * mm});
            skLineSegment(sketch, "E1163", {"start": v(-23.03, 5.59) * mm, "end": v(-22.86, 5.93) * mm});
            skLineSegment(sketch, "E1164", {"start": v(-22.01, 5.59) * mm, "end": v(-22.18, 5.76) * mm});
            skLineSegment(sketch, "E1165", {"start": v(-21.84, 5.59) * mm, "end": v(-22.01, 5.59) * mm});
            skLineSegment(sketch, "E1166", {"start": v(-21.84, 5.59) * mm, "end": v(-21.67, 5.76) * mm});
            skLineSegment(sketch, "E1167", {"start": v(-21.67, 5.76) * mm, "end": v(-21.84, 5.93) * mm});
            skLineSegment(sketch, "E1168", {"start": v(-11.68, 5.59) * mm, "end": v(-11.85, 5.76) * mm});
            skLineSegment(sketch, "E1169", {"start": v(-11.85, 5.76) * mm, "end": v(-11.68, 6.1) * mm});
            skLineSegment(sketch, "E1170", {"start": v(-11.68, 5.59) * mm, "end": v(-11.51, 5.76) * mm});
            skLineSegment(sketch, "E1171", {"start": v(-11, 5.59) * mm, "end": v(-11.18, 5.93) * mm});
            skLineSegment(sketch, "E1172", {"start": v(-6.27, 5.59) * mm, "end": v(-6.27, 5.76) * mm});
            skLineSegment(sketch, "E1173", {"start": v(-6.27, 5.76) * mm, "end": v(-6.1, 5.76) * mm});
            skLineSegment(sketch, "E1174", {"start": v(-5.93, 5.59) * mm, "end": v(-5.93, 5.76) * mm});
            skLineSegment(sketch, "E1175", {"start": v(-5.93, 5.76) * mm, "end": v(-6.1, 5.76) * mm});
            skLineSegment(sketch, "E1176", {"start": v(-1.7, 5.59) * mm, "end": v(-1.86, 5.59) * mm});
            skLineSegment(sketch, "E1177", {"start": v(-1.52, 5.59) * mm, "end": v(-1.7, 5.59) * mm});
            skLineSegment(sketch, "E1178", {"start": v(-1.52, 5.59) * mm, "end": v(-1.35, 5.76) * mm});
            skLineSegment(sketch, "E1179", {"start": v(-1.02, 5.59) * mm, "end": v(-1.02, 5.76) * mm});
            skLineSegment(sketch, "E1180", {"start": v(-0.5, 5.59) * mm, "end": v(-0.5, 5.76) * mm});
            skLineSegment(sketch, "E1181", {"start": v(0.5, 5.59) * mm, "end": v(0.5, 5.76) * mm});
            skLineSegment(sketch, "E1182", {"start": v(0.85, 5.59) * mm, "end": v(0.85, 5.76) * mm});
            skLineSegment(sketch, "E1183", {"start": v(1.52, 5.59) * mm, "end": v(1.35, 5.76) * mm});
            skLineSegment(sketch, "E1184", {"start": v(3.05, 5.59) * mm, "end": v(1.52, 6.77) * mm});
            skLineSegment(sketch, "E1185", {"start": v(5.93, 5.59) * mm, "end": v(5.93, 5.76) * mm});
            skLineSegment(sketch, "E1186", {"start": v(6.27, 5.59) * mm, "end": v(6.27, 5.76) * mm});
            skLineSegment(sketch, "E1187", {"start": v(11.18, 5.59) * mm, "end": v(11.18, 5.76) * mm});
            skLineSegment(sketch, "E1188", {"start": v(12.2, 5.59) * mm, "end": v(12.2, 5.76) * mm});
            skLineSegment(sketch, "E1189", {"start": v(-23.03, 5.42) * mm, "end": v(-23.03, 5.59) * mm});
            skLineSegment(sketch, "E1190", {"start": v(-22.86, 5.42) * mm, "end": v(-23.03, 5.42) * mm});
            skLineSegment(sketch, "E1191", {"start": v(-22.86, 5.42) * mm, "end": v(-22.18, 5.42) * mm});
            skLineSegment(sketch, "E1192", {"start": v(-22.18, 5.42) * mm, "end": v(-22.01, 5.59) * mm});
            skLineSegment(sketch, "E1193", {"start": v(-21.84, 5.42) * mm, "end": v(-21.84, 5.59) * mm});
            skLineSegment(sketch, "E1194", {"start": v(-11.18, 5.42) * mm, "end": v(-11, 5.59) * mm});
            skLineSegment(sketch, "E1195", {"start": v(-10.84, 5.42) * mm, "end": v(-11, 5.59) * mm});
            skLineSegment(sketch, "E1196", {"start": v(-6.27, 5.42) * mm, "end": v(-6.27, 5.59) * mm});
            skLineSegment(sketch, "E1197", {"start": v(-5.93, 5.42) * mm, "end": v(-5.93, 5.59) * mm});
            skLineSegment(sketch, "E1198", {"start": v(-5.76, 5.42) * mm, "end": v(-5.93, 5.42) * mm});
            skLineSegment(sketch, "E1199", {"start": v(-1.7, 5.42) * mm, "end": v(-1.7, 5.59) * mm});
            skLineSegment(sketch, "E1200", {"start": v(5.93, 5.42) * mm, "end": v(5.76, 5.42) * mm});
            skLineSegment(sketch, "E1201", {"start": v(5.93, 5.42) * mm, "end": v(5.93, 5.59) * mm});
            skLineSegment(sketch, "E1202", {"start": v(6.27, 5.42) * mm, "end": v(6.27, 5.59) * mm});
            skLineSegment(sketch, "E1203", {"start": v(6.43, 5.42) * mm, "end": v(6.27, 5.42) * mm});
            skLineSegment(sketch, "E1204", {"start": v(6.43, 5.42) * mm, "end": v(6.77, 5.59) * mm});
            skLineSegment(sketch, "E1205", {"start": v(6.94, 5.42) * mm, "end": v(6.94, 5.59) * mm});
            skLineSegment(sketch, "E1206", {"start": v(6.94, 5.59) * mm, "end": v(6.77, 5.59) * mm});
            skLineSegment(sketch, "E1207", {"start": v(11.18, 5.42) * mm, "end": v(11.18, 5.59) * mm});
            skLineSegment(sketch, "E1208", {"start": v(11.35, 5.42) * mm, "end": v(11.18, 5.42) * mm});
            skLineSegment(sketch, "E1209", {"start": v(12.02, 5.42) * mm, "end": v(11.35, 5.42) * mm});
            skLineSegment(sketch, "E1210", {"start": v(12.2, 5.42) * mm, "end": v(12.02, 5.42) * mm});
            skLineSegment(sketch, "E1211", {"start": v(12.2, 5.42) * mm, "end": v(12.2, 5.59) * mm});
            skLineSegment(sketch, "E1212", {"start": v(-23.03, 5.25) * mm, "end": v(-23.03, 5.42) * mm});
            skLineSegment(sketch, "E1213", {"start": v(-18.46, 5.25) * mm, "end": v(-18.46, 5.42) * mm});
            skLineSegment(sketch, "E1214", {"start": v(-18.46, 5.42) * mm, "end": v(-17.95, 5.93) * mm});
            skLineSegment(sketch, "E1215", {"start": v(-17.95, 5.93) * mm, "end": v(-17.61, 5.93) * mm});
            skLineSegment(sketch, "E1216", {"start": v(-11.35, 5.25) * mm, "end": v(-11.68, 5.59) * mm});
            skLineSegment(sketch, "E1217", {"start": v(-11.18, 5.25) * mm, "end": v(-11.35, 5.25) * mm});
            skLineSegment(sketch, "E1218", {"start": v(-11.18, 5.25) * mm, "end": v(-11.18, 5.42) * mm});
            skLineSegment(sketch, "E1219", {"start": v(-11, 5.25) * mm, "end": v(-11.18, 5.25) * mm});
            skLineSegment(sketch, "E1220", {"start": v(-11, 5.25) * mm, "end": v(-10.84, 5.42) * mm});
            skLineSegment(sketch, "E1221", {"start": v(-6.27, 5.25) * mm, "end": v(-6.43, 5.25) * mm});
            skLineSegment(sketch, "E1222", {"start": v(-6.27, 5.25) * mm, "end": v(-6.27, 5.42) * mm});
            skLineSegment(sketch, "E1223", {"start": v(-5.93, 5.25) * mm, "end": v(-5.93, 5.42) * mm});
            skLineSegment(sketch, "E1224", {"start": v(1.35, 5.25) * mm, "end": v(1.52, 5.59) * mm});
            skLineSegment(sketch, "E1225", {"start": v(5.42, 5.25) * mm, "end": v(5.42, 5.42) * mm});
            skLineSegment(sketch, "E1226", {"start": v(5.42, 5.42) * mm, "end": v(5.59, 5.59) * mm});
            skLineSegment(sketch, "E1227", {"start": v(5.59, 5.59) * mm, "end": v(5.76, 5.42) * mm});
            skLineSegment(sketch, "E1228", {"start": v(5.93, 5.25) * mm, "end": v(5.93, 5.42) * mm});
            skLineSegment(sketch, "E1229", {"start": v(6.27, 5.25) * mm, "end": v(6.27, 5.42) * mm});
            skLineSegment(sketch, "E1230", {"start": v(6.94, 5.25) * mm, "end": v(6.94, 5.42) * mm});
            skLineSegment(sketch, "E1231", {"start": v(11.18, 5.25) * mm, "end": v(11.18, 5.42) * mm});
            skLineSegment(sketch, "E1232", {"start": v(12.2, 5.25) * mm, "end": v(12.2, 5.42) * mm});
            skLineSegment(sketch, "E1233", {"start": v(-23.03, 5.08) * mm, "end": v(-23.03, 5.25) * mm});
            skLineSegment(sketch, "E1234", {"start": v(-22.86, 5.08) * mm, "end": v(-23.03, 5.08) * mm});
            skLineSegment(sketch, "E1235", {"start": v(-22.01, 5.08) * mm, "end": v(-22.86, 5.08) * mm});
            skLineSegment(sketch, "E1236", {"start": v(-21.84, 5.08) * mm, "end": v(-22.01, 5.08) * mm});
            skLineSegment(sketch, "E1237", {"start": v(-21.84, 5.08) * mm, "end": v(-21.67, 5.25) * mm});
            skLineSegment(sketch, "E1238", {"start": v(-21.67, 5.25) * mm, "end": v(-21.84, 5.42) * mm});
            skLineSegment(sketch, "E1239", {"start": v(-18.29, 5.08) * mm, "end": v(-18.46, 5.08) * mm});
            skLineSegment(sketch, "E1240", {"start": v(-18.46, 5.08) * mm, "end": v(-18.46, 5.25) * mm});
            skLineSegment(sketch, "E1241", {"start": v(-10.84, 5.08) * mm, "end": v(-11, 5.25) * mm});
            skLineSegment(sketch, "E1242", {"start": v(-10.84, 5.08) * mm, "end": v(-10.67, 5.25) * mm});
            skLineSegment(sketch, "E1243", {"start": v(-10.67, 5.25) * mm, "end": v(-10.84, 5.42) * mm});
            skLineSegment(sketch, "E1244", {"start": v(-6.77, 5.08) * mm, "end": v(-6.77, 5.25) * mm});
            skLineSegment(sketch, "E1245", {"start": v(-6.77, 5.25) * mm, "end": v(-6.6, 5.42) * mm});
            skLineSegment(sketch, "E1246", {"start": v(-6.6, 5.42) * mm, "end": v(-6.43, 5.25) * mm});
            skLineSegment(sketch, "E1247", {"start": v(-6.27, 5.08) * mm, "end": v(-6.27, 5.25) * mm});
            skLineSegment(sketch, "E1248", {"start": v(-5.42, 5.08) * mm, "end": v(-5.42, 5.25) * mm});
            skLineSegment(sketch, "E1249", {"start": v(-5.42, 5.25) * mm, "end": v(-5.76, 5.42) * mm});
            skLineSegment(sketch, "E1250", {"start": v(-1.7, 5.08) * mm, "end": v(-1.7, 5.42) * mm});
            skLineSegment(sketch, "E1251", {"start": v(-0.5, 5.08) * mm, "end": v(-0.5, 5.59) * mm});
            skLineSegment(sketch, "E1252", {"start": v(1.19, 5.08) * mm, "end": v(0.85, 5.42) * mm});
            skLineSegment(sketch, "E1253", {"start": v(0.85, 5.42) * mm, "end": v(0.85, 5.59) * mm});
            skLineSegment(sketch, "E1254", {"start": v(1.35, 5.08) * mm, "end": v(1.19, 5.08) * mm});
            skLineSegment(sketch, "E1255", {"start": v(1.35, 5.08) * mm, "end": v(1.35, 5.25) * mm});
            skLineSegment(sketch, "E1256", {"start": v(5.42, 5.08) * mm, "end": v(5.42, 5.25) * mm});
            skLineSegment(sketch, "E1257", {"start": v(5.59, 5.08) * mm, "end": v(5.42, 5.08) * mm});
            skLineSegment(sketch, "E1258", {"start": v(5.93, 5.08) * mm, "end": v(5.93, 5.25) * mm});
            skLineSegment(sketch, "E1259", {"start": v(6.27, 5.08) * mm, "end": v(6.27, 5.25) * mm});
            skLineSegment(sketch, "E1260", {"start": v(6.94, 5.08) * mm, "end": v(6.77, 5.08) * mm});
            skLineSegment(sketch, "E1261", {"start": v(6.94, 5.08) * mm, "end": v(6.94, 5.25) * mm});
            skLineSegment(sketch, "E1262", {"start": v(7.11, 5.08) * mm, "end": v(6.94, 5.08) * mm});
            skLineSegment(sketch, "E1263", {"start": v(11.18, 5.08) * mm, "end": v(11.18, 5.25) * mm});
            skLineSegment(sketch, "E1264", {"start": v(11.35, 5.08) * mm, "end": v(11.18, 5.08) * mm});
            skLineSegment(sketch, "E1265", {"start": v(12.02, 5.08) * mm, "end": v(11.35, 5.08) * mm});
            skLineSegment(sketch, "E1266", {"start": v(12.2, 5.08) * mm, "end": v(12.02, 5.08) * mm});
            skLineSegment(sketch, "E1267", {"start": v(12.2, 5.08) * mm, "end": v(12.2, 5.25) * mm});
            skLineSegment(sketch, "E1268", {"start": v(-23.03, 4.91) * mm, "end": v(-23.03, 5.08) * mm});
            skLineSegment(sketch, "E1269", {"start": v(-21.84, 4.91) * mm, "end": v(-21.84, 5.08) * mm});
            skLineSegment(sketch, "E1270", {"start": v(-17.95, 4.91) * mm, "end": v(-18.29, 5.08) * mm});
            skLineSegment(sketch, "E1271", {"start": v(-17.95, 4.91) * mm, "end": v(-17.44, 5.42) * mm});
            skLineSegment(sketch, "E1272", {"start": v(-17.44, 5.42) * mm, "end": v(-17.44, 5.76) * mm});
            skLineSegment(sketch, "E1273", {"start": v(-17.44, 5.76) * mm, "end": v(-17.61, 5.93) * mm});
            skLineSegment(sketch, "E1274", {"start": v(-11, 4.91) * mm, "end": v(-10.84, 5.08) * mm});
            skLineSegment(sketch, "E1275", {"start": v(-10.67, 4.91) * mm, "end": v(-10.84, 5.08) * mm});
            skLineSegment(sketch, "E1276", {"start": v(-6.77, 4.91) * mm, "end": v(-6.94, 4.91) * mm});
            skLineSegment(sketch, "E1277", {"start": v(-6.77, 4.91) * mm, "end": v(-6.77, 5.08) * mm});
            skLineSegment(sketch, "E1278", {"start": v(-6.6, 4.91) * mm, "end": v(-6.77, 4.91) * mm});
            skLineSegment(sketch, "E1279", {"start": v(-6.43, 4.91) * mm, "end": v(-6.6, 4.91) * mm});
            skLineSegment(sketch, "E1280", {"start": v(-6.27, 4.91) * mm, "end": v(-6.43, 4.91) * mm});
            skLineSegment(sketch, "E1281", {"start": v(-6.27, 4.91) * mm, "end": v(-6.27, 5.08) * mm});
            skLineSegment(sketch, "E1282", {"start": v(-5.93, 4.91) * mm, "end": v(-5.93, 5.25) * mm});
            skLineSegment(sketch, "E1283", {"start": v(-5.42, 4.91) * mm, "end": v(-5.59, 4.91) * mm});
            skLineSegment(sketch, "E1284", {"start": v(-5.42, 4.91) * mm, "end": v(-5.42, 5.08) * mm});
            skLineSegment(sketch, "E1285", {"start": v(-2.37, 8.13) * mm, "end": v(-3, 7.08) * mm});
            skLineSegment(sketch, "E1286", {"start": v(-3, 7.08) * mm, "end": v(-3.5, 6.08) * mm});
            skLineSegment(sketch, "E1287", {"start": v(-3.5, 6.08) * mm, "end": v(-3.73, 5.25) * mm});
            skLineSegment(sketch, "E1288", {"start": v(-3.73, 5.25) * mm, "end": v(-3.56, 4.91) * mm});
            skLineSegment(sketch, "E1289", {"start": v(-3.56, 4.91) * mm, "end": v(-3.05, 4.91) * mm});
            skLineSegment(sketch, "E1290", {"start": v(-3.05, 4.91) * mm, "end": v(-2.05, 5.45) * mm});
            skLineSegment(sketch, "E1291", {"start": v(-2.05, 5.45) * mm, "end": v(-1.86, 5.59) * mm});
            skLineSegment(sketch, "E1292", {"start": v(-1.7, 4.91) * mm, "end": v(-1.7, 5.08) * mm});
            skLineSegment(sketch, "E1293", {"start": v(-1.52, 4.91) * mm, "end": v(-1.7, 4.91) * mm});
            skLineSegment(sketch, "E1294", {"start": v(-1.35, 4.91) * mm, "end": v(-1.52, 4.91) * mm});
            skLineSegment(sketch, "E1295", {"start": v(-1.35, 4.91) * mm, "end": v(-1.02, 5.25) * mm});
            skLineSegment(sketch, "E1296", {"start": v(-1.02, 5.25) * mm, "end": v(-1.02, 5.59) * mm});
            skLineSegment(sketch, "E1297", {"start": v(-0.5, 4.91) * mm, "end": v(-0.5, 5.08) * mm});
            skLineSegment(sketch, "E1298", {"start": v(-0.34, 4.91) * mm, "end": v(-0.5, 4.91) * mm});
            skLineSegment(sketch, "E1299", {"start": v(-0.34, 4.91) * mm, "end": v(-0.17, 5.08) * mm});
            skLineSegment(sketch, "E1300", {"start": v(1.19, 4.91) * mm, "end": v(1.19, 5.08) * mm});
            skLineSegment(sketch, "E1301", {"start": v(5.76, 4.91) * mm, "end": v(5.59, 5.08) * mm});
            skLineSegment(sketch, "E1302", {"start": v(5.93, 4.91) * mm, "end": v(5.76, 4.91) * mm});
            skLineSegment(sketch, "E1303", {"start": v(5.93, 4.91) * mm, "end": v(5.93, 5.08) * mm});
            skLineSegment(sketch, "E1304", {"start": v(6.27, 4.91) * mm, "end": v(6.27, 5.08) * mm});
            skLineSegment(sketch, "E1305", {"start": v(6.43, 4.91) * mm, "end": v(6.27, 4.91) * mm});
            skLineSegment(sketch, "E1306", {"start": v(6.43, 4.91) * mm, "end": v(6.77, 5.08) * mm});
            skLineSegment(sketch, "E1307", {"start": v(7.28, 4.91) * mm, "end": v(7.28, 5.08) * mm});
            skLineSegment(sketch, "E1308", {"start": v(7.28, 5.08) * mm, "end": v(7.11, 5.08) * mm});
            skLineSegment(sketch, "E1309", {"start": v(11.18, 4.91) * mm, "end": v(11.18, 5.08) * mm});
            skLineSegment(sketch, "E1310", {"start": v(12.2, 4.91) * mm, "end": v(12.2, 5.08) * mm});
            skLineSegment(sketch, "E1311", {"start": v(-23.03, 4.74) * mm, "end": v(-23.03, 4.91) * mm});
            skLineSegment(sketch, "E1312", {"start": v(-15.24, 8.8) * mm, "end": v(-16.09, 8.64) * mm});
            skLineSegment(sketch, "E1313", {"start": v(-16.09, 8.64) * mm, "end": v(-16.93, 7.79) * mm});
            skLineSegment(sketch, "E1314", {"start": v(-16.93, 7.79) * mm, "end": v(-17.23, 7.09) * mm});
            skLineSegment(sketch, "E1315", {"start": v(-17.23, 7.09) * mm, "end": v(-18.8, 5.76) * mm});
            skLineSegment(sketch, "E1316", {"start": v(-18.8, 5.76) * mm, "end": v(-18.8, 4.91) * mm});
            skLineSegment(sketch, "E1317", {"start": v(-18.8, 4.91) * mm, "end": v(-18.63, 4.74) * mm});
            skLineSegment(sketch, "E1318", {"start": v(-18.63, 4.74) * mm, "end": v(-18.12, 4.74) * mm});
            skLineSegment(sketch, "E1319", {"start": v(-18.12, 4.74) * mm, "end": v(-17.95, 4.91) * mm});
            skLineSegment(sketch, "E1320", {"start": v(-11, 4.74) * mm, "end": v(-11, 4.91) * mm});
            skLineSegment(sketch, "E1321", {"start": v(-10.84, 4.74) * mm, "end": v(-11, 4.74) * mm});
            skLineSegment(sketch, "E1322", {"start": v(-10.84, 4.74) * mm, "end": v(-10.67, 4.91) * mm});
            skLineSegment(sketch, "E1323", {"start": v(-6.27, 4.74) * mm, "end": v(-6.27, 4.91) * mm});
            skLineSegment(sketch, "E1324", {"start": v(-5.93, 4.74) * mm, "end": v(-5.93, 4.91) * mm});
            skLineSegment(sketch, "E1325", {"start": v(-5.76, 4.74) * mm, "end": v(-5.93, 4.74) * mm});
            skLineSegment(sketch, "E1326", {"start": v(-5.76, 4.74) * mm, "end": v(-5.59, 4.91) * mm});
            skLineSegment(sketch, "E1327", {"start": v(-1.7, 4.74) * mm, "end": v(-1.7, 4.91) * mm});
            skLineSegment(sketch, "E1328", {"start": v(-1.35, 4.74) * mm, "end": v(-1.35, 4.91) * mm});
            skLineSegment(sketch, "E1329", {"start": v(-0.5, 4.74) * mm, "end": v(-0.5, 4.91) * mm});
            skLineSegment(sketch, "E1330", {"start": v(1.52, 4.74) * mm, "end": v(1.35, 5.08) * mm});
            skLineSegment(sketch, "E1331", {"start": v(3.56, 4.74) * mm, "end": v(3.5, 5.4) * mm});
            skLineSegment(sketch, "E1332", {"start": v(3.5, 5.4) * mm, "end": v(2.37, 8.13) * mm});
            skLineSegment(sketch, "E1333", {"start": v(6.1, 4.74) * mm, "end": v(5.93, 4.91) * mm});
            skLineSegment(sketch, "E1334", {"start": v(6.1, 4.74) * mm, "end": v(6.27, 4.91) * mm});
            skLineSegment(sketch, "E1335", {"start": v(11.18, 4.74) * mm, "end": v(11.18, 4.91) * mm});
            skLineSegment(sketch, "E1336", {"start": v(11.35, 4.74) * mm, "end": v(11.18, 4.74) * mm});
            skLineSegment(sketch, "E1337", {"start": v(12.02, 4.74) * mm, "end": v(11.35, 4.74) * mm});
            skLineSegment(sketch, "E1338", {"start": v(12.2, 4.74) * mm, "end": v(12.02, 4.74) * mm});
            skLineSegment(sketch, "E1339", {"start": v(12.2, 4.74) * mm, "end": v(12.2, 4.91) * mm});
            skLineSegment(sketch, "E1340", {"start": v(-23.03, 4.57) * mm, "end": v(-23.2, 4.57) * mm});
            skLineSegment(sketch, "E1341", {"start": v(-23.03, 4.57) * mm, "end": v(-23.03, 4.74) * mm});
            skLineSegment(sketch, "E1342", {"start": v(-11, 4.57) * mm, "end": v(-11, 4.74) * mm});
            skLineSegment(sketch, "E1343", {"start": v(-10.67, 4.57) * mm, "end": v(-10.84, 4.74) * mm});
            skLineSegment(sketch, "E1344", {"start": v(-10.5, 4.57) * mm, "end": v(-10.67, 4.57) * mm});
            skLineSegment(sketch, "E1345", {"start": v(-10.5, 4.57) * mm, "end": v(-10.33, 4.74) * mm});
            skLineSegment(sketch, "E1346", {"start": v(-10.33, 4.74) * mm, "end": v(-10.67, 4.91) * mm});
            skLineSegment(sketch, "E1347", {"start": v(-6.27, 4.57) * mm, "end": v(-6.27, 4.74) * mm});
            skLineSegment(sketch, "E1348", {"start": v(-6.1, 4.57) * mm, "end": v(-6.27, 4.57) * mm});
            skLineSegment(sketch, "E1349", {"start": v(-6.1, 4.57) * mm, "end": v(-5.93, 4.74) * mm});
            skLineSegment(sketch, "E1350", {"start": v(-5.76, 4.57) * mm, "end": v(-5.76, 4.74) * mm});
            skLineSegment(sketch, "E1351", {"start": v(-1.7, 4.57) * mm, "end": v(-1.7, 4.74) * mm});
            skLineSegment(sketch, "E1352", {"start": v(-0.5, 4.57) * mm, "end": v(-0.5, 4.74) * mm});
            skLineSegment(sketch, "E1353", {"start": v(1.35, 4.57) * mm, "end": v(1.19, 4.91) * mm});
            skLineSegment(sketch, "E1354", {"start": v(1.52, 4.57) * mm, "end": v(1.35, 4.57) * mm});
            skLineSegment(sketch, "E1355", {"start": v(1.52, 4.57) * mm, "end": v(1.52, 4.74) * mm});
            skLineSegment(sketch, "E1356", {"start": v(3.39, 4.57) * mm, "end": v(2.37, 4.74) * mm});
            skLineSegment(sketch, "E1357", {"start": v(2.37, 4.74) * mm, "end": v(1.86, 5.25) * mm});
            skLineSegment(sketch, "E1358", {"start": v(1.86, 5.25) * mm, "end": v(1.86, 5.42) * mm});
            skLineSegment(sketch, "E1359", {"start": v(1.86, 5.42) * mm, "end": v(1.52, 5.59) * mm});
            skLineSegment(sketch, "E1360", {"start": v(3.39, 4.57) * mm, "end": v(3.56, 4.57) * mm});
            skLineSegment(sketch, "E1361", {"start": v(3.56, 4.57) * mm, "end": v(3.56, 4.74) * mm});
            skLineSegment(sketch, "E1362", {"start": v(5.93, 4.57) * mm, "end": v(5.76, 4.57) * mm});
            skLineSegment(sketch, "E1363", {"start": v(5.93, 4.57) * mm, "end": v(6.1, 4.74) * mm});
            skLineSegment(sketch, "E1364", {"start": v(7.11, 4.57) * mm, "end": v(7.28, 4.91) * mm});
            skLineSegment(sketch, "E1365", {"start": v(11.18, 4.57) * mm, "end": v(11.18, 4.74) * mm});
            skLineSegment(sketch, "E1366", {"start": v(12.2, 4.57) * mm, "end": v(12.2, 4.74) * mm});
            skLineSegment(sketch, "E1367", {"start": v(-10.84, 4.4) * mm, "end": v(-11, 4.57) * mm});
            skLineSegment(sketch, "E1368", {"start": v(-10.84, 4.4) * mm, "end": v(-10.67, 4.57) * mm});
            skLineSegment(sketch, "E1369", {"start": v(-10.33, 4.4) * mm, "end": v(-10.5, 4.57) * mm});
            skLineSegment(sketch, "E1370", {"start": v(-7.11, 4.4) * mm, "end": v(-7.28, 4.57) * mm});
            skLineSegment(sketch, "E1371", {"start": v(-7.28, 4.57) * mm, "end": v(-6.94, 4.91) * mm});
            skLineSegment(sketch, "E1372", {"start": v(-6.94, 4.4) * mm, "end": v(-7.11, 4.4) * mm});
            skLineSegment(sketch, "E1373", {"start": v(-6.77, 4.4) * mm, "end": v(-6.94, 4.4) * mm});
            skLineSegment(sketch, "E1374", {"start": v(-6.6, 4.4) * mm, "end": v(-6.77, 4.4) * mm});
            skLineSegment(sketch, "E1375", {"start": v(-6.43, 4.4) * mm, "end": v(-6.6, 4.4) * mm});
            skLineSegment(sketch, "E1376", {"start": v(-6.43, 4.4) * mm, "end": v(-6.27, 4.57) * mm});
            skLineSegment(sketch, "E1377", {"start": v(-6.1, 4.4) * mm, "end": v(-6.1, 4.57) * mm});
            skLineSegment(sketch, "E1378", {"start": v(-1.7, 4.4) * mm, "end": v(-1.7, 4.57) * mm});
            skLineSegment(sketch, "E1379", {"start": v(-1.52, 4.4) * mm, "end": v(-1.7, 4.4) * mm});
            skLineSegment(sketch, "E1380", {"start": v(-1.52, 4.4) * mm, "end": v(-1.35, 4.74) * mm});
            skLineSegment(sketch, "E1381", {"start": v(-0.68, 4.4) * mm, "end": v(-0.85, 4.4) * mm});
            skLineSegment(sketch, "E1382", {"start": v(-0.68, 4.4) * mm, "end": v(-0.5, 4.57) * mm});
            skLineSegment(sketch, "E1383", {"start": v(1.52, 4.4) * mm, "end": v(1.52, 4.57) * mm});
            skLineSegment(sketch, "E1384", {"start": v(5.25, 4.4) * mm, "end": v(5.08, 4.57) * mm});
            skLineSegment(sketch, "E1385", {"start": v(5.08, 4.57) * mm, "end": v(5.08, 4.74) * mm});
            skLineSegment(sketch, "E1386", {"start": v(5.08, 4.74) * mm, "end": v(5.42, 5.08) * mm});
            skLineSegment(sketch, "E1387", {"start": v(5.42, 4.4) * mm, "end": v(5.25, 4.4) * mm});
            skLineSegment(sketch, "E1388", {"start": v(5.42, 4.4) * mm, "end": v(5.76, 4.57) * mm});
            skLineSegment(sketch, "E1389", {"start": v(5.93, 4.4) * mm, "end": v(5.93, 4.57) * mm});
            skLineSegment(sketch, "E1390", {"start": v(6.94, 4.4) * mm, "end": v(6.43, 4.91) * mm});
            skLineSegment(sketch, "E1391", {"start": v(7.11, 4.4) * mm, "end": v(6.94, 4.4) * mm});
            skLineSegment(sketch, "E1392", {"start": v(7.11, 4.4) * mm, "end": v(7.11, 4.57) * mm});
            skLineSegment(sketch, "E1393", {"start": v(11.18, 4.4) * mm, "end": v(11.18, 4.57) * mm});
            skLineSegment(sketch, "E1394", {"start": v(11.35, 4.4) * mm, "end": v(11.18, 4.4) * mm});
            skLineSegment(sketch, "E1395", {"start": v(12.2, 4.4) * mm, "end": v(12.2, 4.57) * mm});
            skLineSegment(sketch, "E1396", {"start": v(-10.5, 4.23) * mm, "end": v(-10.33, 4.4) * mm});
            skLineSegment(sketch, "E1397", {"start": v(-10, 4.23) * mm, "end": v(-10.33, 4.4) * mm});
            skLineSegment(sketch, "E1398", {"start": v(-6.94, 4.23) * mm, "end": v(-6.94, 4.4) * mm});
            skLineSegment(sketch, "E1399", {"start": v(-6.43, 4.23) * mm, "end": v(-6.43, 4.4) * mm});
            skLineSegment(sketch, "E1400", {"start": v(-5.59, 4.23) * mm, "end": v(-5.76, 4.57) * mm});
            skLineSegment(sketch, "E1401", {"start": v(-5.42, 4.23) * mm, "end": v(-5.59, 4.23) * mm});
            skLineSegment(sketch, "E1402", {"start": v(-5.42, 4.23) * mm, "end": v(-5.25, 4.4) * mm});
            skLineSegment(sketch, "E1403", {"start": v(-5.25, 4.4) * mm, "end": v(-5.25, 4.74) * mm});
            skLineSegment(sketch, "E1404", {"start": v(-5.25, 4.74) * mm, "end": v(-5.42, 4.91) * mm});
            skLineSegment(sketch, "E1405", {"start": v(-1.7, 4.23) * mm, "end": v(-1.7, 4.4) * mm});
            skLineSegment(sketch, "E1406", {"start": v(-1.02, 4.23) * mm, "end": v(-0.85, 4.4) * mm});
            skLineSegment(sketch, "E1407", {"start": v(-0.68, 4.23) * mm, "end": v(-0.68, 4.4) * mm});
            skLineSegment(sketch, "E1408", {"start": v(-0.34, 4.23) * mm, "end": v(-0.5, 4.57) * mm});
            skLineSegment(sketch, "E1409", {"start": v(5.42, 4.23) * mm, "end": v(5.42, 4.4) * mm});
            skLineSegment(sketch, "E1410", {"start": v(5.93, 4.23) * mm, "end": v(5.93, 4.4) * mm});
            skLineSegment(sketch, "E1411", {"start": v(6.43, 4.23) * mm, "end": v(6.43, 4.4) * mm});
            skLineSegment(sketch, "E1412", {"start": v(6.43, 4.4) * mm, "end": v(6.1, 4.74) * mm});
            skLineSegment(sketch, "E1413", {"start": v(7.11, 4.23) * mm, "end": v(7.11, 4.4) * mm});
            skLineSegment(sketch, "E1414", {"start": v(11, 4.23) * mm, "end": v(11.18, 4.4) * mm});
            skLineSegment(sketch, "E1415", {"start": v(12.02, 4.23) * mm, "end": v(11.85, 4.4) * mm});
            skLineSegment(sketch, "E1416", {"start": v(11.85, 4.4) * mm, "end": v(11.35, 4.4) * mm});
            skLineSegment(sketch, "E1417", {"start": v(12.2, 4.23) * mm, "end": v(12.02, 4.23) * mm});
            skLineSegment(sketch, "E1418", {"start": v(12.2, 4.23) * mm, "end": v(12.2, 4.4) * mm});
            skLineSegment(sketch, "E1419", {"start": v(-10.67, 4.06) * mm, "end": v(-10.84, 4.4) * mm});
            skLineSegment(sketch, "E1420", {"start": v(-10.67, 4.06) * mm, "end": v(-10.5, 4.23) * mm});
            skLineSegment(sketch, "E1421", {"start": v(-10.33, 4.06) * mm, "end": v(-10.5, 4.23) * mm});
            skLineSegment(sketch, "E1422", {"start": v(-10.16, 4.06) * mm, "end": v(-10.33, 4.06) * mm});
            skLineSegment(sketch, "E1423", {"start": v(-10, 4.06) * mm, "end": v(-10.16, 4.06) * mm});
            skLineSegment(sketch, "E1424", {"start": v(-10, 4.06) * mm, "end": v(-10, 4.23) * mm});
            skLineSegment(sketch, "E1425", {"start": v(-5.42, 4.06) * mm, "end": v(-5.42, 4.23) * mm});
            skLineSegment(sketch, "E1426", {"start": v(-1.02, 4.06) * mm, "end": v(-1.02, 4.23) * mm});
            skLineSegment(sketch, "E1427", {"start": v(-0.85, 4.06) * mm, "end": v(-1.02, 4.06) * mm});
            skLineSegment(sketch, "E1428", {"start": v(-0.85, 4.06) * mm, "end": v(-0.68, 4.23) * mm});
            skLineSegment(sketch, "E1429", {"start": v(-0.5, 4.06) * mm, "end": v(-0.68, 4.23) * mm});
            skLineSegment(sketch, "E1430", {"start": v(-0.34, 4.06) * mm, "end": v(-0.5, 4.06) * mm});
            skLineSegment(sketch, "E1431", {"start": v(-0.34, 4.06) * mm, "end": v(-0.34, 4.23) * mm});
            skLineSegment(sketch, "E1432", {"start": v(0.68, 4.06) * mm, "end": v(0.5, 4.23) * mm});
            skLineSegment(sketch, "E1433", {"start": v(0.5, 4.23) * mm, "end": v(0.5, 5.59) * mm});
            skLineSegment(sketch, "E1434", {"start": v(5.93, 4.06) * mm, "end": v(5.76, 4.06) * mm});
            skLineSegment(sketch, "E1435", {"start": v(5.93, 4.06) * mm, "end": v(5.93, 4.23) * mm});
            skLineSegment(sketch, "E1436", {"start": v(6.43, 4.06) * mm, "end": v(6.43, 4.23) * mm});
            skLineSegment(sketch, "E1437", {"start": v(6.6, 4.06) * mm, "end": v(6.43, 4.06) * mm});
            skLineSegment(sketch, "E1438", {"start": v(6.6, 4.06) * mm, "end": v(6.94, 4.06) * mm});
            skLineSegment(sketch, "E1439", {"start": v(6.94, 4.06) * mm, "end": v(7.11, 4.23) * mm});
            skLineSegment(sketch, "E1440", {"start": v(11, 4.06) * mm, "end": v(11, 4.23) * mm});
            skLineSegment(sketch, "E1441", {"start": v(11.18, 4.06) * mm, "end": v(11, 4.06) * mm});
            skLineSegment(sketch, "E1442", {"start": v(11.18, 4.06) * mm, "end": v(11.85, 4.06) * mm});
            skLineSegment(sketch, "E1443", {"start": v(11.85, 4.06) * mm, "end": v(12.02, 4.23) * mm});
            skLineSegment(sketch, "E1444", {"start": v(12.2, 4.06) * mm, "end": v(12.2, 4.23) * mm});
            skLineSegment(sketch, "E1445", {"start": v(-10.5, 3.9) * mm, "end": v(-10.67, 4.06) * mm});
            skLineSegment(sketch, "E1446", {"start": v(-10.5, 3.9) * mm, "end": v(-10.33, 4.06) * mm});
            skLineSegment(sketch, "E1447", {"start": v(-10, 3.9) * mm, "end": v(-10, 4.06) * mm});
            skLineSegment(sketch, "E1448", {"start": v(-6.43, 3.9) * mm, "end": v(-6.43, 4.23) * mm});
            skLineSegment(sketch, "E1449", {"start": v(-5.93, 3.9) * mm, "end": v(-6.1, 4.06) * mm});
            skLineSegment(sketch, "E1450", {"start": v(-6.1, 4.06) * mm, "end": v(-6.1, 4.4) * mm});
            skLineSegment(sketch, "E1451", {"start": v(-5.76, 3.9) * mm, "end": v(-5.93, 3.9) * mm});
            skLineSegment(sketch, "E1452", {"start": v(-5.76, 3.9) * mm, "end": v(-5.42, 4.06) * mm});
            skLineSegment(sketch, "E1453", {"start": v(-0.68, 3.9) * mm, "end": v(-0.85, 4.06) * mm});
            skLineSegment(sketch, "E1454", {"start": v(-0.68, 3.9) * mm, "end": v(-0.5, 4.06) * mm});
            skLineSegment(sketch, "E1455", {"start": v(-0.34, 3.9) * mm, "end": v(-0.34, 4.06) * mm});
            skLineSegment(sketch, "E1456", {"start": v(0.68, 3.9) * mm, "end": v(0.5, 3.9) * mm});
            skLineSegment(sketch, "E1457", {"start": v(0.68, 3.9) * mm, "end": v(0.68, 4.06) * mm});
            skLineSegment(sketch, "E1458", {"start": v(5.42, 4.23) * mm, "end": v(5.42, 4.06) * mm});
            skLineSegment(sketch, "E1459", {"start": v(5.42, 4.06) * mm, "end": v(5.59, 3.9) * mm});
            skLineSegment(sketch, "E1460", {"start": v(5.59, 3.9) * mm, "end": v(5.76, 4.06) * mm});
            skLineSegment(sketch, "E1461", {"start": v(5.93, 3.9) * mm, "end": v(5.93, 4.06) * mm});
            skLineSegment(sketch, "E1462", {"start": v(6.43, 3.9) * mm, "end": v(6.43, 4.06) * mm});
            skLineSegment(sketch, "E1463", {"start": v(11, 3.9) * mm, "end": v(11, 4.06) * mm});
            skLineSegment(sketch, "E1464", {"start": v(12.2, 3.9) * mm, "end": v(12.2, 4.06) * mm});
            skLineSegment(sketch, "E1465", {"start": v(-10.5, 3.73) * mm, "end": v(-10.5, 3.9) * mm});
            skLineSegment(sketch, "E1466", {"start": v(-10.33, 3.73) * mm, "end": v(-10.5, 3.73) * mm});
            skLineSegment(sketch, "E1467", {"start": v(-10.16, 3.73) * mm, "end": v(-10.33, 3.73) * mm});
            skLineSegment(sketch, "E1468", {"start": v(-10.16, 3.73) * mm, "end": v(-10, 3.9) * mm});
            skLineSegment(sketch, "E1469", {"start": v(-9.82, 3.73) * mm, "end": v(-10, 3.9) * mm});
            skLineSegment(sketch, "E1470", {"start": v(-6.94, 3.73) * mm, "end": v(-6.94, 4.23) * mm});
            skLineSegment(sketch, "E1471", {"start": v(-6.43, 3.73) * mm, "end": v(-6.6, 3.73) * mm});
            skLineSegment(sketch, "E1472", {"start": v(-6.43, 3.73) * mm, "end": v(-6.43, 3.9) * mm});
            skLineSegment(sketch, "E1473", {"start": v(-5.93, 3.73) * mm, "end": v(-5.93, 3.9) * mm});
            skLineSegment(sketch, "E1474", {"start": v(-1.19, 3.73) * mm, "end": v(-1.02, 4.06) * mm});
            skLineSegment(sketch, "E1475", {"start": v(0.85, 3.73) * mm, "end": v(0.68, 3.9) * mm});
            skLineSegment(sketch, "E1476", {"start": v(5.93, 3.9) * mm, "end": v(6.1, 3.73) * mm});
            skLineSegment(sketch, "E1477", {"start": v(6.1, 3.73) * mm, "end": v(6.43, 3.9) * mm});
            skLineSegment(sketch, "E1478", {"start": v(11, 3.73) * mm, "end": v(11, 3.9) * mm});
            skLineSegment(sketch, "E1479", {"start": v(11.18, 3.73) * mm, "end": v(11, 3.73) * mm});
            skLineSegment(sketch, "E1480", {"start": v(12.02, 3.73) * mm, "end": v(11.18, 3.73) * mm});
            skLineSegment(sketch, "E1481", {"start": v(12.2, 3.73) * mm, "end": v(12.02, 3.73) * mm});
            skLineSegment(sketch, "E1482", {"start": v(12.2, 3.73) * mm, "end": v(12.2, 3.9) * mm});
            skLineSegment(sketch, "E1483", {"start": v(-10.5, 3.56) * mm, "end": v(-10.5, 3.73) * mm});
            skLineSegment(sketch, "E1484", {"start": v(-10, 3.56) * mm, "end": v(-10.16, 3.73) * mm});
            skLineSegment(sketch, "E1485", {"start": v(-10, 3.56) * mm, "end": v(-9.82, 3.73) * mm});
            skLineSegment(sketch, "E1486", {"start": v(-9.65, 3.56) * mm, "end": v(-9.82, 3.73) * mm});
            skLineSegment(sketch, "E1487", {"start": v(-7.11, 3.56) * mm, "end": v(-6.94, 3.73) * mm});
            skLineSegment(sketch, "E1488", {"start": v(-6.77, 3.56) * mm, "end": v(-6.94, 3.73) * mm});
            skLineSegment(sketch, "E1489", {"start": v(-6.77, 3.56) * mm, "end": v(-6.6, 3.73) * mm});
            skLineSegment(sketch, "E1490", {"start": v(-6.43, 3.73) * mm, "end": v(-6.27, 3.56) * mm});
            skLineSegment(sketch, "E1491", {"start": v(-6.27, 3.56) * mm, "end": v(-5.93, 3.73) * mm});
            skLineSegment(sketch, "E1492", {"start": v(-1.19, 3.56) * mm, "end": v(-1.35, 3.56) * mm});
            skLineSegment(sketch, "E1493", {"start": v(-1.19, 3.56) * mm, "end": v(-1.19, 3.73) * mm});
            skLineSegment(sketch, "E1494", {"start": v(-0.5, 3.56) * mm, "end": v(-0.68, 3.9) * mm});
            skLineSegment(sketch, "E1495", {"start": v(-0.5, 3.56) * mm, "end": v(-0.34, 3.9) * mm});
            skLineSegment(sketch, "E1496", {"start": v(0.34, 3.56) * mm, "end": v(0.5, 3.9) * mm});
            skLineSegment(sketch, "E1497", {"start": v(0.85, 3.56) * mm, "end": v(0.68, 3.56) * mm});
            skLineSegment(sketch, "E1498", {"start": v(0.85, 3.56) * mm, "end": v(0.85, 3.73) * mm});
            skLineSegment(sketch, "E1499", {"start": v(1.02, 3.56) * mm, "end": v(0.85, 3.56) * mm});
            skLineSegment(sketch, "E1500", {"start": v(11, 3.56) * mm, "end": v(11, 3.73) * mm});
            skLineSegment(sketch, "E1501", {"start": v(12.2, 3.56) * mm, "end": v(12.2, 3.73) * mm});
            skLineSegment(sketch, "E1502", {"start": v(-10.16, 3.39) * mm, "end": v(-10, 3.56) * mm});
            skLineSegment(sketch, "E1503", {"start": v(-9.65, 3.39) * mm, "end": v(-9.65, 3.56) * mm});
            skLineSegment(sketch, "E1504", {"start": v(-9.48, 3.39) * mm, "end": v(-9.65, 3.39) * mm});
            skLineSegment(sketch, "E1505", {"start": v(-6.94, 3.39) * mm, "end": v(-7.11, 3.56) * mm});
            skLineSegment(sketch, "E1506", {"start": v(-6.94, 3.39) * mm, "end": v(-6.77, 3.56) * mm});
            skLineSegment(sketch, "E1507", {"start": v(-1.02, 3.39) * mm, "end": v(-1.19, 3.56) * mm});
            skLineSegment(sketch, "E1508", {"start": v(-0.5, 3.39) * mm, "end": v(-0.68, 3.39) * mm});
            skLineSegment(sketch, "E1509", {"start": v(-0.5, 3.39) * mm, "end": v(-0.5, 3.56) * mm});
            skLineSegment(sketch, "E1510", {"start": v(0.34, 3.39) * mm, "end": v(0.34, 3.56) * mm});
            skLineSegment(sketch, "E1511", {"start": v(0.5, 3.39) * mm, "end": v(0.34, 3.39) * mm});
            skLineSegment(sketch, "E1512", {"start": v(0.5, 3.39) * mm, "end": v(0.68, 3.56) * mm});
            skLineSegment(sketch, "E1513", {"start": v(0.85, 3.39) * mm, "end": v(0.85, 3.56) * mm});
            skLineSegment(sketch, "E1514", {"start": v(11, 3.39) * mm, "end": v(11, 3.56) * mm});
            skLineSegment(sketch, "E1515", {"start": v(11.18, 3.39) * mm, "end": v(11, 3.39) * mm});
            skLineSegment(sketch, "E1516", {"start": v(12.2, 3.39) * mm, "end": v(12.2, 3.56) * mm});
            skLineSegment(sketch, "E1517", {"start": v(-23.37, 3.22) * mm, "end": v(-23.37, 4.4) * mm});
            skLineSegment(sketch, "E1518", {"start": v(-23.37, 4.4) * mm, "end": v(-23.2, 4.57) * mm});
            skLineSegment(sketch, "E1519", {"start": v(-23.03, 3.22) * mm, "end": v(-22.86, 4.4) * mm});
            skLineSegment(sketch, "E1520", {"start": v(-22.86, 4.4) * mm, "end": v(-23.03, 4.57) * mm});
            skLineSegment(sketch, "E1521", {"start": v(-10.33, 3.22) * mm, "end": v(-10.5, 3.56) * mm});
            skLineSegment(sketch, "E1522", {"start": v(-10.33, 3.22) * mm, "end": v(-10.16, 3.39) * mm});
            skLineSegment(sketch, "E1523", {"start": v(-10, 3.22) * mm, "end": v(-10.16, 3.39) * mm});
            skLineSegment(sketch, "E1524", {"start": v(-9.82, 3.22) * mm, "end": v(-10, 3.22) * mm});
            skLineSegment(sketch, "E1525", {"start": v(-9.82, 3.22) * mm, "end": v(-9.65, 3.39) * mm});
            skLineSegment(sketch, "E1526", {"start": v(-9.31, 3.22) * mm, "end": v(-9.48, 3.39) * mm});
            skLineSegment(sketch, "E1527", {"start": v(-1.7, 3.22) * mm, "end": v(-1.7, 3.39) * mm});
            skLineSegment(sketch, "E1528", {"start": v(-1.7, 3.39) * mm, "end": v(-1.35, 3.56) * mm});
            skLineSegment(sketch, "E1529", {"start": v(-1.02, 3.22) * mm, "end": v(-1.02, 3.39) * mm});
            skLineSegment(sketch, "E1530", {"start": v(-0.85, 3.22) * mm, "end": v(-1.02, 3.22) * mm});
            skLineSegment(sketch, "E1531", {"start": v(-0.85, 3.22) * mm, "end": v(-0.68, 3.39) * mm});
            skLineSegment(sketch, "E1532", {"start": v(0.34, 3.22) * mm, "end": v(0.34, 3.39) * mm});
            skLineSegment(sketch, "E1533", {"start": v(0.68, 3.22) * mm, "end": v(0.5, 3.39) * mm});
            skLineSegment(sketch, "E1534", {"start": v(0.68, 3.22) * mm, "end": v(0.85, 3.39) * mm});
            skLineSegment(sketch, "E1535", {"start": v(1.35, 3.22) * mm, "end": v(1.02, 3.56) * mm});
            skLineSegment(sketch, "E1536", {"start": v(11, 3.22) * mm, "end": v(11, 3.39) * mm});
            skLineSegment(sketch, "E1537", {"start": v(12.02, 3.22) * mm, "end": v(11.18, 3.39) * mm});
            skLineSegment(sketch, "E1538", {"start": v(12.2, 3.22) * mm, "end": v(12.02, 3.22) * mm});
            skLineSegment(sketch, "E1539", {"start": v(12.2, 3.22) * mm, "end": v(12.2, 3.39) * mm});
            skLineSegment(sketch, "E1540", {"start": v(-23.2, 3.05) * mm, "end": v(-23.37, 3.22) * mm});
            skLineSegment(sketch, "E1541", {"start": v(-23.03, 3.05) * mm, "end": v(-23.2, 3.05) * mm});
            skLineSegment(sketch, "E1542", {"start": v(-23.03, 3.05) * mm, "end": v(-23.03, 3.22) * mm});
            skLineSegment(sketch, "E1543", {"start": v(-10.16, 3.05) * mm, "end": v(-10.33, 3.22) * mm});
            skLineSegment(sketch, "E1544", {"start": v(-10.16, 3.05) * mm, "end": v(-10, 3.22) * mm});
            skLineSegment(sketch, "E1545", {"start": v(-9.65, 3.05) * mm, "end": v(-9.82, 3.22) * mm});
            skLineSegment(sketch, "E1546", {"start": v(-9.48, 3.05) * mm, "end": v(-9.65, 3.05) * mm});
            skLineSegment(sketch, "E1547", {"start": v(-9.31, 3.05) * mm, "end": v(-9.48, 3.05) * mm});
            skLineSegment(sketch, "E1548", {"start": v(-9.31, 3.05) * mm, "end": v(-9.31, 3.22) * mm});
            skLineSegment(sketch, "E1549", {"start": v(-2.03, 3.05) * mm, "end": v(-2.2, 3.05) * mm});
            skLineSegment(sketch, "E1550", {"start": v(-1.86, 3.05) * mm, "end": v(-2.03, 3.05) * mm});
            skLineSegment(sketch, "E1551", {"start": v(-1.86, 3.05) * mm, "end": v(-1.7, 3.22) * mm});
            skLineSegment(sketch, "E1552", {"start": v(-1.52, 3.05) * mm, "end": v(-1.7, 3.22) * mm});
            skLineSegment(sketch, "E1553", {"start": v(-1.19, 3.05) * mm, "end": v(-1.35, 3.22) * mm});
            skLineSegment(sketch, "E1554", {"start": v(-1.35, 3.22) * mm, "end": v(-1.52, 3.05) * mm});
            skLineSegment(sketch, "E1555", {"start": v(-1.19, 3.05) * mm, "end": v(-1.02, 3.22) * mm});
            skLineSegment(sketch, "E1556", {"start": v(0.5, 3.05) * mm, "end": v(0.34, 3.22) * mm});
            skLineSegment(sketch, "E1557", {"start": v(0.5, 3.05) * mm, "end": v(0.68, 3.22) * mm});
            skLineSegment(sketch, "E1558", {"start": v(0.85, 3.05) * mm, "end": v(0.68, 3.22) * mm});
            skLineSegment(sketch, "E1559", {"start": v(1.35, 3.05) * mm, "end": v(1.35, 3.22) * mm});
            skLineSegment(sketch, "E1560", {"start": v(1.52, 3.05) * mm, "end": v(1.35, 3.05) * mm});
            skLineSegment(sketch, "E1561", {"start": v(11, 3.05) * mm, "end": v(11, 3.22) * mm});
            skLineSegment(sketch, "E1562", {"start": v(11.18, 3.05) * mm, "end": v(11, 3.05) * mm});
            skLineSegment(sketch, "E1563", {"start": v(12.2, 3.05) * mm, "end": v(12.2, 3.22) * mm});
            skLineSegment(sketch, "E1564", {"start": v(-23.03, 2.88) * mm, "end": v(-23.03, 3.05) * mm});
            skLineSegment(sketch, "E1565", {"start": v(-10.16, 2.88) * mm, "end": v(-10.16, 3.05) * mm});
            skLineSegment(sketch, "E1566", {"start": v(-10, 2.88) * mm, "end": v(-10.16, 2.88) * mm});
            skLineSegment(sketch, "E1567", {"start": v(-9.82, 2.88) * mm, "end": v(-10, 2.88) * mm});
            skLineSegment(sketch, "E1568", {"start": v(-9.65, 2.88) * mm, "end": v(-9.82, 2.88) * mm});
            skLineSegment(sketch, "E1569", {"start": v(-9.65, 2.88) * mm, "end": v(-9.65, 3.05) * mm});
            skLineSegment(sketch, "E1570", {"start": v(-2.03, 2.88) * mm, "end": v(-2.03, 3.05) * mm});
            skLineSegment(sketch, "E1571", {"start": v(-1.7, 2.88) * mm, "end": v(-1.86, 3.05) * mm});
            skLineSegment(sketch, "E1572", {"start": v(-1.7, 2.88) * mm, "end": v(-1.52, 3.05) * mm});
            skLineSegment(sketch, "E1573", {"start": v(-1.35, 2.88) * mm, "end": v(-1.52, 3.05) * mm});
            skLineSegment(sketch, "E1574", {"start": v(-1.35, 2.88) * mm, "end": v(-1.19, 3.05) * mm});
            skLineSegment(sketch, "E1575", {"start": v(-1.02, 2.88) * mm, "end": v(-1.19, 3.05) * mm});
            skLineSegment(sketch, "E1576", {"start": v(-0.5, 2.88) * mm, "end": v(-0.85, 3.22) * mm});
            skLineSegment(sketch, "E1577", {"start": v(-0.5, 2.88) * mm, "end": v(-0.34, 3.05) * mm});
            skLineSegment(sketch, "E1578", {"start": v(-0.34, 3.05) * mm, "end": v(-0.5, 3.39) * mm});
            skLineSegment(sketch, "E1579", {"start": v(0.34, 2.88) * mm, "end": v(0.17, 3.05) * mm});
            skLineSegment(sketch, "E1580", {"start": v(0.17, 3.05) * mm, "end": v(0.34, 3.22) * mm});
            skLineSegment(sketch, "E1581", {"start": v(0.34, 2.88) * mm, "end": v(0.5, 3.05) * mm});
            skLineSegment(sketch, "E1582", {"start": v(0.68, 2.88) * mm, "end": v(0.5, 3.05) * mm});
            skLineSegment(sketch, "E1583", {"start": v(0.85, 2.88) * mm, "end": v(0.68, 2.88) * mm});
            skLineSegment(sketch, "E1584", {"start": v(0.85, 2.88) * mm, "end": v(0.85, 3.05) * mm});
            skLineSegment(sketch, "E1585", {"start": v(1.19, 2.88) * mm, "end": v(1.35, 3.05) * mm});
            skLineSegment(sketch, "E1586", {"start": v(2.03, 2.88) * mm, "end": v(1.86, 3.05) * mm});
            skLineSegment(sketch, "E1587", {"start": v(1.86, 3.05) * mm, "end": v(1.52, 3.05) * mm});
            skLineSegment(sketch, "E1588", {"start": v(11, 2.88) * mm, "end": v(11, 3.05) * mm});
            skLineSegment(sketch, "E1589", {"start": v(11.18, 3.05) * mm, "end": v(11.35, 2.88) * mm});
            skLineSegment(sketch, "E1590", {"start": v(11.35, 2.88) * mm, "end": v(12.02, 2.88) * mm});
            skLineSegment(sketch, "E1591", {"start": v(12.02, 2.88) * mm, "end": v(12.2, 3.05) * mm});
            skLineSegment(sketch, "E1592", {"start": v(12.36, 2.88) * mm, "end": v(12.2, 3.05) * mm});
            skLineSegment(sketch, "E1593", {"start": v(12.36, 2.88) * mm, "end": v(12.73, 3.18) * mm});
            skLineSegment(sketch, "E1594", {"start": v(12.73, 3.18) * mm, "end": v(14.92, 4.37) * mm});
            skLineSegment(sketch, "E1595", {"start": v(14.92, 4.37) * mm, "end": v(15.07, 4.4) * mm});
            skLineSegment(sketch, "E1596", {"start": v(-10.16, 2.7) * mm, "end": v(-10.16, 2.88) * mm});
            skLineSegment(sketch, "E1597", {"start": v(-9.48, 2.7) * mm, "end": v(-9.65, 2.88) * mm});
            skLineSegment(sketch, "E1598", {"start": v(-9.31, 2.7) * mm, "end": v(-9.48, 2.7) * mm});
            skLineSegment(sketch, "E1599", {"start": v(-9.31, 2.7) * mm, "end": v(-9.14, 2.88) * mm});
            skLineSegment(sketch, "E1600", {"start": v(-9.14, 2.88) * mm, "end": v(-9.31, 3.05) * mm});
            skLineSegment(sketch, "E1601", {"start": v(-2.03, 2.7) * mm, "end": v(-2.03, 2.88) * mm});
            skLineSegment(sketch, "E1602", {"start": v(-1.86, 2.7) * mm, "end": v(-2.03, 2.7) * mm});
            skLineSegment(sketch, "E1603", {"start": v(-1.86, 2.7) * mm, "end": v(-1.7, 2.88) * mm});
            skLineSegment(sketch, "E1604", {"start": v(-1.52, 2.7) * mm, "end": v(-1.7, 2.88) * mm});
            skLineSegment(sketch, "E1605", {"start": v(-1.52, 2.7) * mm, "end": v(-1.35, 2.88) * mm});
            skLineSegment(sketch, "E1606", {"start": v(-1.19, 2.7) * mm, "end": v(-1.35, 2.88) * mm});
            skLineSegment(sketch, "E1607", {"start": v(-1.19, 2.7) * mm, "end": v(-1.02, 2.88) * mm});
            skLineSegment(sketch, "E1608", {"start": v(1.02, 2.7) * mm, "end": v(0.85, 2.88) * mm});
            skLineSegment(sketch, "E1609", {"start": v(1.02, 2.7) * mm, "end": v(1.19, 2.88) * mm});
            skLineSegment(sketch, "E1610", {"start": v(11, 2.7) * mm, "end": v(11, 2.88) * mm});
            skLineSegment(sketch, "E1611", {"start": v(-10.33, 2.54) * mm, "end": v(-10.16, 2.7) * mm});
            skLineSegment(sketch, "E1612", {"start": v(-10, 2.54) * mm, "end": v(-10.16, 2.7) * mm});
            skLineSegment(sketch, "E1613", {"start": v(-9.65, 2.54) * mm, "end": v(-10, 2.54) * mm});
            skLineSegment(sketch, "E1614", {"start": v(-9.65, 2.54) * mm, "end": v(-9.48, 2.7) * mm});
            skLineSegment(sketch, "E1615", {"start": v(-9.14, 2.54) * mm, "end": v(-9.31, 2.7) * mm});
            skLineSegment(sketch, "E1616", {"start": v(-2.03, 2.54) * mm, "end": v(-2.03, 2.7) * mm});
            skLineSegment(sketch, "E1617", {"start": v(-1.7, 2.54) * mm, "end": v(-1.86, 2.7) * mm});
            skLineSegment(sketch, "E1618", {"start": v(-1.7, 2.54) * mm, "end": v(-1.52, 2.7) * mm});
            skLineSegment(sketch, "E1619", {"start": v(-1.35, 2.54) * mm, "end": v(-1.52, 2.7) * mm});
            skLineSegment(sketch, "E1620", {"start": v(-1.35, 2.54) * mm, "end": v(-1.19, 2.7) * mm});
            skLineSegment(sketch, "E1621", {"start": v(-1.02, 2.54) * mm, "end": v(-1.19, 2.7) * mm});
            skLineSegment(sketch, "E1622", {"start": v(-1.02, 2.54) * mm, "end": v(-0.85, 2.7) * mm});
            skLineSegment(sketch, "E1623", {"start": v(-0.85, 2.7) * mm, "end": v(-1.02, 2.88) * mm});
            skLineSegment(sketch, "E1624", {"start": v(0.34, 2.54) * mm, "end": v(0.34, 2.88) * mm});
            skLineSegment(sketch, "E1625", {"start": v(1.52, 2.54) * mm, "end": v(1.19, 2.88) * mm});
            skLineSegment(sketch, "E1626", {"start": v(1.7, 2.54) * mm, "end": v(1.52, 2.54) * mm});
            skLineSegment(sketch, "E1627", {"start": v(1.7, 2.54) * mm, "end": v(2.03, 2.88) * mm});
            skLineSegment(sketch, "E1628", {"start": v(10.84, 2.54) * mm, "end": v(11, 2.7) * mm});
            skLineSegment(sketch, "E1629", {"start": v(11.18, 2.54) * mm, "end": v(11, 2.7) * mm});
            skLineSegment(sketch, "E1630", {"start": v(-10.33, 2.37) * mm, "end": v(-10.33, 2.54) * mm});
            skLineSegment(sketch, "E1631", {"start": v(-10.16, 2.37) * mm, "end": v(-10.33, 2.37) * mm});
            skLineSegment(sketch, "E1632", {"start": v(-10.16, 2.37) * mm, "end": v(-10, 2.54) * mm});
            skLineSegment(sketch, "E1633", {"start": v(-9.48, 2.37) * mm, "end": v(-9.65, 2.54) * mm});
            skLineSegment(sketch, "E1634", {"start": v(-9.31, 2.37) * mm, "end": v(-9.48, 2.37) * mm});
            skLineSegment(sketch, "E1635", {"start": v(-9.31, 2.37) * mm, "end": v(-9.14, 2.54) * mm});
            skLineSegment(sketch, "E1636", {"start": v(-8.8, 2.37) * mm, "end": v(-9.14, 2.54) * mm});
            skLineSegment(sketch, "E1637", {"start": v(-1.86, 2.37) * mm, "end": v(-2.03, 2.54) * mm});
            skLineSegment(sketch, "E1638", {"start": v(-1.86, 2.37) * mm, "end": v(-1.7, 2.54) * mm});
            skLineSegment(sketch, "E1639", {"start": v(-1.52, 2.37) * mm, "end": v(-1.7, 2.54) * mm});
            skLineSegment(sketch, "E1640", {"start": v(-1.52, 2.37) * mm, "end": v(-1.35, 2.54) * mm});
            skLineSegment(sketch, "E1641", {"start": v(-1.19, 2.37) * mm, "end": v(-1.35, 2.54) * mm});
            skLineSegment(sketch, "E1642", {"start": v(-1.19, 2.37) * mm, "end": v(-1.02, 2.54) * mm});
            skLineSegment(sketch, "E1643", {"start": v(-0.68, 2.37) * mm, "end": v(-0.5, 2.54) * mm});
            skLineSegment(sketch, "E1644", {"start": v(-0.5, 2.54) * mm, "end": v(-0.5, 2.88) * mm});
            skLineSegment(sketch, "E1645", {"start": v(0.34, 2.37) * mm, "end": v(0.34, 2.54) * mm});
            skLineSegment(sketch, "E1646", {"start": v(0.5, 2.37) * mm, "end": v(0.34, 2.37) * mm});
            skLineSegment(sketch, "E1647", {"start": v(0.85, 2.37) * mm, "end": v(1.02, 2.7) * mm});
            skLineSegment(sketch, "E1648", {"start": v(1.7, 2.37) * mm, "end": v(1.7, 2.54) * mm});
            skLineSegment(sketch, "E1649", {"start": v(10.84, 2.37) * mm, "end": v(10.84, 2.54) * mm});
            skLineSegment(sketch, "E1650", {"start": v(11, 2.37) * mm, "end": v(10.84, 2.37) * mm});
            skLineSegment(sketch, "E1651", {"start": v(11, 2.37) * mm, "end": v(11.18, 2.54) * mm});
            skLineSegment(sketch, "E1652", {"start": v(11.35, 2.37) * mm, "end": v(11.18, 2.54) * mm});
            skLineSegment(sketch, "E1653", {"start": v(12.02, 2.37) * mm, "end": v(11.85, 2.54) * mm});
            skLineSegment(sketch, "E1654", {"start": v(11.85, 2.54) * mm, "end": v(11.51, 2.54) * mm});
            skLineSegment(sketch, "E1655", {"start": v(11.51, 2.54) * mm, "end": v(11.35, 2.37) * mm});
            skLineSegment(sketch, "E1656", {"start": v(12.02, 2.37) * mm, "end": v(12.36, 2.7) * mm});
            skLineSegment(sketch, "E1657", {"start": v(12.36, 2.7) * mm, "end": v(12.36, 2.88) * mm});
            skLineSegment(sketch, "E1658", {"start": v(-10.33, 2.2) * mm, "end": v(-10.33, 2.37) * mm});
            skLineSegment(sketch, "E1659", {"start": v(-10, 2.2) * mm, "end": v(-10.16, 2.37) * mm});
            skLineSegment(sketch, "E1660", {"start": v(-9.65, 2.2) * mm, "end": v(-9.48, 2.37) * mm});
            skLineSegment(sketch, "E1661", {"start": v(-9.31, 2.2) * mm, "end": v(-9.31, 2.37) * mm});
            skLineSegment(sketch, "E1662", {"start": v(-9.14, 2.2) * mm, "end": v(-9.31, 2.2) * mm});
            skLineSegment(sketch, "E1663", {"start": v(-8.97, 2.2) * mm, "end": v(-9.14, 2.2) * mm});
            skLineSegment(sketch, "E1664", {"start": v(-8.8, 2.2) * mm, "end": v(-8.97, 2.2) * mm});
            skLineSegment(sketch, "E1665", {"start": v(-8.8, 2.2) * mm, "end": v(-8.8, 2.37) * mm});
            skLineSegment(sketch, "E1666", {"start": v(-1.86, 2.2) * mm, "end": v(-2.03, 2.2) * mm});
            skLineSegment(sketch, "E1667", {"start": v(-1.86, 2.2) * mm, "end": v(-1.86, 2.37) * mm});
            skLineSegment(sketch, "E1668", {"start": v(-1.7, 2.2) * mm, "end": v(-1.86, 2.2) * mm});
            skLineSegment(sketch, "E1669", {"start": v(-1.7, 2.2) * mm, "end": v(-1.52, 2.37) * mm});
            skLineSegment(sketch, "E1670", {"start": v(-1.35, 2.2) * mm, "end": v(-1.52, 2.37) * mm});
            skLineSegment(sketch, "E1671", {"start": v(-1.19, 2.2) * mm, "end": v(-1.35, 2.2) * mm});
            skLineSegment(sketch, "E1672", {"start": v(-1.19, 2.2) * mm, "end": v(-1.19, 2.37) * mm});
            skLineSegment(sketch, "E1673", {"start": v(-0.68, 2.2) * mm, "end": v(-0.85, 2.2) * mm});
            skLineSegment(sketch, "E1674", {"start": v(-0.68, 2.2) * mm, "end": v(-0.68, 2.37) * mm});
            skLineSegment(sketch, "E1675", {"start": v(0.68, 2.2) * mm, "end": v(0.5, 2.37) * mm});
            skLineSegment(sketch, "E1676", {"start": v(0.68, 2.2) * mm, "end": v(0.85, 2.37) * mm});
            skLineSegment(sketch, "E1677", {"start": v(1.02, 2.2) * mm, "end": v(0.85, 2.37) * mm});
            skLineSegment(sketch, "E1678", {"start": v(1.19, 2.2) * mm, "end": v(1.02, 2.2) * mm});
            skLineSegment(sketch, "E1679", {"start": v(1.52, 2.2) * mm, "end": v(1.19, 2.2) * mm});
            skLineSegment(sketch, "E1680", {"start": v(1.7, 2.2) * mm, "end": v(1.52, 2.2) * mm});
            skLineSegment(sketch, "E1681", {"start": v(1.7, 2.2) * mm, "end": v(1.7, 2.37) * mm});
            skLineSegment(sketch, "E1682", {"start": v(10.84, 2.2) * mm, "end": v(10.84, 2.37) * mm});
            skLineSegment(sketch, "E1683", {"start": v(11.35, 2.2) * mm, "end": v(11.35, 2.37) * mm});
            skLineSegment(sketch, "E1684", {"start": v(12.02, 2.2) * mm, "end": v(11.85, 2.2) * mm});
            skLineSegment(sketch, "E1685", {"start": v(12.02, 2.2) * mm, "end": v(12.02, 2.37) * mm});
            skLineSegment(sketch, "E1686", {"start": v(-10.16, 2.03) * mm, "end": v(-10.33, 2.2) * mm});
            skLineSegment(sketch, "E1687", {"start": v(-10.16, 2.03) * mm, "end": v(-10, 2.2) * mm});
            skLineSegment(sketch, "E1688", {"start": v(-9.82, 2.03) * mm, "end": v(-10, 2.2) * mm});
            skLineSegment(sketch, "E1689", {"start": v(-9.82, 2.03) * mm, "end": v(-9.65, 2.2) * mm});
            skLineSegment(sketch, "E1690", {"start": v(-9.48, 2.03) * mm, "end": v(-9.65, 2.2) * mm});
            skLineSegment(sketch, "E1691", {"start": v(-9.48, 2.03) * mm, "end": v(-9.31, 2.2) * mm});
            skLineSegment(sketch, "E1692", {"start": v(-1.86, 2.03) * mm, "end": v(-1.86, 2.2) * mm});
            skLineSegment(sketch, "E1693", {"start": v(-1.52, 2.03) * mm, "end": v(-1.7, 2.2) * mm});
            skLineSegment(sketch, "E1694", {"start": v(-1.52, 2.03) * mm, "end": v(-1.35, 2.2) * mm});
            skLineSegment(sketch, "E1695", {"start": v(-1.02, 2.03) * mm, "end": v(-1.19, 2.2) * mm});
            skLineSegment(sketch, "E1696", {"start": v(-1.02, 2.03) * mm, "end": v(-0.85, 2.2) * mm});
            skLineSegment(sketch, "E1697", {"start": v(0.5, 2.03) * mm, "end": v(0.68, 2.2) * mm});
            skLineSegment(sketch, "E1698", {"start": v(1.02, 2.03) * mm, "end": v(1.02, 2.2) * mm});
            skLineSegment(sketch, "E1699", {"start": v(1.7, 2.03) * mm, "end": v(1.7, 2.2) * mm});
            skLineSegment(sketch, "E1700", {"start": v(10.84, 2.03) * mm, "end": v(10.84, 2.2) * mm});
            skLineSegment(sketch, "E1701", {"start": v(11, 2.03) * mm, "end": v(10.84, 2.03) * mm});
            skLineSegment(sketch, "E1702", {"start": v(11.18, 2.03) * mm, "end": v(11, 2.03) * mm});
            skLineSegment(sketch, "E1703", {"start": v(11.35, 2.03) * mm, "end": v(11.18, 2.03) * mm});
            skLineSegment(sketch, "E1704", {"start": v(11.35, 2.03) * mm, "end": v(11.35, 2.2) * mm});
            skLineSegment(sketch, "E1705", {"start": v(11.51, 2.03) * mm, "end": v(11.35, 2.03) * mm});
            skLineSegment(sketch, "E1706", {"start": v(11.51, 2.03) * mm, "end": v(11.85, 2.2) * mm});
            skLineSegment(sketch, "E1707", {"start": v(12.02, 2.03) * mm, "end": v(12.02, 2.2) * mm});
            skLineSegment(sketch, "E1708", {"start": v(-10.16, 1.86) * mm, "end": v(-10.16, 2.03) * mm});
            skLineSegment(sketch, "E1709", {"start": v(-9.82, 1.86) * mm, "end": v(-9.82, 2.03) * mm});
            skLineSegment(sketch, "E1710", {"start": v(-9.31, 1.86) * mm, "end": v(-9.48, 2.03) * mm});
            skLineSegment(sketch, "E1711", {"start": v(-2.03, 1.86) * mm, "end": v(-2.2, 2.03) * mm});
            skLineSegment(sketch, "E1712", {"start": v(-2.2, 2.03) * mm, "end": v(-2.03, 2.2) * mm});
            skLineSegment(sketch, "E1713", {"start": v(-2.03, 1.86) * mm, "end": v(-1.86, 2.03) * mm});
            skLineSegment(sketch, "E1714", {"start": v(-1.7, 1.86) * mm, "end": v(-1.86, 2.03) * mm});
            skLineSegment(sketch, "E1715", {"start": v(-1.7, 1.86) * mm, "end": v(-1.52, 2.03) * mm});
            skLineSegment(sketch, "E1716", {"start": v(-1.02, 1.86) * mm, "end": v(-1.02, 2.03) * mm});
            skLineSegment(sketch, "E1717", {"start": v(0.34, 1.86) * mm, "end": v(0.17, 2.03) * mm});
            skLineSegment(sketch, "E1718", {"start": v(0.17, 2.03) * mm, "end": v(0.34, 2.37) * mm});
            skLineSegment(sketch, "E1719", {"start": v(0.5, 1.86) * mm, "end": v(0.34, 1.86) * mm});
            skLineSegment(sketch, "E1720", {"start": v(0.5, 1.86) * mm, "end": v(0.5, 2.03) * mm});
            skLineSegment(sketch, "E1721", {"start": v(1.7, 1.86) * mm, "end": v(1.52, 1.86) * mm});
            skLineSegment(sketch, "E1722", {"start": v(1.7, 1.86) * mm, "end": v(1.7, 2.03) * mm});
            skLineSegment(sketch, "E1723", {"start": v(10.84, 1.86) * mm, "end": v(10.84, 2.03) * mm});
            skLineSegment(sketch, "E1724", {"start": v(11.68, 1.86) * mm, "end": v(11.51, 2.03) * mm});
            skLineSegment(sketch, "E1725", {"start": v(11.85, 1.86) * mm, "end": v(11.68, 1.86) * mm});
            skLineSegment(sketch, "E1726", {"start": v(12.02, 1.86) * mm, "end": v(11.85, 1.86) * mm});
            skLineSegment(sketch, "E1727", {"start": v(12.02, 1.86) * mm, "end": v(12.02, 2.03) * mm});
            skLineSegment(sketch, "E1728", {"start": v(-10.16, 1.7) * mm, "end": v(-10.16, 1.86) * mm});
            skLineSegment(sketch, "E1729", {"start": v(-10, 1.7) * mm, "end": v(-10.16, 1.7) * mm});
            skLineSegment(sketch, "E1730", {"start": v(-9.82, 1.7) * mm, "end": v(-10, 1.7) * mm});
            skLineSegment(sketch, "E1731", {"start": v(-9.82, 1.7) * mm, "end": v(-9.82, 1.86) * mm});
            skLineSegment(sketch, "E1732", {"start": v(-9.48, 1.7) * mm, "end": v(-9.31, 1.86) * mm});
            skLineSegment(sketch, "E1733", {"start": v(-9.14, 1.7) * mm, "end": v(-9.31, 1.86) * mm});
            skLineSegment(sketch, "E1734", {"start": v(-9.14, 1.7) * mm, "end": v(-8.97, 1.7) * mm});
            skLineSegment(sketch, "E1735", {"start": v(-8.97, 1.7) * mm, "end": v(-8.64, 2.03) * mm});
            skLineSegment(sketch, "E1736", {"start": v(-8.64, 2.03) * mm, "end": v(-8.8, 2.2) * mm});
            skLineSegment(sketch, "E1737", {"start": v(-2.03, 1.7) * mm, "end": v(-2.03, 1.86) * mm});
            skLineSegment(sketch, "E1738", {"start": v(-1.7, 1.7) * mm, "end": v(-1.7, 1.86) * mm});
            skLineSegment(sketch, "E1739", {"start": v(-1.02, 1.7) * mm, "end": v(-1.19, 1.7) * mm});
            skLineSegment(sketch, "E1740", {"start": v(-1.02, 1.7) * mm, "end": v(-1.02, 1.86) * mm});
            skLineSegment(sketch, "E1741", {"start": v(0.5, 1.7) * mm, "end": v(0.5, 1.86) * mm});
            skLineSegment(sketch, "E1742", {"start": v(1.02, 1.7) * mm, "end": v(1.02, 2.03) * mm});
            skLineSegment(sketch, "E1743", {"start": v(1.7, 1.7) * mm, "end": v(1.7, 1.86) * mm});
            skLineSegment(sketch, "E1744", {"start": v(10.84, 1.7) * mm, "end": v(10.84, 1.86) * mm});
            skLineSegment(sketch, "E1745", {"start": v(11.68, 1.7) * mm, "end": v(11.68, 1.86) * mm});
            skLineSegment(sketch, "E1746", {"start": v(12.02, 1.7) * mm, "end": v(12.02, 1.86) * mm});
            skLineSegment(sketch, "E1747", {"start": v(22.86, 1.7) * mm, "end": v(22.7, 1.86) * mm});
            skLineSegment(sketch, "E1748", {"start": v(22.7, 1.86) * mm, "end": v(22.7, 5.76) * mm});
            skLineSegment(sketch, "E1749", {"start": v(-10.16, 1.52) * mm, "end": v(-10.16, 1.7) * mm});
            skLineSegment(sketch, "E1750", {"start": v(-9.65, 1.52) * mm, "end": v(-9.82, 1.7) * mm});
            skLineSegment(sketch, "E1751", {"start": v(-9.65, 1.52) * mm, "end": v(-9.48, 1.7) * mm});
            skLineSegment(sketch, "E1752", {"start": v(-9.48, 1.7) * mm, "end": v(-9.31, 1.52) * mm});
            skLineSegment(sketch, "E1753", {"start": v(-9.31, 1.52) * mm, "end": v(-9.14, 1.7) * mm});
            skLineSegment(sketch, "E1754", {"start": v(-2.03, 1.52) * mm, "end": v(-2.03, 1.7) * mm});
            skLineSegment(sketch, "E1755", {"start": v(-1.86, 1.52) * mm, "end": v(-2.03, 1.52) * mm});
            skLineSegment(sketch, "E1756", {"start": v(-1.7, 1.52) * mm, "end": v(-1.86, 1.52) * mm});
            skLineSegment(sketch, "E1757", {"start": v(-1.7, 1.52) * mm, "end": v(-1.7, 1.7) * mm});
            skLineSegment(sketch, "E1758", {"start": v(-0.85, 1.52) * mm, "end": v(-1.02, 1.7) * mm});
            skLineSegment(sketch, "E1759", {"start": v(-0.5, 1.52) * mm, "end": v(-0.68, 1.7) * mm});
            skLineSegment(sketch, "E1760", {"start": v(-0.68, 1.7) * mm, "end": v(-0.85, 1.52) * mm});
            skLineSegment(sketch, "E1761", {"start": v(-0.5, 1.52) * mm, "end": v(-0.34, 1.7) * mm});
            skLineSegment(sketch, "E1762", {"start": v(-0.34, 1.7) * mm, "end": v(-0.34, 1.86) * mm});
            skLineSegment(sketch, "E1763", {"start": v(-0.34, 1.86) * mm, "end": v(-0.68, 2.2) * mm});
            skLineSegment(sketch, "E1764", {"start": v(0.68, 1.52) * mm, "end": v(0.5, 1.7) * mm});
            skLineSegment(sketch, "E1765", {"start": v(0.85, 1.52) * mm, "end": v(0.68, 1.52) * mm});
            skLineSegment(sketch, "E1766", {"start": v(0.85, 1.52) * mm, "end": v(1.02, 1.7) * mm});
            skLineSegment(sketch, "E1767", {"start": v(1.19, 1.52) * mm, "end": v(1.02, 1.7) * mm});
            skLineSegment(sketch, "E1768", {"start": v(1.19, 1.52) * mm, "end": v(1.52, 1.86) * mm});
            skLineSegment(sketch, "E1769", {"start": v(10.84, 1.52) * mm, "end": v(10.84, 1.7) * mm});
            skLineSegment(sketch, "E1770", {"start": v(11, 1.52) * mm, "end": v(10.84, 1.52) * mm});
            skLineSegment(sketch, "E1771", {"start": v(11.51, 1.52) * mm, "end": v(11, 1.52) * mm});
            skLineSegment(sketch, "E1772", {"start": v(11.51, 1.52) * mm, "end": v(11.68, 1.7) * mm});
            skLineSegment(sketch, "E1773", {"start": v(12.02, 1.52) * mm, "end": v(12.02, 1.7) * mm});
            skLineSegment(sketch, "E1774", {"start": v(22.86, 1.52) * mm, "end": v(22.86, 1.7) * mm});
            skLineSegment(sketch, "E1775", {"start": v(23.03, 1.52) * mm, "end": v(22.86, 1.52) * mm});
            skLineSegment(sketch, "E1776", {"start": v(23.7, 1.52) * mm, "end": v(23.54, 5.76) * mm});
            skLineSegment(sketch, "E1777", {"start": v(-10.16, 1.35) * mm, "end": v(-10.16, 1.52) * mm});
            skLineSegment(sketch, "E1778", {"start": v(-10, 1.35) * mm, "end": v(-10.16, 1.35) * mm});
            skLineSegment(sketch, "E1779", {"start": v(-2.03, 1.35) * mm, "end": v(-2.03, 1.52) * mm});
            skLineSegment(sketch, "E1780", {"start": v(-1.52, 1.35) * mm, "end": v(-1.7, 1.52) * mm});
            skLineSegment(sketch, "E1781", {"start": v(-1.52, 1.35) * mm, "end": v(-1.19, 1.7) * mm});
            skLineSegment(sketch, "E1782", {"start": v(-1.02, 1.35) * mm, "end": v(-0.85, 1.52) * mm});
            skLineSegment(sketch, "E1783", {"start": v(-0.68, 1.35) * mm, "end": v(-0.85, 1.52) * mm});
            skLineSegment(sketch, "E1784", {"start": v(-0.5, 1.35) * mm, "end": v(-0.68, 1.35) * mm});
            skLineSegment(sketch, "E1785", {"start": v(-0.5, 1.35) * mm, "end": v(-0.5, 1.52) * mm});
            skLineSegment(sketch, "E1786", {"start": v(0.68, 1.35) * mm, "end": v(0.68, 1.52) * mm});
            skLineSegment(sketch, "E1787", {"start": v(1.7, 1.35) * mm, "end": v(1.86, 1.52) * mm});
            skLineSegment(sketch, "E1788", {"start": v(1.86, 1.52) * mm, "end": v(1.7, 1.7) * mm});
            skLineSegment(sketch, "E1789", {"start": v(10.84, 1.35) * mm, "end": v(10.84, 1.52) * mm});
            skLineSegment(sketch, "E1790", {"start": v(11.68, 1.35) * mm, "end": v(11.51, 1.52) * mm});
            skLineSegment(sketch, "E1791", {"start": v(11.85, 1.35) * mm, "end": v(11.68, 1.35) * mm});
            skLineSegment(sketch, "E1792", {"start": v(12.02, 1.35) * mm, "end": v(11.85, 1.35) * mm});
            skLineSegment(sketch, "E1793", {"start": v(12.02, 1.35) * mm, "end": v(12.02, 1.52) * mm});
            skLineSegment(sketch, "E1794", {"start": v(22.86, 1.35) * mm, "end": v(22.86, 1.52) * mm});
            skLineSegment(sketch, "E1795", {"start": v(23.2, 1.35) * mm, "end": v(23.03, 1.52) * mm});
            skLineSegment(sketch, "E1796", {"start": v(23.54, 1.35) * mm, "end": v(23.2, 1.35) * mm});
            skLineSegment(sketch, "E1797", {"start": v(23.7, 1.35) * mm, "end": v(23.54, 1.35) * mm});
            skLineSegment(sketch, "E1798", {"start": v(23.7, 1.35) * mm, "end": v(23.7, 1.52) * mm});
            skLineSegment(sketch, "E1799", {"start": v(-10.33, 1.19) * mm, "end": v(-10.5, 1.19) * mm});
            skLineSegment(sketch, "E1800", {"start": v(-10.5, 1.19) * mm, "end": v(-11.05, 2) * mm});
            skLineSegment(sketch, "E1801", {"start": v(-11.05, 2) * mm, "end": v(-11.35, 2.37) * mm});
            skLineSegment(sketch, "E1802", {"start": v(-10.33, 1.19) * mm, "end": v(-10.16, 1.35) * mm});
            skLineSegment(sketch, "E1803", {"start": v(-9.82, 1.19) * mm, "end": v(-10, 1.35) * mm});
            skLineSegment(sketch, "E1804", {"start": v(-9.82, 1.19) * mm, "end": v(-9.65, 1.52) * mm});
            skLineSegment(sketch, "E1805", {"start": v(-6.94, 1.19) * mm, "end": v(-7.11, 1.52) * mm});
            skLineSegment(sketch, "E1806", {"start": v(-7.11, 1.52) * mm, "end": v(-7.11, 2.88) * mm});
            skLineSegment(sketch, "E1807", {"start": v(-7.11, 2.88) * mm, "end": v(-6.94, 3.39) * mm});
            skLineSegment(sketch, "E1808", {"start": v(-2.03, 1.19) * mm, "end": v(-2.03, 1.35) * mm});
            skLineSegment(sketch, "E1809", {"start": v(-1.7, 1.19) * mm, "end": v(-1.52, 1.35) * mm});
            skLineSegment(sketch, "E1810", {"start": v(-1.35, 1.19) * mm, "end": v(-1.52, 1.35) * mm});
            skLineSegment(sketch, "E1811", {"start": v(-1.19, 1.19) * mm, "end": v(-1.35, 1.19) * mm});
            skLineSegment(sketch, "E1812", {"start": v(-1.19, 1.19) * mm, "end": v(-1.02, 1.35) * mm});
            skLineSegment(sketch, "E1813", {"start": v(-0.85, 1.19) * mm, "end": v(-1.02, 1.35) * mm});
            skLineSegment(sketch, "E1814", {"start": v(-0.85, 1.19) * mm, "end": v(-0.68, 1.35) * mm});
            skLineSegment(sketch, "E1815", {"start": v(1.7, 1.19) * mm, "end": v(1.7, 1.35) * mm});
            skLineSegment(sketch, "E1816", {"start": v(1.86, 1.19) * mm, "end": v(1.7, 1.19) * mm});
            skLineSegment(sketch, "E1817", {"start": v(10.84, 1.19) * mm, "end": v(10.84, 1.35) * mm});
            skLineSegment(sketch, "E1818", {"start": v(12.02, 1.19) * mm, "end": v(12.02, 1.35) * mm});
            skLineSegment(sketch, "E1819", {"start": v(22.86, 1.19) * mm, "end": v(22.86, 1.35) * mm});
            skLineSegment(sketch, "E1820", {"start": v(23.03, 1.19) * mm, "end": v(22.86, 1.19) * mm});
            skLineSegment(sketch, "E1821", {"start": v(23.03, 1.19) * mm, "end": v(23.2, 1.35) * mm});
            skLineSegment(sketch, "E1822", {"start": v(23.7, 1.19) * mm, "end": v(23.7, 1.35) * mm});
            skLineSegment(sketch, "E1823", {"start": v(-10.16, 1.02) * mm, "end": v(-10.33, 1.19) * mm});
            skLineSegment(sketch, "E1824", {"start": v(-9.82, 1.02) * mm, "end": v(-9.82, 1.19) * mm});
            skLineSegment(sketch, "E1825", {"start": v(-7.11, 1.02) * mm, "end": v(-7.62, 1.7) * mm});
            skLineSegment(sketch, "E1826", {"start": v(-7.62, 1.7) * mm, "end": v(-7.62, 2.54) * mm});
            skLineSegment(sketch, "E1827", {"start": v(-7.62, 2.54) * mm, "end": v(-7.4, 3.03) * mm});
            skLineSegment(sketch, "E1828", {"start": v(-7.4, 3.03) * mm, "end": v(-7.11, 3.56) * mm});
            skLineSegment(sketch, "E1829", {"start": v(-7.11, 1.02) * mm, "end": v(-6.94, 1.19) * mm});
            skLineSegment(sketch, "E1830", {"start": v(-6.77, 1.02) * mm, "end": v(-6.94, 1.19) * mm});
            skLineSegment(sketch, "E1831", {"start": v(-5.93, 1.02) * mm, "end": v(-4.4, 2.7) * mm});
            skLineSegment(sketch, "E1832", {"start": v(-4.4, 2.7) * mm, "end": v(-2.02, 4.03) * mm});
            skLineSegment(sketch, "E1833", {"start": v(-2.02, 4.03) * mm, "end": v(-1.7, 4.23) * mm});
            skLineSegment(sketch, "E1834", {"start": v(-4.74, 1.02) * mm, "end": v(-4.23, 1.86) * mm});
            skLineSegment(sketch, "E1835", {"start": v(-4.23, 1.86) * mm, "end": v(-3.73, 2.37) * mm});
            skLineSegment(sketch, "E1836", {"start": v(-3.73, 2.37) * mm, "end": v(-2.86, 2.83) * mm});
            skLineSegment(sketch, "E1837", {"start": v(-2.86, 2.83) * mm, "end": v(-2.2, 3.05) * mm});
            skLineSegment(sketch, "E1838", {"start": v(-2.03, 1.02) * mm, "end": v(-2.03, 1.19) * mm});
            skLineSegment(sketch, "E1839", {"start": v(-1.86, 1.02) * mm, "end": v(-2.03, 1.02) * mm});
            skLineSegment(sketch, "E1840", {"start": v(-1.86, 1.02) * mm, "end": v(-1.7, 1.19) * mm});
            skLineSegment(sketch, "E1841", {"start": v(-1.52, 1.02) * mm, "end": v(-1.7, 1.19) * mm});
            skLineSegment(sketch, "E1842", {"start": v(-1.52, 1.02) * mm, "end": v(-1.35, 1.19) * mm});
            skLineSegment(sketch, "E1843", {"start": v(-1.19, 1.19) * mm, "end": v(-1.02, 1.02) * mm});
            skLineSegment(sketch, "E1844", {"start": v(-1.02, 1.02) * mm, "end": v(-0.85, 1.19) * mm});
            skLineSegment(sketch, "E1845", {"start": v(-0.68, 1.02) * mm, "end": v(-0.85, 1.19) * mm});
            skLineSegment(sketch, "E1846", {"start": v(-0.5, 1.02) * mm, "end": v(-0.68, 1.02) * mm});
            skLineSegment(sketch, "E1847", {"start": v(-0.5, 1.02) * mm, "end": v(-0.34, 1.19) * mm});
            skLineSegment(sketch, "E1848", {"start": v(-0.34, 1.19) * mm, "end": v(-0.5, 1.35) * mm});
            skLineSegment(sketch, "E1849", {"start": v(0.5, 1.02) * mm, "end": v(0.68, 1.35) * mm});
            skLineSegment(sketch, "E1850", {"start": v(1.35, 1.02) * mm, "end": v(1.19, 1.19) * mm});
            skLineSegment(sketch, "E1851", {"start": v(1.19, 1.19) * mm, "end": v(1.19, 1.52) * mm});
            skLineSegment(sketch, "E1852", {"start": v(1.52, 1.02) * mm, "end": v(1.35, 1.02) * mm});
            skLineSegment(sketch, "E1853", {"start": v(1.52, 1.02) * mm, "end": v(1.7, 1.19) * mm});
            skLineSegment(sketch, "E1854", {"start": v(10.84, 1.02) * mm, "end": v(10.84, 1.19) * mm});
            skLineSegment(sketch, "E1855", {"start": v(11, 1.02) * mm, "end": v(10.84, 1.02) * mm});
            skLineSegment(sketch, "E1856", {"start": v(11.35, 1.02) * mm, "end": v(11, 1.02) * mm});
            skLineSegment(sketch, "E1857", {"start": v(11.35, 1.02) * mm, "end": v(11.68, 1.35) * mm});
            skLineSegment(sketch, "E1858", {"start": v(12.02, 1.02) * mm, "end": v(12.02, 1.19) * mm});
            skLineSegment(sketch, "E1859", {"start": v(22.86, 1.02) * mm, "end": v(22.86, 1.19) * mm});
            skLineSegment(sketch, "E1860", {"start": v(23.7, 1.02) * mm, "end": v(23.7, 1.19) * mm});
            skLineSegment(sketch, "E1861", {"start": v(-10, 0.85) * mm, "end": v(-10.16, 1.02) * mm});
            skLineSegment(sketch, "E1862", {"start": v(-9.82, 0.85) * mm, "end": v(-10, 0.85) * mm});
            skLineSegment(sketch, "E1863", {"start": v(-9.82, 0.85) * mm, "end": v(-9.82, 1.02) * mm});
            skLineSegment(sketch, "E1864", {"start": v(-9.65, 0.85) * mm, "end": v(-9.82, 0.85) * mm});
            skLineSegment(sketch, "E1865", {"start": v(-6.94, 0.85) * mm, "end": v(-7.11, 1.02) * mm});
            skLineSegment(sketch, "E1866", {"start": v(-6.94, 0.85) * mm, "end": v(-6.77, 1.02) * mm});
            skLineSegment(sketch, "E1867", {"start": v(-6.6, 0.85) * mm, "end": v(-6.77, 1.02) * mm});
            skLineSegment(sketch, "E1868", {"start": v(-5.93, 0.85) * mm, "end": v(-5.93, 1.02) * mm});
            skLineSegment(sketch, "E1869", {"start": v(-5.76, 0.85) * mm, "end": v(-5.93, 0.85) * mm});
            skLineSegment(sketch, "E1870", {"start": v(-4.74, 0.85) * mm, "end": v(-4.91, 0.85) * mm});
            skLineSegment(sketch, "E1871", {"start": v(-4.74, 0.85) * mm, "end": v(-4.74, 1.02) * mm});
            skLineSegment(sketch, "E1872", {"start": v(-2.03, 0.85) * mm, "end": v(-2.03, 1.02) * mm});
            skLineSegment(sketch, "E1873", {"start": v(-1.7, 0.85) * mm, "end": v(-1.86, 1.02) * mm});
            skLineSegment(sketch, "E1874", {"start": v(-1.7, 0.85) * mm, "end": v(-1.52, 1.02) * mm});
            skLineSegment(sketch, "E1875", {"start": v(-0.5, 0.85) * mm, "end": v(-0.5, 1.02) * mm});
            skLineSegment(sketch, "E1876", {"start": v(1.52, 0.85) * mm, "end": v(1.52, 1.02) * mm});
            skLineSegment(sketch, "E1877", {"start": v(10.84, 0.85) * mm, "end": v(10.84, 1.02) * mm});
            skLineSegment(sketch, "E1878", {"start": v(11.51, 0.85) * mm, "end": v(11.35, 1.02) * mm});
            skLineSegment(sketch, "E1879", {"start": v(11.85, 0.85) * mm, "end": v(11.51, 0.85) * mm});
            skLineSegment(sketch, "E1880", {"start": v(12.02, 0.85) * mm, "end": v(11.85, 0.85) * mm});
            skLineSegment(sketch, "E1881", {"start": v(12.02, 0.85) * mm, "end": v(12.02, 1.02) * mm});
            skLineSegment(sketch, "E1882", {"start": v(22.86, 0.85) * mm, "end": v(22.86, 1.02) * mm});
            skLineSegment(sketch, "E1883", {"start": v(23.03, 0.85) * mm, "end": v(22.86, 0.85) * mm});
            skLineSegment(sketch, "E1884", {"start": v(23.54, 0.85) * mm, "end": v(23.03, 0.85) * mm});
            skLineSegment(sketch, "E1885", {"start": v(23.7, 0.85) * mm, "end": v(23.54, 0.85) * mm});
            skLineSegment(sketch, "E1886", {"start": v(23.7, 0.85) * mm, "end": v(23.7, 1.02) * mm});
            skLineSegment(sketch, "E1887", {"start": v(-6.77, 0.68) * mm, "end": v(-6.94, 0.85) * mm});
            skLineSegment(sketch, "E1888", {"start": v(-6.77, 0.68) * mm, "end": v(-6.6, 0.85) * mm});
            skLineSegment(sketch, "E1889", {"start": v(-5.93, 0.68) * mm, "end": v(-5.93, 0.85) * mm});
            skLineSegment(sketch, "E1890", {"start": v(-5.76, 0.85) * mm, "end": v(-5.08, 0.68) * mm});
            skLineSegment(sketch, "E1891", {"start": v(-5.08, 0.68) * mm, "end": v(-4.91, 0.85) * mm});
            skLineSegment(sketch, "E1892", {"start": v(-2.2, 0.68) * mm, "end": v(-2.88, 1.02) * mm});
            skLineSegment(sketch, "E1893", {"start": v(-2.88, 1.02) * mm, "end": v(-3.4, 0.92) * mm});
            skLineSegment(sketch, "E1894", {"start": v(-3.4, 0.92) * mm, "end": v(-4.4, 0.78) * mm});
            skLineSegment(sketch, "E1895", {"start": v(-4.4, 0.78) * mm, "end": v(-4.74, 0.85) * mm});
            skLineSegment(sketch, "E1896", {"start": v(-2.2, 0.68) * mm, "end": v(-2.03, 0.85) * mm});
            skLineSegment(sketch, "E1897", {"start": v(-1.86, 0.68) * mm, "end": v(-2.03, 0.85) * mm});
            skLineSegment(sketch, "E1898", {"start": v(-1.86, 0.68) * mm, "end": v(-1.7, 0.85) * mm});
            skLineSegment(sketch, "E1899", {"start": v(0.34, 0.68) * mm, "end": v(0.5, 1.02) * mm});
            skLineSegment(sketch, "E1900", {"start": v(0.85, 0.68) * mm, "end": v(0.5, 1.02) * mm});
            skLineSegment(sketch, "E1901", {"start": v(1.02, 0.68) * mm, "end": v(0.85, 0.68) * mm});
            skLineSegment(sketch, "E1902", {"start": v(1.02, 0.68) * mm, "end": v(1.35, 1.02) * mm});
            skLineSegment(sketch, "E1903", {"start": v(12.02, 0.68) * mm, "end": v(12.02, 0.85) * mm});
            skLineSegment(sketch, "E1904", {"start": v(22.86, 0.68) * mm, "end": v(22.86, 0.85) * mm});
            skLineSegment(sketch, "E1905", {"start": v(23.7, 0.68) * mm, "end": v(23.7, 0.85) * mm});
            skLineSegment(sketch, "E1906", {"start": v(-10.33, 0.5) * mm, "end": v(-10.33, 0.85) * mm});
            skLineSegment(sketch, "E1907", {"start": v(-10.33, 0.85) * mm, "end": v(-10.16, 1.02) * mm});
            skLineSegment(sketch, "E1908", {"start": v(-6.1, 0.5) * mm, "end": v(-6.43, 0.85) * mm});
            skLineSegment(sketch, "E1909", {"start": v(-6.43, 0.85) * mm, "end": v(-6.6, 0.85) * mm});
            skLineSegment(sketch, "E1910", {"start": v(-6.1, 0.5) * mm, "end": v(-5.93, 0.68) * mm});
            skLineSegment(sketch, "E1911", {"start": v(-1.86, 0.5) * mm, "end": v(-1.86, 0.68) * mm});
            skLineSegment(sketch, "E1912", {"start": v(-0.68, 0.5) * mm, "end": v(-0.5, 0.85) * mm});
            skLineSegment(sketch, "E1913", {"start": v(0.85, 0.5) * mm, "end": v(0.85, 0.68) * mm});
            skLineSegment(sketch, "E1914", {"start": v(1.02, 0.5) * mm, "end": v(0.85, 0.5) * mm});
            skLineSegment(sketch, "E1915", {"start": v(1.02, 0.5) * mm, "end": v(1.02, 0.68) * mm});
            skLineSegment(sketch, "E1916", {"start": v(1.7, 0.5) * mm, "end": v(1.52, 0.85) * mm});
            skLineSegment(sketch, "E1917", {"start": v(1.7, 0.5) * mm, "end": v(2.03, 0.85) * mm});
            skLineSegment(sketch, "E1918", {"start": v(2.03, 0.85) * mm, "end": v(1.86, 1.19) * mm});
            skLineSegment(sketch, "E1919", {"start": v(6.27, 0.5) * mm, "end": v(6.1, 0.5) * mm});
            skLineSegment(sketch, "E1920", {"start": v(6.27, 0.5) * mm, "end": v(7.07, 1.39) * mm});
            skLineSegment(sketch, "E1921", {"start": v(7.07, 1.39) * mm, "end": v(7.38, 1.9) * mm});
            skLineSegment(sketch, "E1922", {"start": v(7.38, 1.9) * mm, "end": v(7.5, 2.18) * mm});
            skLineSegment(sketch, "E1923", {"start": v(7.5, 2.18) * mm, "end": v(7.62, 2.37) * mm});
            skLineSegment(sketch, "E1924", {"start": v(7.62, 2.37) * mm, "end": v(7.62, 3.56) * mm});
            skLineSegment(sketch, "E1925", {"start": v(7.62, 3.56) * mm, "end": v(7.41, 3.87) * mm});
            skLineSegment(sketch, "E1926", {"start": v(7.41, 3.87) * mm, "end": v(7.11, 4.23) * mm});
            skLineSegment(sketch, "E1927", {"start": v(11, 0.5) * mm, "end": v(10.84, 0.85) * mm});
            skLineSegment(sketch, "E1928", {"start": v(11, 0.5) * mm, "end": v(11.18, 0.5) * mm});
            skLineSegment(sketch, "E1929", {"start": v(11.18, 0.5) * mm, "end": v(11.51, 0.85) * mm});
            skLineSegment(sketch, "E1930", {"start": v(12.2, 0.5) * mm, "end": v(12.02, 0.68) * mm});
            skLineSegment(sketch, "E1931", {"start": v(22.86, 0.5) * mm, "end": v(22.86, 0.68) * mm});
            skLineSegment(sketch, "E1932", {"start": v(23.03, 0.5) * mm, "end": v(22.86, 0.5) * mm});
            skLineSegment(sketch, "E1933", {"start": v(23.54, 0.5) * mm, "end": v(23.03, 0.5) * mm});
            skLineSegment(sketch, "E1934", {"start": v(23.7, 0.5) * mm, "end": v(23.54, 0.5) * mm});
            skLineSegment(sketch, "E1935", {"start": v(23.7, 0.5) * mm, "end": v(23.7, 0.68) * mm});
            skLineSegment(sketch, "E1936", {"start": v(-21, 0.34) * mm, "end": v(-21, 0.5) * mm});
            skLineSegment(sketch, "E1937", {"start": v(-21, 0.5) * mm, "end": v(-20.83, 0.5) * mm});
            skLineSegment(sketch, "E1938", {"start": v(-10.5, 0.34) * mm, "end": v(-10.84, 0.5) * mm});
            skLineSegment(sketch, "E1939", {"start": v(-10.84, 0.5) * mm, "end": v(-11.2, 0.39) * mm});
            skLineSegment(sketch, "E1940", {"start": v(-11.2, 0.39) * mm, "end": v(-11.51, 0.34) * mm});
            skLineSegment(sketch, "E1941", {"start": v(-10.33, 0.34) * mm, "end": v(-10.5, 0.34) * mm});
            skLineSegment(sketch, "E1942", {"start": v(-10.33, 0.34) * mm, "end": v(-10.33, 0.5) * mm});
            skLineSegment(sketch, "E1943", {"start": v(-6.43, 0.34) * mm, "end": v(-6.77, 0.68) * mm});
            skLineSegment(sketch, "E1944", {"start": v(-6.27, 0.34) * mm, "end": v(-6.43, 0.34) * mm});
            skLineSegment(sketch, "E1945", {"start": v(-6.27, 0.34) * mm, "end": v(-6.1, 0.5) * mm});
            skLineSegment(sketch, "E1946", {"start": v(-2.03, 0.34) * mm, "end": v(-2.2, 0.68) * mm});
            skLineSegment(sketch, "E1947", {"start": v(-2.03, 0.34) * mm, "end": v(-1.86, 0.5) * mm});
            skLineSegment(sketch, "E1948", {"start": v(-1.7, 0.34) * mm, "end": v(-1.86, 0.5) * mm});
            skLineSegment(sketch, "E1949", {"start": v(-0.85, 0.34) * mm, "end": v(-1.02, 0.5) * mm});
            skLineSegment(sketch, "E1950", {"start": v(-1.02, 0.5) * mm, "end": v(-1.52, 0.5) * mm});
            skLineSegment(sketch, "E1951", {"start": v(-1.52, 0.5) * mm, "end": v(-1.7, 0.34) * mm});
            skLineSegment(sketch, "E1952", {"start": v(-0.68, 0.34) * mm, "end": v(-0.85, 0.34) * mm});
            skLineSegment(sketch, "E1953", {"start": v(-0.68, 0.34) * mm, "end": v(-0.68, 0.5) * mm});
            skLineSegment(sketch, "E1954", {"start": v(0.68, 0.34) * mm, "end": v(0.34, 0.68) * mm});
            skLineSegment(sketch, "E1955", {"start": v(0.68, 0.34) * mm, "end": v(0.85, 0.5) * mm});
            skLineSegment(sketch, "E1956", {"start": v(1.7, 0.34) * mm, "end": v(1.7, 0.5) * mm});
            skLineSegment(sketch, "E1957", {"start": v(5.93, 0.34) * mm, "end": v(6.1, 0.5) * mm});
            skLineSegment(sketch, "E1958", {"start": v(6.27, 0.34) * mm, "end": v(6.27, 0.5) * mm});
            skLineSegment(sketch, "E1959", {"start": v(22.86, 0.34) * mm, "end": v(22.86, 0.5) * mm});
            skLineSegment(sketch, "E1960", {"start": v(-6.27, 0.17) * mm, "end": v(-6.27, 0.34) * mm});
            skLineSegment(sketch, "E1961", {"start": v(-1.86, 0.17) * mm, "end": v(-2.03, 0.34) * mm});
            skLineSegment(sketch, "E1962", {"start": v(-1.86, 0.17) * mm, "end": v(-1.7, 0.34) * mm});
            skLineSegment(sketch, "E1963", {"start": v(-1.52, 0.17) * mm, "end": v(-1.7, 0.34) * mm});
            skLineSegment(sketch, "E1964", {"start": v(-0.68, 0.17) * mm, "end": v(-0.68, 0.34) * mm});
            skLineSegment(sketch, "E1965", {"start": v(0.68, 0.17) * mm, "end": v(0.68, 0.34) * mm});
            skLineSegment(sketch, "E1966", {"start": v(1.35, 0.17) * mm, "end": v(1.02, 0.5) * mm});
            skLineSegment(sketch, "E1967", {"start": v(1.52, 0.17) * mm, "end": v(1.35, 0.17) * mm});
            skLineSegment(sketch, "E1968", {"start": v(1.7, 0.17) * mm, "end": v(1.52, 0.17) * mm});
            skLineSegment(sketch, "E1969", {"start": v(1.7, 0.17) * mm, "end": v(1.7, 0.34) * mm});
            skLineSegment(sketch, "E1970", {"start": v(5.42, 0.17) * mm, "end": v(4.4, 1.52) * mm});
            skLineSegment(sketch, "E1971", {"start": v(4.4, 1.52) * mm, "end": v(2.33, 3.34) * mm});
            skLineSegment(sketch, "E1972", {"start": v(2.33, 3.34) * mm, "end": v(2.2, 3.39) * mm});
            skLineSegment(sketch, "E1973", {"start": v(2.2, 3.39) * mm, "end": v(1.56, 4.26) * mm});
            skLineSegment(sketch, "E1974", {"start": v(1.56, 4.26) * mm, "end": v(1.52, 4.4) * mm});
            skLineSegment(sketch, "E1975", {"start": v(5.42, 0.17) * mm, "end": v(5.59, 0.34) * mm});
            skLineSegment(sketch, "E1976", {"start": v(5.59, 0.34) * mm, "end": v(5.93, 0.34) * mm});
            skLineSegment(sketch, "E1977", {"start": v(6.1, 0.17) * mm, "end": v(5.93, 0.34) * mm});
            skLineSegment(sketch, "E1978", {"start": v(6.1, 0.17) * mm, "end": v(6.27, 0.34) * mm});
            skLineSegment(sketch, "E1979", {"start": v(-6.27, 0) * mm, "end": v(-6.43, 0) * mm});
            skLineSegment(sketch, "E1980", {"start": v(-6.27, 0) * mm, "end": v(-6.27, 0.17) * mm});
            skLineSegment(sketch, "E1981", {"start": v(-6.1, 0) * mm, "end": v(-6.27, 0) * mm});
            skLineSegment(sketch, "E1982", {"start": v(-2.03, 0) * mm, "end": v(-6.1, 0) * mm});
            skLineSegment(sketch, "E1983", {"start": v(-1.86, 0) * mm, "end": v(-2.03, 0) * mm});
            skLineSegment(sketch, "E1984", {"start": v(-1.86, 0) * mm, "end": v(-1.86, 0.17) * mm});
            skLineSegment(sketch, "E1985", {"start": v(-1.7, 0) * mm, "end": v(-1.86, 0) * mm});
            skLineSegment(sketch, "E1986", {"start": v(-1.7, 0) * mm, "end": v(-1.52, 0.17) * mm});
            skLineSegment(sketch, "E1987", {"start": v(-1.35, 0) * mm, "end": v(-1.52, 0.17) * mm});
            skLineSegment(sketch, "E1988", {"start": v(-0.85, 0) * mm, "end": v(-0.68, 0.17) * mm});
            skLineSegment(sketch, "E1989", {"start": v(0.5, 0) * mm, "end": v(0.17, 0.34) * mm});
            skLineSegment(sketch, "E1990", {"start": v(0.17, 0.34) * mm, "end": v(0.34, 0.68) * mm});
            skLineSegment(sketch, "E1991", {"start": v(0.68, 0) * mm, "end": v(0.5, 0) * mm});
            skLineSegment(sketch, "E1992", {"start": v(0.68, 0) * mm, "end": v(0.68, 0.17) * mm});
            skLineSegment(sketch, "E1993", {"start": v(1.35, 0) * mm, "end": v(1.35, 0.17) * mm});
            skLineSegment(sketch, "E1994", {"start": v(1.7, 0) * mm, "end": v(1.7, 0.17) * mm});
            skLineSegment(sketch, "E1995", {"start": v(23.88, 0) * mm, "end": v(23.88, 0.34) * mm});
            skLineSegment(sketch, "E1996", {"start": v(23.88, 0.34) * mm, "end": v(23.7, 0.5) * mm});
            skLineSegment(sketch, "E1997", {"start": v(-1.52, -0.17) * mm, "end": v(-1.7, 0) * mm});
            skLineSegment(sketch, "E1998", {"start": v(-1.52, -0.17) * mm, "end": v(-1.35, 0) * mm});
            skLineSegment(sketch, "E1999", {"start": v(-1.02, -0.17) * mm, "end": v(-1.35, 0) * mm});
            skLineSegment(sketch, "E2000", {"start": v(-1.02, -0.17) * mm, "end": v(-0.85, 0) * mm});
            skLineSegment(sketch, "E2001", {"start": v(-0.68, -0.17) * mm, "end": v(-0.85, 0) * mm});
            skLineSegment(sketch, "E2002", {"start": v(0.85, -0.17) * mm, "end": v(0.68, 0) * mm});
            skLineSegment(sketch, "E2003", {"start": v(13.04, -0.17) * mm, "end": v(13.04, 0) * mm});
            skLineSegment(sketch, "E2004", {"start": v(13.04, 0) * mm, "end": v(12.53, 0.5) * mm});
            skLineSegment(sketch, "E2005", {"start": v(12.53, 0.5) * mm, "end": v(12.2, 0.5) * mm});
            skLineSegment(sketch, "E2006", {"start": v(-23.2, -0.34) * mm, "end": v(-23.03, 2.88) * mm});
            skLineSegment(sketch, "E2007", {"start": v(-21.67, -0.34) * mm, "end": v(-21.84, 4.91) * mm});
            skLineSegment(sketch, "E2008", {"start": v(-1.52, -0.34) * mm, "end": v(-1.52, -0.17) * mm});
            skLineSegment(sketch, "E2009", {"start": v(-1.19, -0.34) * mm, "end": v(-1.02, -0.17) * mm});
            skLineSegment(sketch, "E2010", {"start": v(-0.85, -0.34) * mm, "end": v(-1.02, -0.17) * mm});
            skLineSegment(sketch, "E2011", {"start": v(-0.85, -0.34) * mm, "end": v(-0.68, -0.17) * mm});
            skLineSegment(sketch, "E2012", {"start": v(0.85, -0.34) * mm, "end": v(0.68, -0.34) * mm});
            skLineSegment(sketch, "E2013", {"start": v(0.85, -0.34) * mm, "end": v(0.85, -0.17) * mm});
            skLineSegment(sketch, "E2014", {"start": v(1.02, -0.34) * mm, "end": v(0.85, -0.34) * mm});
            skLineSegment(sketch, "E2015", {"start": v(1.02, -0.34) * mm, "end": v(1.35, 0) * mm});
            skLineSegment(sketch, "E2016", {"start": v(5.59, -0.34) * mm, "end": v(5.42, -0.17) * mm});
            skLineSegment(sketch, "E2017", {"start": v(5.42, -0.17) * mm, "end": v(5.42, 0.17) * mm});
            skLineSegment(sketch, "E2018", {"start": v(5.59, -0.34) * mm, "end": v(6.1, 0.17) * mm});
            skLineSegment(sketch, "E2019", {"start": v(13.04, -0.34) * mm, "end": v(13.04, -0.17) * mm});
            skLineSegment(sketch, "E2020", {"start": v(13.2, -0.34) * mm, "end": v(13.04, -0.34) * mm});
            skLineSegment(sketch, "E2021", {"start": v(13.2, -0.34) * mm, "end": v(14.9, 1.52) * mm});
            skLineSegment(sketch, "E2022", {"start": v(14.9, 1.52) * mm, "end": v(15.22, 1.73) * mm});
            skLineSegment(sketch, "E2023", {"start": v(15.22, 1.73) * mm, "end": v(15.4, 1.86) * mm});
            skLineSegment(sketch, "E2024", {"start": v(-23.2, -0.5) * mm, "end": v(-23.2, -0.34) * mm});
            skLineSegment(sketch, "E2025", {"start": v(-23.03, -0.5) * mm, "end": v(-23.2, -0.5) * mm});
            skLineSegment(sketch, "E2026", {"start": v(-21.84, -0.5) * mm, "end": v(-23.03, -0.5) * mm});
            skLineSegment(sketch, "E2027", {"start": v(-21.67, -0.5) * mm, "end": v(-21.84, -0.5) * mm});
            skLineSegment(sketch, "E2028", {"start": v(-21.67, -0.5) * mm, "end": v(-21.67, -0.34) * mm});
            skLineSegment(sketch, "E2029", {"start": v(-21.5, -0.5) * mm, "end": v(-21.67, -0.5) * mm});
            skLineSegment(sketch, "E2030", {"start": v(-21.5, -0.5) * mm, "end": v(-21.03, 0.19) * mm});
            skLineSegment(sketch, "E2031", {"start": v(-21.03, 0.19) * mm, "end": v(-21, 0.34) * mm});
            skLineSegment(sketch, "E2032", {"start": v(-1.52, -0.5) * mm, "end": v(-1.52, -0.34) * mm});
            skLineSegment(sketch, "E2033", {"start": v(-1.35, -0.5) * mm, "end": v(-1.52, -0.5) * mm});
            skLineSegment(sketch, "E2034", {"start": v(-1.19, -0.5) * mm, "end": v(-1.35, -0.5) * mm});
            skLineSegment(sketch, "E2035", {"start": v(-1.19, -0.5) * mm, "end": v(-1.19, -0.34) * mm});
            skLineSegment(sketch, "E2036", {"start": v(-0.85, -0.5) * mm, "end": v(-0.85, -0.34) * mm});
            skLineSegment(sketch, "E2037", {"start": v(0.17, -0.5) * mm, "end": v(0.17, -0.34) * mm});
            skLineSegment(sketch, "E2038", {"start": v(0.17, -0.34) * mm, "end": v(0.5, 0) * mm});
            skLineSegment(sketch, "E2039", {"start": v(0.5, -0.5) * mm, "end": v(0.68, -0.34) * mm});
            skLineSegment(sketch, "E2040", {"start": v(0.85, -0.5) * mm, "end": v(0.85, -0.34) * mm});
            skLineSegment(sketch, "E2041", {"start": v(1.19, -0.5) * mm, "end": v(1.02, -0.34) * mm});
            skLineSegment(sketch, "E2042", {"start": v(1.35, -0.5) * mm, "end": v(1.19, -0.5) * mm});
            skLineSegment(sketch, "E2043", {"start": v(1.86, -0.5) * mm, "end": v(2.03, -0.34) * mm});
            skLineSegment(sketch, "E2044", {"start": v(2.03, -0.34) * mm, "end": v(1.7, 0) * mm});
            skLineSegment(sketch, "E2045", {"start": v(13.2, -0.5) * mm, "end": v(13.2, -0.34) * mm});
            skLineSegment(sketch, "E2046", {"start": v(-23.2, -0.68) * mm, "end": v(-23.2, -0.5) * mm});
            skLineSegment(sketch, "E2047", {"start": v(-21.67, -0.68) * mm, "end": v(-21.67, -0.5) * mm});
            skLineSegment(sketch, "E2048", {"start": v(-1.52, -0.68) * mm, "end": v(-1.52, -0.5) * mm});
            skLineSegment(sketch, "E2049", {"start": v(-1.02, -0.68) * mm, "end": v(-1.19, -0.5) * mm});
            skLineSegment(sketch, "E2050", {"start": v(-0.85, -0.68) * mm, "end": v(-1.02, -0.68) * mm});
            skLineSegment(sketch, "E2051", {"start": v(-0.85, -0.68) * mm, "end": v(-0.85, -0.5) * mm});
            skLineSegment(sketch, "E2052", {"start": v(0.17, -0.68) * mm, "end": v(0.17, -0.5) * mm});
            skLineSegment(sketch, "E2053", {"start": v(0.34, -0.68) * mm, "end": v(0.17, -0.68) * mm});
            skLineSegment(sketch, "E2054", {"start": v(0.34, -0.68) * mm, "end": v(0.5, -0.5) * mm});
            skLineSegment(sketch, "E2055", {"start": v(0.68, -0.68) * mm, "end": v(0.5, -0.5) * mm});
            skLineSegment(sketch, "E2056", {"start": v(0.68, -0.68) * mm, "end": v(0.85, -0.5) * mm});
            skLineSegment(sketch, "E2057", {"start": v(1.19, -0.68) * mm, "end": v(1.19, -0.5) * mm});
            skLineSegment(sketch, "E2058", {"start": v(1.52, -0.68) * mm, "end": v(1.35, -0.5) * mm});
            skLineSegment(sketch, "E2059", {"start": v(1.7, -0.68) * mm, "end": v(1.52, -0.68) * mm});
            skLineSegment(sketch, "E2060", {"start": v(1.86, -0.68) * mm, "end": v(1.7, -0.68) * mm});
            skLineSegment(sketch, "E2061", {"start": v(1.86, -0.68) * mm, "end": v(1.86, -0.5) * mm});
            skLineSegment(sketch, "E2062", {"start": v(-23.2, -0.85) * mm, "end": v(-23.2, -0.68) * mm});
            skLineSegment(sketch, "E2063", {"start": v(-23.03, -0.85) * mm, "end": v(-23.2, -0.85) * mm});
            skLineSegment(sketch, "E2064", {"start": v(-21.84, -0.85) * mm, "end": v(-23.03, -0.85) * mm});
            skLineSegment(sketch, "E2065", {"start": v(-21.67, -0.85) * mm, "end": v(-21.84, -0.85) * mm});
            skLineSegment(sketch, "E2066", {"start": v(-21.67, -0.85) * mm, "end": v(-21.67, -0.68) * mm});
            skLineSegment(sketch, "E2067", {"start": v(-0.68, -0.85) * mm, "end": v(-0.85, -0.68) * mm});
            skLineSegment(sketch, "E2068", {"start": v(-0.68, -0.85) * mm, "end": v(-0.47, -0.52) * mm});
            skLineSegment(sketch, "E2069", {"start": v(-0.47, -0.52) * mm, "end": v(-0.34, -0.34) * mm});
            skLineSegment(sketch, "E2070", {"start": v(-0.34, -0.34) * mm, "end": v(-0.68, -0.17) * mm});
            skLineSegment(sketch, "E2071", {"start": v(0.17, -0.85) * mm, "end": v(0.17, -0.68) * mm});
            skLineSegment(sketch, "E2072", {"start": v(0.5, -0.85) * mm, "end": v(0.34, -0.68) * mm});
            skLineSegment(sketch, "E2073", {"start": v(0.5, -0.85) * mm, "end": v(0.68, -0.68) * mm});
            skLineSegment(sketch, "E2074", {"start": v(0.85, -0.85) * mm, "end": v(0.68, -0.68) * mm});
            skLineSegment(sketch, "E2075", {"start": v(1.35, -0.85) * mm, "end": v(1.19, -0.68) * mm});
            skLineSegment(sketch, "E2076", {"start": v(1.35, -0.85) * mm, "end": v(1.52, -0.68) * mm});
            skLineSegment(sketch, "E2077", {"start": v(-23.7, -1.02) * mm, "end": v(-23.46, 3.04) * mm});
            skLineSegment(sketch, "E2078", {"start": v(-23.46, 3.04) * mm, "end": v(-23.37, 3.22) * mm});
            skLineSegment(sketch, "E2079", {"start": v(-23.2, -1.02) * mm, "end": v(-23.2, -0.85) * mm});
            skLineSegment(sketch, "E2080", {"start": v(-21.67, -1.02) * mm, "end": v(-21.67, -0.85) * mm});
            skLineSegment(sketch, "E2081", {"start": v(0.17, -1.02) * mm, "end": v(0.17, -0.85) * mm});
            skLineSegment(sketch, "E2082", {"start": v(0.34, -1.02) * mm, "end": v(0.17, -1.02) * mm});
            skLineSegment(sketch, "E2083", {"start": v(0.34, -1.02) * mm, "end": v(0.5, -0.85) * mm});
            skLineSegment(sketch, "E2084", {"start": v(0.68, -1.02) * mm, "end": v(0.5, -0.85) * mm});
            skLineSegment(sketch, "E2085", {"start": v(0.68, -1.02) * mm, "end": v(0.85, -0.85) * mm});
            skLineSegment(sketch, "E2086", {"start": v(1.02, -1.02) * mm, "end": v(0.85, -0.85) * mm});
            skLineSegment(sketch, "E2087", {"start": v(1.19, -1.02) * mm, "end": v(1.02, -1.02) * mm});
            skLineSegment(sketch, "E2088", {"start": v(1.19, -1.02) * mm, "end": v(1.35, -0.85) * mm});
            skLineSegment(sketch, "E2089", {"start": v(1.52, -1.02) * mm, "end": v(1.35, -0.85) * mm});
            skLineSegment(sketch, "E2090", {"start": v(24.05, -1.02) * mm, "end": v(24.05, -0.17) * mm});
            skLineSegment(sketch, "E2091", {"start": v(24.05, -0.17) * mm, "end": v(23.88, 0) * mm});
            skLineSegment(sketch, "E2092", {"start": v(-23.7, -1.19) * mm, "end": v(-23.88, -1.19) * mm});
            skLineSegment(sketch, "E2093", {"start": v(-23.7, -1.19) * mm, "end": v(-23.7, -1.02) * mm});
            skLineSegment(sketch, "E2094", {"start": v(-23.2, -1.19) * mm, "end": v(-23.37, -1.19) * mm});
            skLineSegment(sketch, "E2095", {"start": v(-23.2, -1.19) * mm, "end": v(-23.2, -1.02) * mm});
            skLineSegment(sketch, "E2096", {"start": v(-11, -1.19) * mm, "end": v(-11.68, -0.68) * mm});
            skLineSegment(sketch, "E2097", {"start": v(0.17, -1.19) * mm, "end": v(0.17, -1.02) * mm});
            skLineSegment(sketch, "E2098", {"start": v(0.5, -1.19) * mm, "end": v(0.34, -1.02) * mm});
            skLineSegment(sketch, "E2099", {"start": v(0.5, -1.19) * mm, "end": v(0.68, -1.02) * mm});
            skLineSegment(sketch, "E2100", {"start": v(0.85, -1.19) * mm, "end": v(0.68, -1.02) * mm});
            skLineSegment(sketch, "E2101", {"start": v(0.85, -1.19) * mm, "end": v(1.02, -1.02) * mm});
            skLineSegment(sketch, "E2102", {"start": v(1.35, -1.19) * mm, "end": v(1.19, -1.02) * mm});
            skLineSegment(sketch, "E2103", {"start": v(1.52, -1.19) * mm, "end": v(1.35, -1.19) * mm});
            skLineSegment(sketch, "E2104", {"start": v(1.52, -1.19) * mm, "end": v(1.52, -1.02) * mm});
            skLineSegment(sketch, "E2105", {"start": v(23.88, -1.19) * mm, "end": v(23.7, -1.02) * mm});
            skLineSegment(sketch, "E2106", {"start": v(23.7, -1.02) * mm, "end": v(23.7, -0.17) * mm});
            skLineSegment(sketch, "E2107", {"start": v(23.7, -0.17) * mm, "end": v(23.88, 0) * mm});
            skLineSegment(sketch, "E2108", {"start": v(24.05, -1.19) * mm, "end": v(23.88, -1.19) * mm});
            skLineSegment(sketch, "E2109", {"start": v(24.05, -1.19) * mm, "end": v(24.05, -1.02) * mm});
            skLineSegment(sketch, "E2110", {"start": v(-25.57, -1.35) * mm, "end": v(-25.15, 2.2) * mm});
            skLineSegment(sketch, "E2111", {"start": v(-25.15, 2.2) * mm, "end": v(-24.5, 5.4) * mm});
            skLineSegment(sketch, "E2112", {"start": v(-24.5, 5.4) * mm, "end": v(-24.1, 6.8) * mm});
            skLineSegment(sketch, "E2113", {"start": v(-24.1, 6.8) * mm, "end": v(-22.83, 10.31) * mm});
            skLineSegment(sketch, "E2114", {"start": v(-22.83, 10.31) * mm, "end": v(-21.84, 12.02) * mm});
            skLineSegment(sketch, "E2115", {"start": v(-21.84, 12.02) * mm, "end": v(-21.01, 12.56) * mm});
            skLineSegment(sketch, "E2116", {"start": v(-21.01, 12.56) * mm, "end": v(-20.16, 12.77) * mm});
            skLineSegment(sketch, "E2117", {"start": v(-20.16, 12.77) * mm, "end": v(-19.12, 12.56) * mm});
            skLineSegment(sketch, "E2118", {"start": v(-19.12, 12.56) * mm, "end": v(-18.97, 12.53) * mm});
            skLineSegment(sketch, "E2119", {"start": v(-23.7, -1.19) * mm, "end": v(-23.54, -1.35) * mm});
            skLineSegment(sketch, "E2120", {"start": v(-23.54, -1.35) * mm, "end": v(-23.37, -1.19) * mm});
            skLineSegment(sketch, "E2121", {"start": v(-23.2, -1.19) * mm, "end": v(-23.03, -1.35) * mm});
            skLineSegment(sketch, "E2122", {"start": v(-23.03, -1.35) * mm, "end": v(-21.67, -1.02) * mm});
            skLineSegment(sketch, "E2123", {"start": v(-18.29, -1.35) * mm, "end": v(-18.46, -0.5) * mm});
            skLineSegment(sketch, "E2124", {"start": v(-18.46, -0.5) * mm, "end": v(-19.3, 0.34) * mm});
            skLineSegment(sketch, "E2125", {"start": v(-19.3, 0.34) * mm, "end": v(-20.83, 0.5) * mm});
            skLineSegment(sketch, "E2126", {"start": v(-11, -1.35) * mm, "end": v(-11, -1.19) * mm});
            skLineSegment(sketch, "E2127", {"start": v(-10.84, -1.35) * mm, "end": v(-11, -1.35) * mm});
            skLineSegment(sketch, "E2128", {"start": v(-1.52, -1.35) * mm, "end": v(-1.7, -1.19) * mm});
            skLineSegment(sketch, "E2129", {"start": v(-1.7, -1.19) * mm, "end": v(-1.7, -0.85) * mm});
            skLineSegment(sketch, "E2130", {"start": v(-1.7, -0.85) * mm, "end": v(-1.52, -0.68) * mm});
            skLineSegment(sketch, "E2131", {"start": v(-1.19, -1.35) * mm, "end": v(-1.19, -0.85) * mm});
            skLineSegment(sketch, "E2132", {"start": v(-1.19, -0.85) * mm, "end": v(-1.02, -0.68) * mm});
            skLineSegment(sketch, "E2133", {"start": v(-0.85, -1.35) * mm, "end": v(-0.68, -1.19) * mm});
            skLineSegment(sketch, "E2134", {"start": v(-0.68, -1.19) * mm, "end": v(-0.68, -0.85) * mm});
            skLineSegment(sketch, "E2135", {"start": v(0.34, -1.35) * mm, "end": v(0.17, -1.19) * mm});
            skLineSegment(sketch, "E2136", {"start": v(0.34, -1.35) * mm, "end": v(0.5, -1.19) * mm});
            skLineSegment(sketch, "E2137", {"start": v(0.68, -1.35) * mm, "end": v(0.5, -1.19) * mm});
            skLineSegment(sketch, "E2138", {"start": v(0.68, -1.35) * mm, "end": v(0.85, -1.19) * mm});
            skLineSegment(sketch, "E2139", {"start": v(1.02, -1.35) * mm, "end": v(0.85, -1.19) * mm});
            skLineSegment(sketch, "E2140", {"start": v(1.19, -1.35) * mm, "end": v(1.02, -1.35) * mm});
            skLineSegment(sketch, "E2141", {"start": v(1.19, -1.35) * mm, "end": v(1.35, -1.19) * mm});
            skLineSegment(sketch, "E2142", {"start": v(1.52, -1.35) * mm, "end": v(1.52, -1.19) * mm});
            skLineSegment(sketch, "E2143", {"start": v(1.86, -1.35) * mm, "end": v(1.91, -1.03) * mm});
            skLineSegment(sketch, "E2144", {"start": v(1.91, -1.03) * mm, "end": v(1.86, -0.68) * mm});
            skLineSegment(sketch, "E2145", {"start": v(24.05, -1.35) * mm, "end": v(24.05, -1.19) * mm});
            skLineSegment(sketch, "E2146", {"start": v(-25.57, -1.52) * mm, "end": v(-25.57, -1.35) * mm});
            skLineSegment(sketch, "E2147", {"start": v(-25.4, -1.52) * mm, "end": v(-25.57, -1.52) * mm});
            skLineSegment(sketch, "E2148", {"start": v(-25.4, -1.52) * mm, "end": v(-23.88, -1.19) * mm});
            skLineSegment(sketch, "E2149", {"start": v(-21.67, -1.02) * mm, "end": v(-21.17, -1.52) * mm});
            skLineSegment(sketch, "E2150", {"start": v(-21.17, -1.52) * mm, "end": v(-18.46, -1.52) * mm});
            skLineSegment(sketch, "E2151", {"start": v(-18.46, -1.52) * mm, "end": v(-18.29, -1.35) * mm});
            skLineSegment(sketch, "E2152", {"start": v(-18.12, -1.52) * mm, "end": v(-18.29, -1.35) * mm});
            skLineSegment(sketch, "E2153", {"start": v(-18.12, -1.52) * mm, "end": v(-17.42, -1.05) * mm});
            skLineSegment(sketch, "E2154", {"start": v(-17.42, -1.05) * mm, "end": v(-14.4, 2.54) * mm});
            skLineSegment(sketch, "E2155", {"start": v(-14.4, 2.54) * mm, "end": v(-14.56, 6.1) * mm});
            skLineSegment(sketch, "E2156", {"start": v(-11, -1.52) * mm, "end": v(-11, -1.35) * mm});
            skLineSegment(sketch, "E2157", {"start": v(-1.52, -1.52) * mm, "end": v(-1.52, -1.35) * mm});
            skLineSegment(sketch, "E2158", {"start": v(-1.35, -1.52) * mm, "end": v(-1.52, -1.52) * mm});
            skLineSegment(sketch, "E2159", {"start": v(-1.35, -1.52) * mm, "end": v(-1.19, -1.35) * mm});
            skLineSegment(sketch, "E2160", {"start": v(-1.02, -1.52) * mm, "end": v(-1.19, -1.35) * mm});
            skLineSegment(sketch, "E2161", {"start": v(-0.85, -1.52) * mm, "end": v(-1.02, -1.52) * mm});
            skLineSegment(sketch, "E2162", {"start": v(-0.85, -1.52) * mm, "end": v(-0.85, -1.35) * mm});
            skLineSegment(sketch, "E2163", {"start": v(0.34, -1.52) * mm, "end": v(0.34, -1.35) * mm});
            skLineSegment(sketch, "E2164", {"start": v(0.5, -1.52) * mm, "end": v(0.34, -1.52) * mm});
            skLineSegment(sketch, "E2165", {"start": v(0.5, -1.52) * mm, "end": v(0.68, -1.35) * mm});
            skLineSegment(sketch, "E2166", {"start": v(0.85, -1.52) * mm, "end": v(0.68, -1.35) * mm});
            skLineSegment(sketch, "E2167", {"start": v(0.85, -1.52) * mm, "end": v(1.02, -1.35) * mm});
            skLineSegment(sketch, "E2168", {"start": v(1.35, -1.52) * mm, "end": v(1.19, -1.35) * mm});
            skLineSegment(sketch, "E2169", {"start": v(1.35, -1.52) * mm, "end": v(1.52, -1.35) * mm});
            skLineSegment(sketch, "E2170", {"start": v(1.7, -1.52) * mm, "end": v(1.52, -1.35) * mm});
            skLineSegment(sketch, "E2171", {"start": v(1.7, -1.52) * mm, "end": v(1.86, -1.35) * mm});
            skLineSegment(sketch, "E2172", {"start": v(-1.52, -1.7) * mm, "end": v(-1.52, -1.52) * mm});
            skLineSegment(sketch, "E2173", {"start": v(0.34, -1.7) * mm, "end": v(0.34, -1.52) * mm});
            skLineSegment(sketch, "E2174", {"start": v(0.68, -1.7) * mm, "end": v(0.5, -1.52) * mm});
            skLineSegment(sketch, "E2175", {"start": v(0.68, -1.7) * mm, "end": v(0.85, -1.52) * mm});
            skLineSegment(sketch, "E2176", {"start": v(1.02, -1.7) * mm, "end": v(0.85, -1.52) * mm});
            skLineSegment(sketch, "E2177", {"start": v(1.52, -1.7) * mm, "end": v(1.35, -1.52) * mm});
            skLineSegment(sketch, "E2178", {"start": v(1.52, -1.7) * mm, "end": v(1.7, -1.52) * mm});
            skLineSegment(sketch, "E2179", {"start": v(2.2, -1.7) * mm, "end": v(1.86, -1.35) * mm});
            skLineSegment(sketch, "E2180", {"start": v(24.05, -1.7) * mm, "end": v(24.05, -1.35) * mm});
            skLineSegment(sketch, "E2181", {"start": v(-0.68, -1.86) * mm, "end": v(-0.85, -1.52) * mm});
            skLineSegment(sketch, "E2182", {"start": v(0.5, -1.86) * mm, "end": v(0.34, -1.7) * mm});
            skLineSegment(sketch, "E2183", {"start": v(0.5, -1.86) * mm, "end": v(0.68, -1.7) * mm});
            skLineSegment(sketch, "E2184", {"start": v(0.85, -1.86) * mm, "end": v(0.68, -1.7) * mm});
            skLineSegment(sketch, "E2185", {"start": v(0.85, -1.86) * mm, "end": v(1.02, -1.7) * mm});
            skLineSegment(sketch, "E2186", {"start": v(1.19, -1.86) * mm, "end": v(1.02, -1.7) * mm});
            skLineSegment(sketch, "E2187", {"start": v(1.35, -1.86) * mm, "end": v(1.19, -1.86) * mm});
            skLineSegment(sketch, "E2188", {"start": v(1.35, -1.86) * mm, "end": v(1.52, -1.7) * mm});
            skLineSegment(sketch, "E2189", {"start": v(1.7, -1.86) * mm, "end": v(1.52, -1.7) * mm});
            skLineSegment(sketch, "E2190", {"start": v(2.2, -1.86) * mm, "end": v(2.03, -1.86) * mm});
            skLineSegment(sketch, "E2191", {"start": v(2.2, -1.86) * mm, "end": v(2.2, -1.7) * mm});
            skLineSegment(sketch, "E2192", {"start": v(21.17, -1.86) * mm, "end": v(20.7, -1.17) * mm});
            skLineSegment(sketch, "E2193", {"start": v(20.7, -1.17) * mm, "end": v(18.12, 1.19) * mm});
            skLineSegment(sketch, "E2194", {"start": v(18.12, 1.19) * mm, "end": v(16.8, 2.75) * mm});
            skLineSegment(sketch, "E2195", {"start": v(16.8, 2.75) * mm, "end": v(15.83, 4.3) * mm});
            skLineSegment(sketch, "E2196", {"start": v(15.83, 4.3) * mm, "end": v(14.9, 7.79) * mm});
            skLineSegment(sketch, "E2197", {"start": v(21.34, -1.86) * mm, "end": v(21.17, -1.86) * mm});
            skLineSegment(sketch, "E2198", {"start": v(-1.52, -2.03) * mm, "end": v(-1.52, -1.7) * mm});
            skLineSegment(sketch, "E2199", {"start": v(-0.68, -2.03) * mm, "end": v(-0.85, -2.03) * mm});
            skLineSegment(sketch, "E2200", {"start": v(-0.68, -2.03) * mm, "end": v(-0.68, -1.86) * mm});
            skLineSegment(sketch, "E2201", {"start": v(0.5, -2.03) * mm, "end": v(0.34, -2.03) * mm});
            skLineSegment(sketch, "E2202", {"start": v(0.5, -2.03) * mm, "end": v(0.5, -1.86) * mm});
            skLineSegment(sketch, "E2203", {"start": v(0.68, -2.03) * mm, "end": v(0.5, -2.03) * mm});
            skLineSegment(sketch, "E2204", {"start": v(0.68, -2.03) * mm, "end": v(0.85, -1.86) * mm});
            skLineSegment(sketch, "E2205", {"start": v(1.02, -2.03) * mm, "end": v(0.85, -1.86) * mm});
            skLineSegment(sketch, "E2206", {"start": v(1.02, -2.03) * mm, "end": v(1.19, -1.86) * mm});
            skLineSegment(sketch, "E2207", {"start": v(1.52, -2.03) * mm, "end": v(1.35, -1.86) * mm});
            skLineSegment(sketch, "E2208", {"start": v(1.52, -2.03) * mm, "end": v(1.7, -1.86) * mm});
            skLineSegment(sketch, "E2209", {"start": v(1.86, -2.03) * mm, "end": v(1.7, -1.86) * mm});
            skLineSegment(sketch, "E2210", {"start": v(1.86, -2.03) * mm, "end": v(2.03, -1.86) * mm});
            skLineSegment(sketch, "E2211", {"start": v(2.2, -2.03) * mm, "end": v(2.2, -1.86) * mm});
            skLineSegment(sketch, "E2212", {"start": v(21.17, -2.03) * mm, "end": v(21.17, -1.86) * mm});
            skLineSegment(sketch, "E2213", {"start": v(-1.35, -2.2) * mm, "end": v(-1.52, -2.03) * mm});
            skLineSegment(sketch, "E2214", {"start": v(0.5, -2.2) * mm, "end": v(0.5, -2.03) * mm});
            skLineSegment(sketch, "E2215", {"start": v(0.68, -2.2) * mm, "end": v(0.5, -2.2) * mm});
            skLineSegment(sketch, "E2216", {"start": v(0.68, -2.2) * mm, "end": v(0.68, -2.03) * mm});
            skLineSegment(sketch, "E2217", {"start": v(1.02, -2.2) * mm, "end": v(1.02, -2.03) * mm});
            skLineSegment(sketch, "E2218", {"start": v(1.35, -2.2) * mm, "end": v(1.52, -2.03) * mm});
            skLineSegment(sketch, "E2219", {"start": v(1.7, -2.2) * mm, "end": v(1.52, -2.03) * mm});
            skLineSegment(sketch, "E2220", {"start": v(1.7, -2.2) * mm, "end": v(1.86, -2.03) * mm});
            skLineSegment(sketch, "E2221", {"start": v(2.2, -2.2) * mm, "end": v(2.2, -2.03) * mm});
            skLineSegment(sketch, "E2222", {"start": v(2.37, -2.2) * mm, "end": v(2.2, -2.2) * mm});
            skLineSegment(sketch, "E2223", {"start": v(-1.86, -2.37) * mm, "end": v(-1.52, -2.03) * mm});
            skLineSegment(sketch, "E2224", {"start": v(-1.35, -2.37) * mm, "end": v(-1.35, -2.2) * mm});
            skLineSegment(sketch, "E2225", {"start": v(-1.19, -2.37) * mm, "end": v(-1.35, -2.37) * mm});
            skLineSegment(sketch, "E2226", {"start": v(-1.19, -2.37) * mm, "end": v(-0.85, -2.03) * mm});
            skLineSegment(sketch, "E2227", {"start": v(0.34, -2.37) * mm, "end": v(0.17, -2.2) * mm});
            skLineSegment(sketch, "E2228", {"start": v(0.17, -2.2) * mm, "end": v(0.34, -2.03) * mm});
            skLineSegment(sketch, "E2229", {"start": v(0.34, -2.37) * mm, "end": v(0.5, -2.2) * mm});
            skLineSegment(sketch, "E2230", {"start": v(0.85, -2.37) * mm, "end": v(0.68, -2.2) * mm});
            skLineSegment(sketch, "E2231", {"start": v(1.02, -2.37) * mm, "end": v(0.85, -2.37) * mm});
            skLineSegment(sketch, "E2232", {"start": v(1.02, -2.37) * mm, "end": v(1.02, -2.2) * mm});
            skLineSegment(sketch, "E2233", {"start": v(1.19, -2.37) * mm, "end": v(1.02, -2.37) * mm});
            skLineSegment(sketch, "E2234", {"start": v(1.35, -2.37) * mm, "end": v(1.19, -2.37) * mm});
            skLineSegment(sketch, "E2235", {"start": v(1.35, -2.37) * mm, "end": v(1.35, -2.2) * mm});
            skLineSegment(sketch, "E2236", {"start": v(1.52, -2.37) * mm, "end": v(1.35, -2.37) * mm});
            skLineSegment(sketch, "E2237", {"start": v(1.52, -2.37) * mm, "end": v(1.7, -2.2) * mm});
            skLineSegment(sketch, "E2238", {"start": v(1.86, -2.37) * mm, "end": v(1.7, -2.2) * mm});
            skLineSegment(sketch, "E2239", {"start": v(1.86, -2.37) * mm, "end": v(2.2, -2.2) * mm});
            skLineSegment(sketch, "E2240", {"start": v(-1.86, -2.54) * mm, "end": v(-1.86, -2.37) * mm});
            skLineSegment(sketch, "E2241", {"start": v(-1.7, -2.54) * mm, "end": v(-1.86, -2.54) * mm});
            skLineSegment(sketch, "E2242", {"start": v(-1.7, -2.54) * mm, "end": v(-1.35, -2.37) * mm});
            skLineSegment(sketch, "E2243", {"start": v(0.34, -2.37) * mm, "end": v(0.5, -2.54) * mm});
            skLineSegment(sketch, "E2244", {"start": v(0.5, -2.54) * mm, "end": v(0.85, -2.37) * mm});
            skLineSegment(sketch, "E2245", {"start": v(1.52, -2.37) * mm, "end": v(1.7, -2.54) * mm});
            skLineSegment(sketch, "E2246", {"start": v(1.7, -2.54) * mm, "end": v(1.86, -2.37) * mm});
            skLineSegment(sketch, "E2247", {"start": v(-1.86, -2.7) * mm, "end": v(-1.86, -2.54) * mm});
            skLineSegment(sketch, "E2248", {"start": v(-0.34, -3.05) * mm, "end": v(-0.54, -2.22) * mm});
            skLineSegment(sketch, "E2249", {"start": v(-0.54, -2.22) * mm, "end": v(-0.68, -2.03) * mm});
            skLineSegment(sketch, "E2250", {"start": v(-1.86, -3.22) * mm, "end": v(-1.86, -2.7) * mm});
            skLineSegment(sketch, "E2251", {"start": v(-0.34, -3.22) * mm, "end": v(-0.5, -3.22) * mm});
            skLineSegment(sketch, "E2252", {"start": v(-0.34, -3.22) * mm, "end": v(-0.34, -3.05) * mm});
            skLineSegment(sketch, "E2253", {"start": v(2.03, -3.22) * mm, "end": v(1.86, -3.22) * mm});
            skLineSegment(sketch, "E2254", {"start": v(2.2, -3.22) * mm, "end": v(2.03, -3.22) * mm});
            skLineSegment(sketch, "E2255", {"start": v(2.2, -3.22) * mm, "end": v(2.37, -3.22) * mm});
            skLineSegment(sketch, "E2256", {"start": v(2.37, -3.22) * mm, "end": v(2.54, -3.05) * mm});
            skLineSegment(sketch, "E2257", {"start": v(2.54, -3.05) * mm, "end": v(2.54, -2.37) * mm});
            skLineSegment(sketch, "E2258", {"start": v(2.54, -2.37) * mm, "end": v(2.37, -2.2) * mm});
            skLineSegment(sketch, "E2259", {"start": v(-1.86, -3.39) * mm, "end": v(-1.86, -3.22) * mm});
            skLineSegment(sketch, "E2260", {"start": v(-1.7, -3.39) * mm, "end": v(-1.86, -3.39) * mm});
            skLineSegment(sketch, "E2261", {"start": v(-1.02, -3.39) * mm, "end": v(-1.19, -3.22) * mm});
            skLineSegment(sketch, "E2262", {"start": v(-1.19, -3.22) * mm, "end": v(-1.52, -3.22) * mm});
            skLineSegment(sketch, "E2263", {"start": v(-1.52, -3.22) * mm, "end": v(-1.7, -3.39) * mm});
            skLineSegment(sketch, "E2264", {"start": v(-0.85, -3.39) * mm, "end": v(-1.02, -3.39) * mm});
            skLineSegment(sketch, "E2265", {"start": v(-0.85, -3.39) * mm, "end": v(-0.5, -3.22) * mm});
            skLineSegment(sketch, "E2266", {"start": v(2.03, -3.39) * mm, "end": v(2.03, -3.22) * mm});
            skLineSegment(sketch, "E2267", {"start": v(-1.86, -3.56) * mm, "end": v(-1.86, -3.39) * mm});
            skLineSegment(sketch, "E2268", {"start": v(-0.85, -3.56) * mm, "end": v(-0.85, -3.39) * mm});
            skLineSegment(sketch, "E2269", {"start": v(0.34, -3.56) * mm, "end": v(-0.34, -3.22) * mm});
            skLineSegment(sketch, "E2270", {"start": v(0.5, -3.56) * mm, "end": v(0.34, -3.56) * mm});
            skLineSegment(sketch, "E2271", {"start": v(0.5, -3.56) * mm, "end": v(1.37, -3.28) * mm});
            skLineSegment(sketch, "E2272", {"start": v(1.37, -3.28) * mm, "end": v(1.86, -3.22) * mm});
            skLineSegment(sketch, "E2273", {"start": v(-7.79, -3.73) * mm, "end": v(-8.3, 0.17) * mm});
            skLineSegment(sketch, "E2274", {"start": v(-8.3, 0.17) * mm, "end": v(-8.62, 0.37) * mm});
            skLineSegment(sketch, "E2275", {"start": v(-8.62, 0.37) * mm, "end": v(-9.65, 0.85) * mm});
            skLineSegment(sketch, "E2276", {"start": v(0.5, -3.73) * mm, "end": v(0.5, -3.56) * mm});
            skLineSegment(sketch, "E2277", {"start": v(-8.64, -3.9) * mm, "end": v(-8.47, -1.19) * mm});
            skLineSegment(sketch, "E2278", {"start": v(-8.47, -1.19) * mm, "end": v(-8.6, -0.66) * mm});
            skLineSegment(sketch, "E2279", {"start": v(-8.6, -0.66) * mm, "end": v(-8.64, -0.5) * mm});
            skLineSegment(sketch, "E2280", {"start": v(-8.64, -0.5) * mm, "end": v(-9.3, -0.14) * mm});
            skLineSegment(sketch, "E2281", {"start": v(-9.3, -0.14) * mm, "end": v(-10.33, 0.34) * mm});
            skLineSegment(sketch, "E2282", {"start": v(-7.79, -3.9) * mm, "end": v(-7.96, -3.9) * mm});
            skLineSegment(sketch, "E2283", {"start": v(-7.79, -3.9) * mm, "end": v(-7.79, -3.73) * mm});
            skLineSegment(sketch, "E2284", {"start": v(-8.64, -4.06) * mm, "end": v(-8.8, -4.06) * mm});
            skLineSegment(sketch, "E2285", {"start": v(-8.64, -4.06) * mm, "end": v(-8.64, -3.9) * mm});
            skLineSegment(sketch, "E2286", {"start": v(-8.47, -4.23) * mm, "end": v(-8.64, -4.06) * mm});
            skLineSegment(sketch, "E2287", {"start": v(-8.47, -4.23) * mm, "end": v(-7.96, -3.9) * mm});
            skLineSegment(sketch, "E2288", {"start": v(-7.62, -4.23) * mm, "end": v(-7.79, -3.9) * mm});
            skLineSegment(sketch, "E2289", {"start": v(-6.94, -4.23) * mm, "end": v(-7.28, -1.35) * mm});
            skLineSegment(sketch, "E2290", {"start": v(-7.28, -1.35) * mm, "end": v(-7.16, -0.83) * mm});
            skLineSegment(sketch, "E2291", {"start": v(-7.16, -0.83) * mm, "end": v(-7.11, -0.5) * mm});
            skLineSegment(sketch, "E2292", {"start": v(-7.11, -0.5) * mm, "end": v(-6.6, 0) * mm});
            skLineSegment(sketch, "E2293", {"start": v(-6.6, 0) * mm, "end": v(-6.43, 0) * mm});
            skLineSegment(sketch, "E2294", {"start": v(-14.56, -4.4) * mm, "end": v(-16.26, -1.52) * mm});
            skLineSegment(sketch, "E2295", {"start": v(-14.56, -4.4) * mm, "end": v(-13.87, -3.93) * mm});
            skLineSegment(sketch, "E2296", {"start": v(-13.87, -3.93) * mm, "end": v(-12.36, -3.05) * mm});
            skLineSegment(sketch, "E2297", {"start": v(-12.36, -3.05) * mm, "end": v(-11, -1.52) * mm});
            skLineSegment(sketch, "E2298", {"start": v(-9.48, -4.4) * mm, "end": v(-9.42, -3.74) * mm});
            skLineSegment(sketch, "E2299", {"start": v(-9.42, -3.74) * mm, "end": v(-9.31, -3.56) * mm});
            skLineSegment(sketch, "E2300", {"start": v(-9.31, -3.56) * mm, "end": v(-9.31, -1.52) * mm});
            skLineSegment(sketch, "E2301", {"start": v(-9.31, -1.52) * mm, "end": v(-9.82, -1.02) * mm});
            skLineSegment(sketch, "E2302", {"start": v(-9.82, -1.02) * mm, "end": v(-10.84, -1.35) * mm});
            skLineSegment(sketch, "E2303", {"start": v(-7.62, -4.4) * mm, "end": v(-7.62, -4.23) * mm});
            skLineSegment(sketch, "E2304", {"start": v(-7.45, -4.4) * mm, "end": v(-7.62, -4.4) * mm});
            skLineSegment(sketch, "E2305", {"start": v(-7.11, -4.4) * mm, "end": v(-7.45, -4.4) * mm});
            skLineSegment(sketch, "E2306", {"start": v(-6.94, -4.4) * mm, "end": v(-7.11, -4.4) * mm});
            skLineSegment(sketch, "E2307", {"start": v(-6.94, -4.4) * mm, "end": v(-6.94, -4.23) * mm});
            skLineSegment(sketch, "E2308", {"start": v(-0.85, -4.4) * mm, "end": v(-0.68, -4.23) * mm});
            skLineSegment(sketch, "E2309", {"start": v(-0.68, -4.23) * mm, "end": v(-0.68, -3.73) * mm});
            skLineSegment(sketch, "E2310", {"start": v(-0.68, -3.73) * mm, "end": v(-0.85, -3.56) * mm});
            skLineSegment(sketch, "E2311", {"start": v(-9.31, -4.57) * mm, "end": v(-9.48, -4.4) * mm});
            skLineSegment(sketch, "E2312", {"start": v(-9.14, -4.57) * mm, "end": v(-9.31, -4.57) * mm});
            skLineSegment(sketch, "E2313", {"start": v(-9.14, -4.57) * mm, "end": v(-8.8, -4.06) * mm});
            skLineSegment(sketch, "E2314", {"start": v(-8.47, -4.57) * mm, "end": v(-8.47, -4.23) * mm});
            skLineSegment(sketch, "E2315", {"start": v(-0.85, -4.57) * mm, "end": v(-1.02, -4.57) * mm});
            skLineSegment(sketch, "E2316", {"start": v(-0.85, -4.57) * mm, "end": v(-0.85, -4.4) * mm});
            skLineSegment(sketch, "E2317", {"start": v(-14.56, -4.74) * mm, "end": v(-14.56, -4.4) * mm});
            skLineSegment(sketch, "E2318", {"start": v(-9.31, -4.74) * mm, "end": v(-9.31, -4.57) * mm});
            skLineSegment(sketch, "E2319", {"start": v(-8.47, -4.74) * mm, "end": v(-8.47, -4.57) * mm});
            skLineSegment(sketch, "E2320", {"start": v(-8.3, -4.74) * mm, "end": v(-8.47, -4.74) * mm});
            skLineSegment(sketch, "E2321", {"start": v(-8.3, -4.74) * mm, "end": v(-7.62, -4.4) * mm});
            skLineSegment(sketch, "E2322", {"start": v(-6.6, -4.74) * mm, "end": v(-6.94, -4.4) * mm});
            skLineSegment(sketch, "E2323", {"start": v(-0.68, -4.74) * mm, "end": v(-0.85, -4.57) * mm});
            skLineSegment(sketch, "E2324", {"start": v(21.5, -4.74) * mm, "end": v(21.43, -3.05) * mm});
            skLineSegment(sketch, "E2325", {"start": v(21.43, -3.05) * mm, "end": v(21.17, -2.03) * mm});
            skLineSegment(sketch, "E2326", {"start": v(-9.48, -4.91) * mm, "end": v(-9.65, -4.74) * mm});
            skLineSegment(sketch, "E2327", {"start": v(-9.65, -4.74) * mm, "end": v(-9.48, -4.4) * mm});
            skLineSegment(sketch, "E2328", {"start": v(-9.31, -4.91) * mm, "end": v(-9.48, -4.91) * mm});
            skLineSegment(sketch, "E2329", {"start": v(-9.31, -4.91) * mm, "end": v(-9.31, -4.74) * mm});
            skLineSegment(sketch, "E2330", {"start": v(-8.64, -4.91) * mm, "end": v(-8.47, -4.74) * mm});
            skLineSegment(sketch, "E2331", {"start": v(-6.6, -4.91) * mm, "end": v(-6.77, -4.91) * mm});
            skLineSegment(sketch, "E2332", {"start": v(-6.6, -4.91) * mm, "end": v(-6.6, -4.74) * mm});
            skLineSegment(sketch, "E2333", {"start": v(-1.19, -4.91) * mm, "end": v(-1.02, -4.57) * mm});
            skLineSegment(sketch, "E2334", {"start": v(21.5, -4.91) * mm, "end": v(21.34, -4.91) * mm});
            skLineSegment(sketch, "E2335", {"start": v(21.5, -4.91) * mm, "end": v(21.5, -4.74) * mm});
            skLineSegment(sketch, "E2336", {"start": v(-9.31, -4.91) * mm, "end": v(-9.14, -5.08) * mm});
            skLineSegment(sketch, "E2337", {"start": v(-9.14, -5.08) * mm, "end": v(-8.79, -4.94) * mm});
            skLineSegment(sketch, "E2338", {"start": v(-8.79, -4.94) * mm, "end": v(-8.64, -4.91) * mm});
            skLineSegment(sketch, "E2339", {"start": v(-6.6, -5.08) * mm, "end": v(-6.6, -4.91) * mm});
            skLineSegment(sketch, "E2340", {"start": v(-1.35, -5.08) * mm, "end": v(-1.19, -4.91) * mm});
            skLineSegment(sketch, "E2341", {"start": v(-1.02, -5.08) * mm, "end": v(-1.19, -4.91) * mm});
            skLineSegment(sketch, "E2342", {"start": v(-1.02, -5.08) * mm, "end": v(-0.68, -4.74) * mm});
            skLineSegment(sketch, "E2343", {"start": v(2.03, 2.88) * mm, "end": v(3.51, 1.15) * mm});
            skLineSegment(sketch, "E2344", {"start": v(3.51, 1.15) * mm, "end": v(4.2, -0.02) * mm});
            skLineSegment(sketch, "E2345", {"start": v(4.2, -0.02) * mm, "end": v(4.44, -0.5) * mm});
            skLineSegment(sketch, "E2346", {"start": v(4.44, -0.5) * mm, "end": v(4.83, -2.04) * mm});
            skLineSegment(sketch, "E2347", {"start": v(4.83, -2.04) * mm, "end": v(4.91, -4.91) * mm});
            skLineSegment(sketch, "E2348", {"start": v(4.91, -4.91) * mm, "end": v(5.08, -5.08) * mm});
            skLineSegment(sketch, "E2349", {"start": v(5.08, -5.08) * mm, "end": v(5.93, -5.08) * mm});
            skLineSegment(sketch, "E2350", {"start": v(5.93, -5.08) * mm, "end": v(6.27, -4.74) * mm});
            skLineSegment(sketch, "E2351", {"start": v(6.27, -4.74) * mm, "end": v(6.27, -2.54) * mm});
            skLineSegment(sketch, "E2352", {"start": v(6.27, -2.54) * mm, "end": v(5.87, -1.03) * mm});
            skLineSegment(sketch, "E2353", {"start": v(5.87, -1.03) * mm, "end": v(5.59, -0.34) * mm});
            skLineSegment(sketch, "E2354", {"start": v(16.76, -5.08) * mm, "end": v(14.9, -4.06) * mm});
            skLineSegment(sketch, "E2355", {"start": v(14.9, -4.06) * mm, "end": v(14.02, -2.9) * mm});
            skLineSegment(sketch, "E2356", {"start": v(14.02, -2.9) * mm, "end": v(13.27, -1) * mm});
            skLineSegment(sketch, "E2357", {"start": v(13.27, -1) * mm, "end": v(13.2, -0.5) * mm});
            skLineSegment(sketch, "E2358", {"start": v(21.5, -5.08) * mm, "end": v(21.5, -4.91) * mm});
            skLineSegment(sketch, "E2359", {"start": v(-8.3, -5.25) * mm, "end": v(-8.64, -4.91) * mm});
            skLineSegment(sketch, "E2360", {"start": v(-8.3, -5.25) * mm, "end": v(-7.6, -4.98) * mm});
            skLineSegment(sketch, "E2361", {"start": v(-7.6, -4.98) * mm, "end": v(-6.77, -4.91) * mm});
            skLineSegment(sketch, "E2362", {"start": v(-1.19, -5.25) * mm, "end": v(-1.35, -5.08) * mm});
            skLineSegment(sketch, "E2363", {"start": v(-1.19, -5.25) * mm, "end": v(-1.02, -5.08) * mm});
            skLineSegment(sketch, "E2364", {"start": v(0.5, -5.25) * mm, "end": v(0.68, -5.08) * mm});
            skLineSegment(sketch, "E2365", {"start": v(0.68, -5.08) * mm, "end": v(0.58, -4.73) * mm});
            skLineSegment(sketch, "E2366", {"start": v(0.58, -4.73) * mm, "end": v(0.5, -3.73) * mm});
            skLineSegment(sketch, "E2367", {"start": v(8.97, -5.25) * mm, "end": v(8.8, -5.25) * mm});
            skLineSegment(sketch, "E2368", {"start": v(16.76, -5.25) * mm, "end": v(16.76, -5.08) * mm});
            skLineSegment(sketch, "E2369", {"start": v(16.93, -5.25) * mm, "end": v(16.76, -5.25) * mm});
            skLineSegment(sketch, "E2370", {"start": v(17.44, -5.25) * mm, "end": v(17.27, -5.08) * mm});
            skLineSegment(sketch, "E2371", {"start": v(17.27, -5.08) * mm, "end": v(16.93, -5.25) * mm});
            skLineSegment(sketch, "E2372", {"start": v(17.78, -5.25) * mm, "end": v(17.73, -4.93) * mm});
            skLineSegment(sketch, "E2373", {"start": v(17.73, -4.93) * mm, "end": v(17.61, -4.74) * mm});
            skLineSegment(sketch, "E2374", {"start": v(17.61, -4.74) * mm, "end": v(17.61, -2.7) * mm});
            skLineSegment(sketch, "E2375", {"start": v(17.61, -2.7) * mm, "end": v(17.85, -1.7) * mm});
            skLineSegment(sketch, "E2376", {"start": v(17.85, -1.7) * mm, "end": v(18.12, -0.85) * mm});
            skLineSegment(sketch, "E2377", {"start": v(-1.86, -5.42) * mm, "end": v(-1.86, -3.56) * mm});
            skLineSegment(sketch, "E2378", {"start": v(-1.52, -5.42) * mm, "end": v(-1.35, -5.08) * mm});
            skLineSegment(sketch, "E2379", {"start": v(-1.19, -5.42) * mm, "end": v(-1.19, -5.25) * mm});
            skLineSegment(sketch, "E2380", {"start": v(-0.5, -5.42) * mm, "end": v(-0.5, -4.91) * mm});
            skLineSegment(sketch, "E2381", {"start": v(-0.5, -4.91) * mm, "end": v(-0.68, -4.74) * mm});
            skLineSegment(sketch, "E2382", {"start": v(0.5, -5.42) * mm, "end": v(0.34, -5.42) * mm});
            skLineSegment(sketch, "E2383", {"start": v(0.5, -5.42) * mm, "end": v(0.5, -5.25) * mm});
            skLineSegment(sketch, "E2384", {"start": v(8.8, -5.42) * mm, "end": v(8.8, -5.25) * mm});
            skLineSegment(sketch, "E2385", {"start": v(9.31, -5.42) * mm, "end": v(8.97, -5.25) * mm});
            skLineSegment(sketch, "E2386", {"start": v(10, -5.42) * mm, "end": v(9.91, -3.05) * mm});
            skLineSegment(sketch, "E2387", {"start": v(9.91, -3.05) * mm, "end": v(9.76, -2.21) * mm});
            skLineSegment(sketch, "E2388", {"start": v(9.76, -2.21) * mm, "end": v(9.65, -2.03) * mm});
            skLineSegment(sketch, "E2389", {"start": v(9.65, -2.03) * mm, "end": v(9.65, -0.85) * mm});
            skLineSegment(sketch, "E2390", {"start": v(9.65, -0.85) * mm, "end": v(9.82, -0.5) * mm});
            skLineSegment(sketch, "E2391", {"start": v(9.82, -0.5) * mm, "end": v(10.3, -0.13) * mm});
            skLineSegment(sketch, "E2392", {"start": v(10.3, -0.13) * mm, "end": v(11, 0.5) * mm});
            skLineSegment(sketch, "E2393", {"start": v(16.76, -5.42) * mm, "end": v(16.76, -5.25) * mm});
            skLineSegment(sketch, "E2394", {"start": v(17.44, -5.42) * mm, "end": v(17.44, -5.25) * mm});
            skLineSegment(sketch, "E2395", {"start": v(17.61, -5.42) * mm, "end": v(17.44, -5.42) * mm});
            skLineSegment(sketch, "E2396", {"start": v(17.78, -5.42) * mm, "end": v(17.61, -5.42) * mm});
            skLineSegment(sketch, "E2397", {"start": v(17.78, -5.42) * mm, "end": v(17.78, -5.25) * mm});
            skLineSegment(sketch, "E2398", {"start": v(-1.86, -5.59) * mm, "end": v(-2.03, -5.59) * mm});
            skLineSegment(sketch, "E2399", {"start": v(-1.86, -5.59) * mm, "end": v(-1.86, -5.42) * mm});
            skLineSegment(sketch, "E2400", {"start": v(-1.7, -5.59) * mm, "end": v(-1.86, -5.59) * mm});
            skLineSegment(sketch, "E2401", {"start": v(-1.52, -5.59) * mm, "end": v(-1.7, -5.59) * mm});
            skLineSegment(sketch, "E2402", {"start": v(-1.52, -5.59) * mm, "end": v(-1.52, -5.42) * mm});
            skLineSegment(sketch, "E2403", {"start": v(-1.35, -5.59) * mm, "end": v(-1.52, -5.59) * mm});
            skLineSegment(sketch, "E2404", {"start": v(-1.19, -5.59) * mm, "end": v(-1.35, -5.59) * mm});
            skLineSegment(sketch, "E2405", {"start": v(-1.19, -5.59) * mm, "end": v(-1.19, -5.42) * mm});
            skLineSegment(sketch, "E2406", {"start": v(-0.5, -5.59) * mm, "end": v(-0.5, -5.42) * mm});
            skLineSegment(sketch, "E2407", {"start": v(-0.34, -5.59) * mm, "end": v(-0.5, -5.59) * mm});
            skLineSegment(sketch, "E2408", {"start": v(-0.34, -5.59) * mm, "end": v(-0.17, -5.42) * mm});
            skLineSegment(sketch, "E2409", {"start": v(-0.17, -5.42) * mm, "end": v(0.34, -5.42) * mm});
            skLineSegment(sketch, "E2410", {"start": v(0.68, -5.59) * mm, "end": v(0.5, -5.42) * mm});
            skLineSegment(sketch, "E2411", {"start": v(0.85, -5.59) * mm, "end": v(0.68, -5.59) * mm});
            skLineSegment(sketch, "E2412", {"start": v(8.8, -5.59) * mm, "end": v(8.64, -5.59) * mm});
            skLineSegment(sketch, "E2413", {"start": v(8.8, -5.59) * mm, "end": v(8.8, -5.42) * mm});
            skLineSegment(sketch, "E2414", {"start": v(8.97, -5.59) * mm, "end": v(8.8, -5.59) * mm});
            skLineSegment(sketch, "E2415", {"start": v(9.14, -5.59) * mm, "end": v(8.97, -5.59) * mm});
            skLineSegment(sketch, "E2416", {"start": v(9.31, -5.59) * mm, "end": v(9.14, -5.59) * mm});
            skLineSegment(sketch, "E2417", {"start": v(9.31, -5.59) * mm, "end": v(9.31, -5.42) * mm});
            skLineSegment(sketch, "E2418", {"start": v(9.48, -5.59) * mm, "end": v(9.31, -5.59) * mm});
            skLineSegment(sketch, "E2419", {"start": v(10, -5.59) * mm, "end": v(10, -5.42) * mm});
            skLineSegment(sketch, "E2420", {"start": v(10.16, -5.59) * mm, "end": v(10, -5.59) * mm});
            skLineSegment(sketch, "E2421", {"start": v(10.5, -5.59) * mm, "end": v(10.53, -5.44) * mm});
            skLineSegment(sketch, "E2422", {"start": v(10.53, -5.44) * mm, "end": v(10.67, -5.25) * mm});
            skLineSegment(sketch, "E2423", {"start": v(10.67, -5.25) * mm, "end": v(10.67, -2.88) * mm});
            skLineSegment(sketch, "E2424", {"start": v(10.67, -2.88) * mm, "end": v(10.44, -2.22) * mm});
            skLineSegment(sketch, "E2425", {"start": v(10.44, -2.22) * mm, "end": v(10.28, -1.71) * mm});
            skLineSegment(sketch, "E2426", {"start": v(10.28, -1.71) * mm, "end": v(10.16, -1.02) * mm});
            skLineSegment(sketch, "E2427", {"start": v(10.16, -1.02) * mm, "end": v(11, -0.17) * mm});
            skLineSegment(sketch, "E2428", {"start": v(11, -0.17) * mm, "end": v(12.2, 0.5) * mm});
            skLineSegment(sketch, "E2429", {"start": v(17.44, -5.59) * mm, "end": v(17.44, -5.42) * mm});
            skLineSegment(sketch, "E2430", {"start": v(-1.19, -5.76) * mm, "end": v(-1.19, -5.59) * mm});
            skLineSegment(sketch, "E2431", {"start": v(-0.68, -5.76) * mm, "end": v(-0.5, -5.59) * mm});
            skLineSegment(sketch, "E2432", {"start": v(0.68, -5.76) * mm, "end": v(0.68, -5.59) * mm});
            skLineSegment(sketch, "E2433", {"start": v(10, -5.76) * mm, "end": v(10, -5.59) * mm});
            skLineSegment(sketch, "E2434", {"start": v(10.33, -5.76) * mm, "end": v(10.16, -5.59) * mm});
            skLineSegment(sketch, "E2435", {"start": v(10.5, -5.76) * mm, "end": v(10.33, -5.76) * mm});
            skLineSegment(sketch, "E2436", {"start": v(10.5, -5.76) * mm, "end": v(10.5, -5.59) * mm});
            skLineSegment(sketch, "E2437", {"start": v(10.67, -5.76) * mm, "end": v(10.5, -5.76) * mm});
            skLineSegment(sketch, "E2438", {"start": v(-0.85, -5.93) * mm, "end": v(-1.19, -5.76) * mm});
            skLineSegment(sketch, "E2439", {"start": v(-0.68, -5.93) * mm, "end": v(-0.85, -5.93) * mm});
            skLineSegment(sketch, "E2440", {"start": v(-0.68, -5.93) * mm, "end": v(-0.68, -5.76) * mm});
            skLineSegment(sketch, "E2441", {"start": v(9.82, -5.93) * mm, "end": v(9.48, -5.59) * mm});
            skLineSegment(sketch, "E2442", {"start": v(10, -5.93) * mm, "end": v(9.82, -5.93) * mm});
            skLineSegment(sketch, "E2443", {"start": v(10, -5.93) * mm, "end": v(10, -5.76) * mm});
            skLineSegment(sketch, "E2444", {"start": v(10.5, -5.93) * mm, "end": v(10.5, -5.76) * mm});
            skLineSegment(sketch, "E2445", {"start": v(-14.9, -6.1) * mm, "end": v(-14.67, -4.93) * mm});
            skLineSegment(sketch, "E2446", {"start": v(-14.67, -4.93) * mm, "end": v(-14.56, -4.74) * mm});
            skLineSegment(sketch, "E2447", {"start": v(-0.68, -6.1) * mm, "end": v(-0.68, -5.93) * mm});
            skLineSegment(sketch, "E2448", {"start": v(0.85, -6.1) * mm, "end": v(0.68, -5.76) * mm});
            skLineSegment(sketch, "E2449", {"start": v(1.86, -6.1) * mm, "end": v(2.03, -5.93) * mm});
            skLineSegment(sketch, "E2450", {"start": v(2.03, -5.93) * mm, "end": v(2.03, -3.39) * mm});
            skLineSegment(sketch, "E2451", {"start": v(10, -6.1) * mm, "end": v(10, -5.93) * mm});
            skLineSegment(sketch, "E2452", {"start": v(10.5, -6.1) * mm, "end": v(10.5, -5.93) * mm});
            skLineSegment(sketch, "E2453", {"start": v(11.51, -6.1) * mm, "end": v(11.35, -5.25) * mm});
            skLineSegment(sketch, "E2454", {"start": v(11.35, -5.25) * mm, "end": v(11.6, -3.55) * mm});
            skLineSegment(sketch, "E2455", {"start": v(11.6, -3.55) * mm, "end": v(11.68, -1.52) * mm});
            skLineSegment(sketch, "E2456", {"start": v(11.68, -1.52) * mm, "end": v(12.5, -0.8) * mm});
            skLineSegment(sketch, "E2457", {"start": v(12.5, -0.8) * mm, "end": v(13.04, -0.34) * mm});
            skLineSegment(sketch, "E2458", {"start": v(21.5, -5.08) * mm, "end": v(21.57, -5.57) * mm});
            skLineSegment(sketch, "E2459", {"start": v(21.57, -5.57) * mm, "end": v(21.84, -6.1) * mm});
            skLineSegment(sketch, "E2460", {"start": v(21.84, -6.1) * mm, "end": v(22.18, -5.93) * mm});
            skLineSegment(sketch, "E2461", {"start": v(22.18, -5.93) * mm, "end": v(21.84, -5.25) * mm});
            skLineSegment(sketch, "E2462", {"start": v(21.84, -5.25) * mm, "end": v(21.84, -4.06) * mm});
            skLineSegment(sketch, "E2463", {"start": v(21.84, -4.06) * mm, "end": v(22.01, -3.9) * mm});
            skLineSegment(sketch, "E2464", {"start": v(22.01, -3.9) * mm, "end": v(22.01, -2.7) * mm});
            skLineSegment(sketch, "E2465", {"start": v(22.01, -2.7) * mm, "end": v(21.34, -1.86) * mm});
            skLineSegment(sketch, "E2466", {"start": v(0.85, -6.27) * mm, "end": v(0.85, -6.1) * mm});
            skLineSegment(sketch, "E2467", {"start": v(1.02, -6.27) * mm, "end": v(0.85, -6.27) * mm});
            skLineSegment(sketch, "E2468", {"start": v(1.02, -6.27) * mm, "end": v(1.35, -5.93) * mm});
            skLineSegment(sketch, "E2469", {"start": v(1.35, -5.93) * mm, "end": v(1.35, -5.59) * mm});
            skLineSegment(sketch, "E2470", {"start": v(1.35, -5.59) * mm, "end": v(1.19, -5.42) * mm});
            skLineSegment(sketch, "E2471", {"start": v(1.19, -5.42) * mm, "end": v(0.85, -5.59) * mm});
            skLineSegment(sketch, "E2472", {"start": v(1.86, -6.27) * mm, "end": v(1.86, -6.1) * mm});
            skLineSegment(sketch, "E2473", {"start": v(2.03, -6.27) * mm, "end": v(1.86, -6.27) * mm});
            skLineSegment(sketch, "E2474", {"start": v(10.33, -6.27) * mm, "end": v(10, -6.1) * mm});
            skLineSegment(sketch, "E2475", {"start": v(10.5, -6.27) * mm, "end": v(10.33, -6.27) * mm});
            skLineSegment(sketch, "E2476", {"start": v(10.5, -6.27) * mm, "end": v(10.5, -6.1) * mm});
            skLineSegment(sketch, "E2477", {"start": v(11.18, -6.27) * mm, "end": v(10.67, -5.76) * mm});
            skLineSegment(sketch, "E2478", {"start": v(11.35, -6.27) * mm, "end": v(11.18, -6.27) * mm});
            skLineSegment(sketch, "E2479", {"start": v(11.35, -6.27) * mm, "end": v(11.51, -6.27) * mm});
            skLineSegment(sketch, "E2480", {"start": v(11.51, -6.27) * mm, "end": v(11.51, -6.1) * mm});
            skLineSegment(sketch, "E2481", {"start": v(0.85, -6.43) * mm, "end": v(0.85, -6.27) * mm});
            skLineSegment(sketch, "E2482", {"start": v(1.86, -6.43) * mm, "end": v(1.86, -6.27) * mm});
            skLineSegment(sketch, "E2483", {"start": v(10.5, -6.43) * mm, "end": v(10.5, -6.27) * mm});
            skLineSegment(sketch, "E2484", {"start": v(11.18, -6.43) * mm, "end": v(11.18, -6.27) * mm});
            skLineSegment(sketch, "E2485", {"start": v(18.12, -6.6) * mm, "end": v(17.78, -5.42) * mm});
            skLineSegment(sketch, "E2486", {"start": v(10.84, -6.77) * mm, "end": v(10.5, -6.43) * mm});
            skLineSegment(sketch, "E2487", {"start": v(11, -6.77) * mm, "end": v(10.84, -6.77) * mm});
            skLineSegment(sketch, "E2488", {"start": v(11, -6.77) * mm, "end": v(11.18, -6.43) * mm});
            skLineSegment(sketch, "E2489", {"start": v(-0.34, -6.94) * mm, "end": v(-0.68, -6.1) * mm});
            skLineSegment(sketch, "E2490", {"start": v(11, -6.94) * mm, "end": v(11, -6.77) * mm});
            skLineSegment(sketch, "E2491", {"start": v(-0.34, -7.11) * mm, "end": v(-0.5, -7.11) * mm});
            skLineSegment(sketch, "E2492", {"start": v(-0.34, -7.11) * mm, "end": v(-0.34, -6.94) * mm});
            skLineSegment(sketch, "E2493", {"start": v(1.02, -7.11) * mm, "end": v(0.85, -6.94) * mm});
            skLineSegment(sketch, "E2494", {"start": v(0.85, -6.94) * mm, "end": v(0.85, -6.43) * mm});
            skLineSegment(sketch, "E2495", {"start": v(1.02, -7.11) * mm, "end": v(1.86, -6.43) * mm});
            skLineSegment(sketch, "E2496", {"start": v(-15.4, -7.28) * mm, "end": v(-15.04, -6.28) * mm});
            skLineSegment(sketch, "E2497", {"start": v(-15.04, -6.28) * mm, "end": v(-14.9, -6.1) * mm});
            skLineSegment(sketch, "E2498", {"start": v(1.02, -7.28) * mm, "end": v(0.85, -7.28) * mm});
            skLineSegment(sketch, "E2499", {"start": v(1.02, -7.28) * mm, "end": v(1.02, -7.11) * mm});
            skLineSegment(sketch, "E2500", {"start": v(3.05, -7.28) * mm, "end": v(2.88, -6.77) * mm});
            skLineSegment(sketch, "E2501", {"start": v(2.88, -6.77) * mm, "end": v(2.39, -6.4) * mm});
            skLineSegment(sketch, "E2502", {"start": v(2.39, -6.4) * mm, "end": v(2.03, -6.27) * mm});
            skLineSegment(sketch, "E2503", {"start": v(18.46, -7.28) * mm, "end": v(18.46, -6.94) * mm});
            skLineSegment(sketch, "E2504", {"start": v(18.46, -6.94) * mm, "end": v(18.12, -6.6) * mm});
            skLineSegment(sketch, "E2505", {"start": v(-0.34, -7.11) * mm, "end": v(0, -7.45) * mm});
            skLineSegment(sketch, "E2506", {"start": v(0, -7.45) * mm, "end": v(0.68, -7.45) * mm});
            skLineSegment(sketch, "E2507", {"start": v(0.68, -7.45) * mm, "end": v(0.85, -7.28) * mm});
            skLineSegment(sketch, "E2508", {"start": v(2.88, -7.45) * mm, "end": v(1.19, -7.45) * mm});
            skLineSegment(sketch, "E2509", {"start": v(1.19, -7.45) * mm, "end": v(1.02, -7.28) * mm});
            skLineSegment(sketch, "E2510", {"start": v(3.05, -7.45) * mm, "end": v(2.88, -7.45) * mm});
            skLineSegment(sketch, "E2511", {"start": v(3.05, -7.45) * mm, "end": v(3.05, -7.28) * mm});
            skLineSegment(sketch, "E2512", {"start": v(3.22, -7.62) * mm, "end": v(3.05, -7.45) * mm});
            skLineSegment(sketch, "E2513", {"start": v(3.22, -7.79) * mm, "end": v(3.05, -7.79) * mm});
            skLineSegment(sketch, "E2514", {"start": v(3.22, -7.79) * mm, "end": v(3.22, -7.62) * mm});
            skLineSegment(sketch, "E2515", {"start": v(4.4, -7.79) * mm, "end": v(4.9, -7.42) * mm});
            skLineSegment(sketch, "E2516", {"start": v(4.9, -7.42) * mm, "end": v(6.1, -7.11) * mm});
            skLineSegment(sketch, "E2517", {"start": v(6.1, -7.11) * mm, "end": v(6.23, -6.42) * mm});
            skLineSegment(sketch, "E2518", {"start": v(6.23, -6.42) * mm, "end": v(6.43, -5.93) * mm});
            skLineSegment(sketch, "E2519", {"start": v(6.43, -5.93) * mm, "end": v(7.62, -4.91) * mm});
            skLineSegment(sketch, "E2520", {"start": v(7.62, -4.91) * mm, "end": v(8.3, -4.91) * mm});
            skLineSegment(sketch, "E2521", {"start": v(8.3, -4.91) * mm, "end": v(8.8, -5.25) * mm});
            skLineSegment(sketch, "E2522", {"start": v(11.68, -7.79) * mm, "end": v(11, -6.94) * mm});
            skLineSegment(sketch, "E2523", {"start": v(11.85, -7.79) * mm, "end": v(11.68, -7.79) * mm});
            skLineSegment(sketch, "E2524", {"start": v(12.02, -7.79) * mm, "end": v(11.85, -7.79) * mm});
            skLineSegment(sketch, "E2525", {"start": v(-15.75, -7.96) * mm, "end": v(-15.75, -7.62) * mm});
            skLineSegment(sketch, "E2526", {"start": v(-15.75, -7.62) * mm, "end": v(-15.4, -7.28) * mm});
            skLineSegment(sketch, "E2527", {"start": v(4.4, -7.96) * mm, "end": v(4.23, -7.96) * mm});
            skLineSegment(sketch, "E2528", {"start": v(4.4, -7.96) * mm, "end": v(4.4, -7.79) * mm});
            skLineSegment(sketch, "E2529", {"start": v(11.85, -7.96) * mm, "end": v(11.85, -7.79) * mm});
            skLineSegment(sketch, "E2530", {"start": v(-15.75, -8.13) * mm, "end": v(-15.92, -8.13) * mm});
            skLineSegment(sketch, "E2531", {"start": v(-15.75, -8.13) * mm, "end": v(-15.75, -7.96) * mm});
            skLineSegment(sketch, "E2532", {"start": v(3.9, -8.13) * mm, "end": v(3.22, -7.79) * mm});
            skLineSegment(sketch, "E2533", {"start": v(3.9, -8.13) * mm, "end": v(4.23, -7.96) * mm});
            skLineSegment(sketch, "E2534", {"start": v(-15.75, -8.3) * mm, "end": v(-15.75, -8.13) * mm});
            skLineSegment(sketch, "E2535", {"start": v(14.9, -8.3) * mm, "end": v(14.58, -8.1) * mm});
            skLineSegment(sketch, "E2536", {"start": v(14.58, -8.1) * mm, "end": v(13.55, -7.62) * mm});
            skLineSegment(sketch, "E2537", {"start": v(13.55, -7.62) * mm, "end": v(12.2, -7.62) * mm});
            skLineSegment(sketch, "E2538", {"start": v(12.2, -7.62) * mm, "end": v(12.02, -7.79) * mm});
            skLineSegment(sketch, "E2539", {"start": v(25.9, -8.3) * mm, "end": v(24.99, -0.85) * mm});
            skLineSegment(sketch, "E2540", {"start": v(24.99, -0.85) * mm, "end": v(23.76, 10.35) * mm});
            skLineSegment(sketch, "E2541", {"start": v(23.76, 10.35) * mm, "end": v(23.4, 11.36) * mm});
            skLineSegment(sketch, "E2542", {"start": v(23.4, 11.36) * mm, "end": v(23.2, 11.85) * mm});
            skLineSegment(sketch, "E2543", {"start": v(23.2, 11.85) * mm, "end": v(22.35, 12.7) * mm});
            skLineSegment(sketch, "E2544", {"start": v(22.35, 12.7) * mm, "end": v(22, 12.82) * mm});
            skLineSegment(sketch, "E2545", {"start": v(22, 12.82) * mm, "end": v(21.67, 12.87) * mm});
            skLineSegment(sketch, "E2546", {"start": v(-16.26, -8.47) * mm, "end": v(-15.92, -8.13) * mm});
            skLineSegment(sketch, "E2547", {"start": v(-8.13, -8.47) * mm, "end": v(-8.3, -5.25) * mm});
            skLineSegment(sketch, "E2548", {"start": v(3.05, -7.79) * mm, "end": v(2.88, -7.96) * mm});
            skLineSegment(sketch, "E2549", {"start": v(2.88, -7.96) * mm, "end": v(2.88, -8.13) * mm});
            skLineSegment(sketch, "E2550", {"start": v(2.88, -8.13) * mm, "end": v(3.22, -8.47) * mm});
            skLineSegment(sketch, "E2551", {"start": v(3.22, -8.47) * mm, "end": v(3.57, -8.33) * mm});
            skLineSegment(sketch, "E2552", {"start": v(3.57, -8.33) * mm, "end": v(3.9, -8.13) * mm});
            skLineSegment(sketch, "E2553", {"start": v(14.9, -8.47) * mm, "end": v(14.73, -8.47) * mm});
            skLineSegment(sketch, "E2554", {"start": v(14.9, -8.47) * mm, "end": v(14.9, -8.3) * mm});
            skLineSegment(sketch, "E2555", {"start": v(24.72, -8.47) * mm, "end": v(24.14, -1.87) * mm});
            skLineSegment(sketch, "E2556", {"start": v(24.14, -1.87) * mm, "end": v(24.05, -1.7) * mm});
            skLineSegment(sketch, "E2557", {"start": v(25.74, -8.47) * mm, "end": v(25.9, -8.47) * mm});
            skLineSegment(sketch, "E2558", {"start": v(25.9, -8.47) * mm, "end": v(25.9, -8.3) * mm});
            skLineSegment(sketch, "E2559", {"start": v(-16.26, -8.64) * mm, "end": v(-16.43, -8.64) * mm});
            skLineSegment(sketch, "E2560", {"start": v(-16.26, -8.64) * mm, "end": v(-16.26, -8.47) * mm});
            skLineSegment(sketch, "E2561", {"start": v(-8.13, -8.64) * mm, "end": v(-8.13, -8.47) * mm});
            skLineSegment(sketch, "E2562", {"start": v(-7.96, -8.64) * mm, "end": v(-8.13, -8.64) * mm});
            skLineSegment(sketch, "E2563", {"start": v(-7.45, -8.64) * mm, "end": v(-7.25, -7.98) * mm});
            skLineSegment(sketch, "E2564", {"start": v(-7.25, -7.98) * mm, "end": v(-6.7, -6.1) * mm});
            skLineSegment(sketch, "E2565", {"start": v(-6.7, -6.1) * mm, "end": v(-6.6, -5.08) * mm});
            skLineSegment(sketch, "E2566", {"start": v(4.4, -7.96) * mm, "end": v(4.91, -8.64) * mm});
            skLineSegment(sketch, "E2567", {"start": v(4.91, -8.64) * mm, "end": v(5.08, -8.64) * mm});
            skLineSegment(sketch, "E2568", {"start": v(5.08, -8.64) * mm, "end": v(5.59, -7.96) * mm});
            skLineSegment(sketch, "E2569", {"start": v(5.59, -7.96) * mm, "end": v(6.27, -7.96) * mm});
            skLineSegment(sketch, "E2570", {"start": v(6.27, -7.96) * mm, "end": v(6.64, -7.47) * mm});
            skLineSegment(sketch, "E2571", {"start": v(6.64, -7.47) * mm, "end": v(6.9, -6.76) * mm});
            skLineSegment(sketch, "E2572", {"start": v(6.9, -6.76) * mm, "end": v(7.79, -5.76) * mm});
            skLineSegment(sketch, "E2573", {"start": v(7.79, -5.76) * mm, "end": v(8.64, -5.59) * mm});
            skLineSegment(sketch, "E2574", {"start": v(11.85, -7.96) * mm, "end": v(11.85, -8.13) * mm});
            skLineSegment(sketch, "E2575", {"start": v(11.85, -8.13) * mm, "end": v(12.36, -8.64) * mm});
            skLineSegment(sketch, "E2576", {"start": v(12.36, -8.64) * mm, "end": v(14.56, -8.64) * mm});
            skLineSegment(sketch, "E2577", {"start": v(14.56, -8.64) * mm, "end": v(14.73, -8.47) * mm});
            skLineSegment(sketch, "E2578", {"start": v(24.9, -8.64) * mm, "end": v(24.72, -8.64) * mm});
            skLineSegment(sketch, "E2579", {"start": v(24.72, -8.64) * mm, "end": v(24.72, -8.47) * mm});
            skLineSegment(sketch, "E2580", {"start": v(24.9, -8.64) * mm, "end": v(25.74, -8.47) * mm});
            skLineSegment(sketch, "E2581", {"start": v(-18.46, -8.8) * mm, "end": v(-18.5, -8.65) * mm});
            skLineSegment(sketch, "E2582", {"start": v(-18.5, -8.65) * mm, "end": v(-19.13, -5.42) * mm});
            skLineSegment(sketch, "E2583", {"start": v(-19.13, -5.42) * mm, "end": v(-19.13, -3.9) * mm});
            skLineSegment(sketch, "E2584", {"start": v(-19.13, -3.9) * mm, "end": v(-18.76, -3.23) * mm});
            skLineSegment(sketch, "E2585", {"start": v(-18.76, -3.23) * mm, "end": v(-18.18, -2.02) * mm});
            skLineSegment(sketch, "E2586", {"start": v(-18.18, -2.02) * mm, "end": v(-18.12, -1.52) * mm});
            skLineSegment(sketch, "E2587", {"start": v(-8.47, -8.8) * mm, "end": v(-8.13, -8.64) * mm});
            skLineSegment(sketch, "E2588", {"start": v(-7.62, -8.8) * mm, "end": v(-7.96, -8.64) * mm});
            skLineSegment(sketch, "E2589", {"start": v(-7.45, -8.8) * mm, "end": v(-7.62, -8.8) * mm});
            skLineSegment(sketch, "E2590", {"start": v(-7.45, -8.8) * mm, "end": v(-7.45, -8.64) * mm});
            skLineSegment(sketch, "E2591", {"start": v(-7.28, -8.8) * mm, "end": v(-7.45, -8.8) * mm});
            skLineSegment(sketch, "E2592", {"start": v(-18.46, -8.97) * mm, "end": v(-18.63, -8.97) * mm});
            skLineSegment(sketch, "E2593", {"start": v(-18.46, -8.97) * mm, "end": v(-18.46, -8.8) * mm});
            skLineSegment(sketch, "E2594", {"start": v(-18.29, -8.97) * mm, "end": v(-18.46, -8.97) * mm});
            skLineSegment(sketch, "E2595", {"start": v(-18.29, -8.97) * mm, "end": v(-17.6, -8.7) * mm});
            skLineSegment(sketch, "E2596", {"start": v(-17.6, -8.7) * mm, "end": v(-16.43, -8.64) * mm});
            skLineSegment(sketch, "E2597", {"start": v(-7.28, -8.8) * mm, "end": v(-6.27, -8.97) * mm});
            skLineSegment(sketch, "E2598", {"start": v(-6.27, -8.97) * mm, "end": v(-5.1, -8.25) * mm});
            skLineSegment(sketch, "E2599", {"start": v(-5.1, -8.25) * mm, "end": v(-4.9, -8.16) * mm});
            skLineSegment(sketch, "E2600", {"start": v(-4.9, -8.16) * mm, "end": v(-4.4, -7.79) * mm});
            skLineSegment(sketch, "E2601", {"start": v(-4.4, -7.79) * mm, "end": v(-4.27, -7.26) * mm});
            skLineSegment(sketch, "E2602", {"start": v(-4.27, -7.26) * mm, "end": v(-4.23, -7.11) * mm});
            skLineSegment(sketch, "E2603", {"start": v(-4.23, -7.11) * mm, "end": v(-2.7, -6.43) * mm});
            skLineSegment(sketch, "E2604", {"start": v(-2.7, -6.43) * mm, "end": v(-2.03, -5.59) * mm});
            skLineSegment(sketch, "E2605", {"start": v(16.09, -8.97) * mm, "end": v(16.16, -7.46) * mm});
            skLineSegment(sketch, "E2606", {"start": v(16.16, -7.46) * mm, "end": v(16.76, -5.42) * mm});
            skLineSegment(sketch, "E2607", {"start": v(-15.4, -9.14) * mm, "end": v(-15.75, -8.3) * mm});
            skLineSegment(sketch, "E2608", {"start": v(-14.73, -9.14) * mm, "end": v(-14.78, -8.82) * mm});
            skLineSegment(sketch, "E2609", {"start": v(-14.78, -8.82) * mm, "end": v(-15.27, -7.47) * mm});
            skLineSegment(sketch, "E2610", {"start": v(-15.27, -7.47) * mm, "end": v(-15.4, -7.28) * mm});
            skLineSegment(sketch, "E2611", {"start": v(15.92, -9.14) * mm, "end": v(14.9, -8.47) * mm});
            skLineSegment(sketch, "E2612", {"start": v(16.09, -9.14) * mm, "end": v(15.92, -9.14) * mm});
            skLineSegment(sketch, "E2613", {"start": v(16.09, -9.14) * mm, "end": v(16.09, -8.97) * mm});
            skLineSegment(sketch, "E2614", {"start": v(-15.58, -9.31) * mm, "end": v(-16.26, -8.64) * mm});
            skLineSegment(sketch, "E2615", {"start": v(-15.4, -9.31) * mm, "end": v(-15.58, -9.31) * mm});
            skLineSegment(sketch, "E2616", {"start": v(-15.4, -9.31) * mm, "end": v(-15.4, -9.14) * mm});
            skLineSegment(sketch, "E2617", {"start": v(-15.24, -9.31) * mm, "end": v(-15.4, -9.31) * mm});
            skLineSegment(sketch, "E2618", {"start": v(-14.73, -9.31) * mm, "end": v(-14.9, -9.31) * mm});
            skLineSegment(sketch, "E2619", {"start": v(-14.73, -9.31) * mm, "end": v(-14.73, -9.14) * mm});
            skLineSegment(sketch, "E2620", {"start": v(-14.56, -9.31) * mm, "end": v(-14.73, -9.31) * mm});
            skLineSegment(sketch, "E2621", {"start": v(-13.89, -9.31) * mm, "end": v(-13.99, -9.13) * mm});
            skLineSegment(sketch, "E2622", {"start": v(-13.99, -9.13) * mm, "end": v(-14.63, -6.47) * mm});
            skLineSegment(sketch, "E2623", {"start": v(-14.63, -6.47) * mm, "end": v(-14.9, -6.1) * mm});
            skLineSegment(sketch, "E2624", {"start": v(16.09, -9.31) * mm, "end": v(16.09, -9.14) * mm});
            skLineSegment(sketch, "E2625", {"start": v(20.32, -9.31) * mm, "end": v(20.18, -8.96) * mm});
            skLineSegment(sketch, "E2626", {"start": v(20.18, -8.96) * mm, "end": v(19.47, -8.13) * mm});
            skLineSegment(sketch, "E2627", {"start": v(19.47, -8.13) * mm, "end": v(18.46, -7.28) * mm});
            skLineSegment(sketch, "E2628", {"start": v(-15.24, -9.31) * mm, "end": v(-15.07, -9.48) * mm});
            skLineSegment(sketch, "E2629", {"start": v(-15.07, -9.48) * mm, "end": v(-14.9, -9.31) * mm});
            skLineSegment(sketch, "E2630", {"start": v(-14.05, -9.48) * mm, "end": v(-14.4, -9.48) * mm});
            skLineSegment(sketch, "E2631", {"start": v(-14.4, -9.48) * mm, "end": v(-14.56, -9.31) * mm});
            skLineSegment(sketch, "E2632", {"start": v(-13.89, -9.48) * mm, "end": v(-14.05, -9.48) * mm});
            skLineSegment(sketch, "E2633", {"start": v(-13.89, -9.48) * mm, "end": v(-13.89, -9.31) * mm});
            skLineSegment(sketch, "E2634", {"start": v(-13.38, -9.48) * mm, "end": v(-13.2, -9.31) * mm});
            skLineSegment(sketch, "E2635", {"start": v(-13.2, -9.31) * mm, "end": v(-13.3, -8.63) * mm});
            skLineSegment(sketch, "E2636", {"start": v(-13.3, -8.63) * mm, "end": v(-13.45, -7.46) * mm});
            skLineSegment(sketch, "E2637", {"start": v(-13.45, -7.46) * mm, "end": v(-14.02, -5.57) * mm});
            skLineSegment(sketch, "E2638", {"start": v(-14.02, -5.57) * mm, "end": v(-14.56, -4.74) * mm});
            skLineSegment(sketch, "E2639", {"start": v(-9.82, -9.31) * mm, "end": v(-9.65, -9.4) * mm});
            skLineSegment(sketch, "E2640", {"start": v(-9.65, -9.4) * mm, "end": v(-8.65, -8.94) * mm});
            skLineSegment(sketch, "E2641", {"start": v(-8.65, -8.94) * mm, "end": v(-8.47, -8.8) * mm});
            skLineSegment(sketch, "E2642", {"start": v(-7.96, -9.31) * mm, "end": v(-7.79, -9.48) * mm});
            skLineSegment(sketch, "E2643", {"start": v(-7.79, -9.48) * mm, "end": v(-7.43, -9.36) * mm});
            skLineSegment(sketch, "E2644", {"start": v(-7.43, -9.36) * mm, "end": v(-7.11, -9.31) * mm});
            skLineSegment(sketch, "E2645", {"start": v(16.43, -9.48) * mm, "end": v(16.66, -7.63) * mm});
            skLineSegment(sketch, "E2646", {"start": v(16.66, -7.63) * mm, "end": v(17.14, -6.11) * mm});
            skLineSegment(sketch, "E2647", {"start": v(17.14, -6.11) * mm, "end": v(17.44, -5.59) * mm});
            skLineSegment(sketch, "E2648", {"start": v(20.32, -9.48) * mm, "end": v(20.15, -9.48) * mm});
            skLineSegment(sketch, "E2649", {"start": v(20.32, -9.48) * mm, "end": v(20.32, -9.31) * mm});
            skLineSegment(sketch, "E2650", {"start": v(-13.55, -9.65) * mm, "end": v(-13.89, -9.48) * mm});
            skLineSegment(sketch, "E2651", {"start": v(-13.38, -9.65) * mm, "end": v(-13.55, -9.65) * mm});
            skLineSegment(sketch, "E2652", {"start": v(-13.38, -9.65) * mm, "end": v(-13.38, -9.48) * mm});
            skLineSegment(sketch, "E2653", {"start": v(16.26, -9.65) * mm, "end": v(16.09, -9.31) * mm});
            skLineSegment(sketch, "E2654", {"start": v(16.43, -9.65) * mm, "end": v(16.26, -9.65) * mm});
            skLineSegment(sketch, "E2655", {"start": v(16.43, -9.65) * mm, "end": v(16.43, -9.48) * mm});
            skLineSegment(sketch, "E2656", {"start": v(17.1, -9.65) * mm, "end": v(17.17, -8.65) * mm});
            skLineSegment(sketch, "E2657", {"start": v(17.17, -8.65) * mm, "end": v(17.82, -6.97) * mm});
            skLineSegment(sketch, "E2658", {"start": v(17.82, -6.97) * mm, "end": v(18.12, -6.6) * mm});
            skLineSegment(sketch, "E2659", {"start": v(17.44, -9.65) * mm, "end": v(18.32, -7.47) * mm});
            skLineSegment(sketch, "E2660", {"start": v(18.32, -7.47) * mm, "end": v(18.46, -7.28) * mm});
            skLineSegment(sketch, "E2661", {"start": v(16.43, -9.82) * mm, "end": v(16.43, -9.65) * mm});
            skLineSegment(sketch, "E2662", {"start": v(17.1, -9.82) * mm, "end": v(16.93, -9.82) * mm});
            skLineSegment(sketch, "E2663", {"start": v(17.1, -9.82) * mm, "end": v(17.1, -9.65) * mm});
            skLineSegment(sketch, "E2664", {"start": v(17.27, -9.82) * mm, "end": v(17.1, -9.82) * mm});
            skLineSegment(sketch, "E2665", {"start": v(17.44, -9.82) * mm, "end": v(17.27, -9.82) * mm});
            skLineSegment(sketch, "E2666", {"start": v(17.44, -9.82) * mm, "end": v(17.44, -9.65) * mm});
            skLineSegment(sketch, "E2667", {"start": v(17.61, -9.82) * mm, "end": v(17.44, -9.82) * mm});
            skLineSegment(sketch, "E2668", {"start": v(16.6, -10) * mm, "end": v(16.43, -9.82) * mm});
            skLineSegment(sketch, "E2669", {"start": v(16.6, -10) * mm, "end": v(16.93, -9.82) * mm});
            skLineSegment(sketch, "E2670", {"start": v(19.13, -10) * mm, "end": v(20.15, -9.48) * mm});
            skLineSegment(sketch, "E2671", {"start": v(17.61, -9.82) * mm, "end": v(18.97, -10.16) * mm});
            skLineSegment(sketch, "E2672", {"start": v(18.97, -10.16) * mm, "end": v(19.13, -10) * mm});
            skLineSegment(sketch, "E2673", {"start": v(22.7, -10.33) * mm, "end": v(22.86, 0.34) * mm});
            skLineSegment(sketch, "E2674", {"start": v(24.05, -10.33) * mm, "end": v(23.88, -1.86) * mm});
            skLineSegment(sketch, "E2675", {"start": v(23.88, -1.86) * mm, "end": v(24.05, -1.7) * mm});
            skLineSegment(sketch, "E2676", {"start": v(22.7, -10.5) * mm, "end": v(22.7, -10.33) * mm});
            skLineSegment(sketch, "E2677", {"start": v(22.86, -10.5) * mm, "end": v(22.7, -10.5) * mm});
            skLineSegment(sketch, "E2678", {"start": v(23.88, -10.5) * mm, "end": v(22.86, -10.5) * mm});
            skLineSegment(sketch, "E2679", {"start": v(24.05, -10.5) * mm, "end": v(23.88, -10.5) * mm});
            skLineSegment(sketch, "E2680", {"start": v(24.05, -10.5) * mm, "end": v(24.05, -10.33) * mm});
            skLineSegment(sketch, "E2681", {"start": v(-12.02, -10.67) * mm, "end": v(-13.38, -9.65) * mm});
            skLineSegment(sketch, "E2682", {"start": v(-11.85, -10.67) * mm, "end": v(-12.02, -10.67) * mm});
            skLineSegment(sketch, "E2683", {"start": v(-11.68, -10.67) * mm, "end": v(-11.85, -10.67) * mm});
            skLineSegment(sketch, "E2684", {"start": v(-11.68, -10.67) * mm, "end": v(-11.16, -10.55) * mm});
            skLineSegment(sketch, "E2685", {"start": v(-11.16, -10.55) * mm, "end": v(-10.84, -10.5) * mm});
            skLineSegment(sketch, "E2686", {"start": v(-10.84, -10.5) * mm, "end": v(-10.5, -10.16) * mm});
            skLineSegment(sketch, "E2687", {"start": v(-10.5, -10.16) * mm, "end": v(-10.5, -9.82) * mm});
            skLineSegment(sketch, "E2688", {"start": v(-10.5, -9.82) * mm, "end": v(-10.67, -9.65) * mm});
            skLineSegment(sketch, "E2689", {"start": v(-10.67, -9.65) * mm, "end": v(-10.67, -9.31) * mm});
            skLineSegment(sketch, "E2690", {"start": v(-10.67, -9.31) * mm, "end": v(-10.36, -9.1) * mm});
            skLineSegment(sketch, "E2691", {"start": v(-10.36, -9.1) * mm, "end": v(-9.65, -8.64) * mm});
            skLineSegment(sketch, "E2692", {"start": v(-9.65, -8.64) * mm, "end": v(-8.64, -8.64) * mm});
            skLineSegment(sketch, "E2693", {"start": v(-8.64, -8.64) * mm, "end": v(-8.47, -8.8) * mm});
            skLineSegment(sketch, "E2694", {"start": v(22.7, -10.67) * mm, "end": v(22.7, -10.5) * mm});
            skLineSegment(sketch, "E2695", {"start": v(24.05, -10.67) * mm, "end": v(24.05, -10.5) * mm});
            skLineSegment(sketch, "E2696", {"start": v(-11.85, -10.84) * mm, "end": v(-11.85, -10.67) * mm});
            skLineSegment(sketch, "E2697", {"start": v(20.66, -10.84) * mm, "end": v(20.32, -9.48) * mm});
            skLineSegment(sketch, "E2698", {"start": v(22.7, -10.84) * mm, "end": v(22.7, -10.67) * mm});
            skLineSegment(sketch, "E2699", {"start": v(24.21, -10.84) * mm, "end": v(24.05, -10.67) * mm});
            skLineSegment(sketch, "E2700", {"start": v(-11.85, -11) * mm, "end": v(-11.85, -10.84) * mm});
            skLineSegment(sketch, "E2701", {"start": v(-11.68, -11) * mm, "end": v(-11.85, -11) * mm});
            skLineSegment(sketch, "E2702", {"start": v(-11.68, -11) * mm, "end": v(-8.64, -10.93) * mm});
            skLineSegment(sketch, "E2703", {"start": v(-8.64, -10.93) * mm, "end": v(-5.26, -10.6) * mm});
            skLineSegment(sketch, "E2704", {"start": v(-5.26, -10.6) * mm, "end": v(-4.74, -10.33) * mm});
            skLineSegment(sketch, "E2705", {"start": v(-4.74, -10.33) * mm, "end": v(-4.34, -8.65) * mm});
            skLineSegment(sketch, "E2706", {"start": v(-4.34, -8.65) * mm, "end": v(-4.06, -8.13) * mm});
            skLineSegment(sketch, "E2707", {"start": v(-4.06, -8.13) * mm, "end": v(-3.92, -8.09) * mm});
            skLineSegment(sketch, "E2708", {"start": v(-3.92, -8.09) * mm, "end": v(-0.88, -6.87) * mm});
            skLineSegment(sketch, "E2709", {"start": v(-0.88, -6.87) * mm, "end": v(-0.5, -7.11) * mm});
            skLineSegment(sketch, "E2710", {"start": v(20.32, -11) * mm, "end": v(19.13, -10) * mm});
            skLineSegment(sketch, "E2711", {"start": v(20.49, -11) * mm, "end": v(20.32, -11) * mm});
            skLineSegment(sketch, "E2712", {"start": v(20.49, -11) * mm, "end": v(20.66, -10.84) * mm});
            skLineSegment(sketch, "E2713", {"start": v(22.7, -11) * mm, "end": v(22.7, -10.84) * mm});
            skLineSegment(sketch, "E2714", {"start": v(22.86, -11) * mm, "end": v(22.7, -11) * mm});
            skLineSegment(sketch, "E2715", {"start": v(24.05, -11) * mm, "end": v(22.86, -11) * mm});
            skLineSegment(sketch, "E2716", {"start": v(24.21, -11) * mm, "end": v(24.05, -11) * mm});
            skLineSegment(sketch, "E2717", {"start": v(24.21, -11) * mm, "end": v(24.21, -10.84) * mm});
            skLineSegment(sketch, "E2718", {"start": v(20.49, -11.18) * mm, "end": v(20.49, -11) * mm});
            skLineSegment(sketch, "E2719", {"start": v(20.83, -11.18) * mm, "end": v(20.66, -10.84) * mm});
            skLineSegment(sketch, "E2720", {"start": v(22.7, -11.18) * mm, "end": v(22.7, -11) * mm});
            skLineSegment(sketch, "E2721", {"start": v(24.21, -11.18) * mm, "end": v(24.21, -11) * mm});
            skLineSegment(sketch, "E2722", {"start": v(-18.29, -8.97) * mm, "end": v(-17.75, -9.44) * mm});
            skLineSegment(sketch, "E2723", {"start": v(-17.75, -9.44) * mm, "end": v(-16.92, -9.75) * mm});
            skLineSegment(sketch, "E2724", {"start": v(-16.92, -9.75) * mm, "end": v(-15.82, -10.01) * mm});
            skLineSegment(sketch, "E2725", {"start": v(-15.82, -10.01) * mm, "end": v(-14.34, -10.85) * mm});
            skLineSegment(sketch, "E2726", {"start": v(-14.34, -10.85) * mm, "end": v(-12.2, -11.35) * mm});
            skLineSegment(sketch, "E2727", {"start": v(-12.2, -11.35) * mm, "end": v(-11.85, -11) * mm});
            skLineSegment(sketch, "E2728", {"start": v(20.66, -11.35) * mm, "end": v(20.49, -11.18) * mm});
            skLineSegment(sketch, "E2729", {"start": v(20.83, -11.35) * mm, "end": v(20.66, -11.35) * mm});
            skLineSegment(sketch, "E2730", {"start": v(20.83, -11.35) * mm, "end": v(20.83, -11.18) * mm});
            skLineSegment(sketch, "E2731", {"start": v(22.7, -11.35) * mm, "end": v(22.7, -11.18) * mm});
            skLineSegment(sketch, "E2732", {"start": v(24.21, -11.35) * mm, "end": v(24.05, -11.35) * mm});
            skLineSegment(sketch, "E2733", {"start": v(24.21, -11.35) * mm, "end": v(24.21, -11.18) * mm});
            skLineSegment(sketch, "E2734", {"start": v(16.6, -10) * mm, "end": v(16.6, -10.33) * mm});
            skLineSegment(sketch, "E2735", {"start": v(16.6, -10.33) * mm, "end": v(17.1, -10.84) * mm});
            skLineSegment(sketch, "E2736", {"start": v(17.1, -10.84) * mm, "end": v(19.98, -11.51) * mm});
            skLineSegment(sketch, "E2737", {"start": v(19.98, -11.51) * mm, "end": v(20.49, -11.51) * mm});
            skLineSegment(sketch, "E2738", {"start": v(20.49, -11.51) * mm, "end": v(20.66, -11.35) * mm});
            skLineSegment(sketch, "E2739", {"start": v(22.7, -11.51) * mm, "end": v(22.7, -11.35) * mm});
            skLineSegment(sketch, "E2740", {"start": v(22.86, -11.51) * mm, "end": v(22.7, -11.51) * mm});
            skLineSegment(sketch, "E2741", {"start": v(22.86, -11.51) * mm, "end": v(23.88, -11.51) * mm});
            skLineSegment(sketch, "E2742", {"start": v(23.88, -11.51) * mm, "end": v(24.05, -11.35) * mm});
            skLineSegment(sketch, "E2743", {"start": v(24.21, -11.51) * mm, "end": v(24.21, -11.35) * mm});
            skLineSegment(sketch, "E2744", {"start": v(21.84, -11.68) * mm, "end": v(21.81, -11.53) * mm});
            skLineSegment(sketch, "E2745", {"start": v(21.81, -11.53) * mm, "end": v(21.41, -10.66) * mm});
            skLineSegment(sketch, "E2746", {"start": v(21.41, -10.66) * mm, "end": v(21.26, -8.3) * mm});
            skLineSegment(sketch, "E2747", {"start": v(21.26, -8.3) * mm, "end": v(20.66, -7.28) * mm});
            skLineSegment(sketch, "E2748", {"start": v(20.66, -7.28) * mm, "end": v(20.66, -6.43) * mm});
            skLineSegment(sketch, "E2749", {"start": v(20.66, -6.43) * mm, "end": v(21.2, -5.1) * mm});
            skLineSegment(sketch, "E2750", {"start": v(21.2, -5.1) * mm, "end": v(21.34, -4.91) * mm});
            skLineSegment(sketch, "E2751", {"start": v(22.7, -11.68) * mm, "end": v(22.7, -11.51) * mm});
            skLineSegment(sketch, "E2752", {"start": v(-25.57, -1.52) * mm, "end": v(-25.79, -2.02) * mm});
            skLineSegment(sketch, "E2753", {"start": v(-25.79, -2.02) * mm, "end": v(-25.9, -2.2) * mm});
            skLineSegment(sketch, "E2754", {"start": v(-25.9, -2.2) * mm, "end": v(-25.74, -4.57) * mm});
            skLineSegment(sketch, "E2755", {"start": v(-25.74, -4.57) * mm, "end": v(-25.9, -4.74) * mm});
            skLineSegment(sketch, "E2756", {"start": v(-25.9, -4.74) * mm, "end": v(-25.9, -11.85) * mm});
            skLineSegment(sketch, "E2757", {"start": v(-25.9, -11.85) * mm, "end": v(-25.74, -12.02) * mm});
            skLineSegment(sketch, "E2758", {"start": v(-25.74, -12.02) * mm, "end": v(-25.09, -11.48) * mm});
            skLineSegment(sketch, "E2759", {"start": v(-25.09, -11.48) * mm, "end": v(-24.55, -11.18) * mm});
            skLineSegment(sketch, "E2760", {"start": v(-24.55, -11.18) * mm, "end": v(-24, -9.85) * mm});
            skLineSegment(sketch, "E2761", {"start": v(-24, -9.85) * mm, "end": v(-23.03, -8.64) * mm});
            skLineSegment(sketch, "E2762", {"start": v(-23.03, -8.64) * mm, "end": v(-19.47, -8.97) * mm});
            skLineSegment(sketch, "E2763", {"start": v(-19.47, -8.97) * mm, "end": v(-19.3, -8.8) * mm});
            skLineSegment(sketch, "E2764", {"start": v(-19.3, -8.8) * mm, "end": v(-18.78, -8.94) * mm});
            skLineSegment(sketch, "E2765", {"start": v(-18.78, -8.94) * mm, "end": v(-18.63, -8.97) * mm});
            skLineSegment(sketch, "E2766", {"start": v(21.34, -12.02) * mm, "end": v(20.83, -11.35) * mm});
            skLineSegment(sketch, "E2767", {"start": v(21.5, -12.02) * mm, "end": v(21.34, -12.02) * mm});
            skLineSegment(sketch, "E2768", {"start": v(21.5, -12.02) * mm, "end": v(21.84, -11.68) * mm});
            skLineSegment(sketch, "E2769", {"start": v(21.5, -12.2) * mm, "end": v(21.5, -12.02) * mm});
            skLineSegment(sketch, "E2770", {"start": v(22.01, -12.36) * mm, "end": v(22.18, -12.2) * mm});
            skLineSegment(sketch, "E2771", {"start": v(22.18, -12.2) * mm, "end": v(22.18, -12.02) * mm});
            skLineSegment(sketch, "E2772", {"start": v(22.18, -12.02) * mm, "end": v(21.84, -11.68) * mm});
            skLineSegment(sketch, "E2773", {"start": v(21.84, -12.53) * mm, "end": v(21.5, -12.2) * mm});
            skLineSegment(sketch, "E2774", {"start": v(22.01, -12.53) * mm, "end": v(21.84, -12.53) * mm});
            skLineSegment(sketch, "E2775", {"start": v(22.01, -12.53) * mm, "end": v(22.01, -12.36) * mm});
            skLineSegment(sketch, "E2776", {"start": v(22.86, -12.7) * mm, "end": v(22.7, -11.68) * mm});
            skLineSegment(sketch, "E2777", {"start": v(22.86, -12.87) * mm, "end": v(22.7, -12.87) * mm});
            skLineSegment(sketch, "E2778", {"start": v(22.86, -12.87) * mm, "end": v(22.86, -12.7) * mm});
            skLineSegment(sketch, "E2779", {"start": v(22.01, -12.53) * mm, "end": v(22.52, -13.04) * mm});
            skLineSegment(sketch, "E2780", {"start": v(22.52, -13.04) * mm, "end": v(22.7, -12.87) * mm});
            skLineSegment(sketch, "E2781", {"start": v(22.86, -12.87) * mm, "end": v(23.03, -13.04) * mm});
            skLineSegment(sketch, "E2782", {"start": v(23.03, -13.04) * mm, "end": v(23.7, -13.04) * mm});
            skLineSegment(sketch, "E2783", {"start": v(23.7, -13.04) * mm, "end": v(24.38, -12.7) * mm});
            skLineSegment(sketch, "E2784", {"start": v(24.38, -12.7) * mm, "end": v(24.21, -11.51) * mm});
            skSolve(sketch);
        }
        {
            var Q0;
            Q0=qCreatedBy(makeId("Front.planeOp"),FACE);
            var sketch = newSketch(context, id + "F1", { "sketchPlane" : qUnion([Q0])});
            skLineSegment(sketch, "E2785.bottom", {"start": v(-27.63, -13.85) * mm, "end": v(27.08, -13.85) * mm});
            skLineSegment(sketch, "E2785.top", {"start": v(-27.63, 15.68) * mm, "end": v(27.08, 15.68) * mm});
            skLineSegment(sketch, "E2785.left", {"start": v(-27.63, -13.85) * mm, "end": v(-27.63, 15.68) * mm});
            skLineSegment(sketch, "E2785.right", {"start": v(27.08, -13.85) * mm, "end": v(27.08, 15.68) * mm});
            skSolve(sketch);
        }
        {
            var Q0;
            Q0 = qSketchRegion(id + "F1", true);
            extrude(context, id + "F2", {"entities" : qUnion([Q0]), "oppositeDirection" : true, "depth" : 6.35 * mm});
        }
        {
            var Q0;
            Q0=makeQuery(id+"F0.imprint","IMPRINT",FACE,{"disambiguationData":[TD([[makeQuery(id+"F0.imprint","IMPRINT",EDGE,{"derivedFrom":sQuery(id+"F0.wireOp",EDGE,"E36")}),1.0]])]});
            var Q1;
            Q1=makeQuery(id+"F0.imprint","IMPRINT",FACE,{"disambiguationData":[TD([[makeQuery(id+"F0.imprint","IMPRINT",EDGE,{"derivedFrom":sQuery(id+"F0.wireOp",EDGE,"E1234")}),1.0]])]});
            var Q2;
            Q2=makeQuery(id+"F0.imprint","IMPRINT",FACE,{"disambiguationData":[TD([[makeQuery(id+"F0.imprint","IMPRINT",EDGE,{"derivedFrom":sQuery(id+"F0.wireOp",EDGE,"E2063")}),1.0]])]});
            var Q3;
            Q3=makeQuery(id+"F0.imprint","IMPRINT",FACE,{"disambiguationData":[TD([[makeQuery(id+"F0.imprint","IMPRINT",EDGE,{"derivedFrom":sQuery(id+"F0.wireOp",EDGE,"E1109")}),1.0]])]});
            var Q4;
            Q4=makeQuery(id+"F0.imprint","IMPRINT",FACE,{"disambiguationData":[TD([[makeQuery(id+"F0.imprint","IMPRINT",EDGE,{"derivedFrom":sQuery(id+"F0.wireOp",EDGE,"E1936")}),-1.0]])]});
            var Q5;
            Q5=makeQuery(id+"F0.imprint","IMPRINT",FACE,{"disambiguationData":[TD([[makeQuery(id+"F0.imprint","IMPRINT",EDGE,{"derivedFrom":sQuery(id+"F0.wireOp",EDGE,"E582")}),1.0]])]});
            var Q6;
            Q6=makeQuery(id+"F0.imprint","IMPRINT",FACE,{"disambiguationData":[TD([[makeQuery(id+"F0.imprint","IMPRINT",EDGE,{"derivedFrom":sQuery(id+"F0.wireOp",EDGE,"E681")}),1.0]])]});
            var Q7;
            Q7=makeQuery(id+"F0.imprint","IMPRINT",FACE,{"disambiguationData":[TD([[makeQuery(id+"F0.imprint","IMPRINT",EDGE,{"derivedFrom":sQuery(id+"F0.wireOp",EDGE,"E203")}),1.0]])]});
            var Q8;
            Q8=makeQuery(id+"F0.imprint","IMPRINT",FACE,{"disambiguationData":[TD([[makeQuery(id+"F0.imprint","IMPRINT",EDGE,{"derivedFrom":sQuery(id+"F0.wireOp",EDGE,"E1732")}),-1.0]])]});
            var Q9;
            Q9=makeQuery(id+"F0.imprint","IMPRINT",FACE,{"disambiguationData":[TD([[makeQuery(id+"F0.imprint","IMPRINT",EDGE,{"derivedFrom":sQuery(id+"F0.wireOp",EDGE,"E1635")}),-1.0]])]});
            var Q10;
            Q10=makeQuery(id+"F0.imprint","IMPRINT",FACE,{"disambiguationData":[TD([[makeQuery(id+"F0.imprint","IMPRINT",EDGE,{"derivedFrom":sQuery(id+"F0.wireOp",EDGE,"E546")}),-1.0]])]});
            var Q11;
            Q11=makeQuery(id+"F0.imprint","IMPRINT",FACE,{"disambiguationData":[TD([[makeQuery(id+"F0.imprint","IMPRINT",EDGE,{"derivedFrom":sQuery(id+"F0.wireOp",EDGE,"E442")}),1.0]])]});
            var Q12;
            Q12=makeQuery(id+"F0.imprint","IMPRINT",FACE,{"disambiguationData":[TD([[makeQuery(id+"F0.imprint","IMPRINT",EDGE,{"derivedFrom":sQuery(id+"F0.wireOp",EDGE,"E173")}),1.0]])]});
            var Q13;
            Q13=makeQuery(id+"F0.imprint","IMPRINT",FACE,{"disambiguationData":[TD([[makeQuery(id+"F0.imprint","IMPRINT",EDGE,{"derivedFrom":sQuery(id+"F0.wireOp",EDGE,"E373")}),1.0]])]});
            var Q14;
            Q14=makeQuery(id+"F0.imprint","IMPRINT",FACE,{"disambiguationData":[TD([[makeQuery(id+"F0.imprint","IMPRINT",EDGE,{"derivedFrom":sQuery(id+"F0.wireOp",EDGE,"E1504")}),1.0]])]});
            var Q15;
            Q15=makeQuery(id+"F2.opExtrude","CAP_FACE",FACE,{"disambiguationData":[OSD([sQuery(id+"F1.wireOp",EDGE,"E2785.bottom"),sQuery(id+"F1.wireOp",EDGE,"E2785.top"),sQuery(id+"F1.wireOp",EDGE,"E2785.left"),sQuery(id+"F1.wireOp",EDGE,"E2785.right")])],"isStart":true});
            var Q16;
            Q16=makeQuery(id+"F2.opExtrude","CAP_FACE",FACE,{"disambiguationData":[OSD([sQuery(id+"F1.wireOp",EDGE,"E2785.bottom"),sQuery(id+"F1.wireOp",EDGE,"E2785.top"),sQuery(id+"F1.wireOp",EDGE,"E2785.left"),sQuery(id+"F1.wireOp",EDGE,"E2785.right")])],"isStart":false});
            var Q17;
            Q17=makeQuery(id+"F0.imprint","IMPRINT",FACE,{"disambiguationData":[TD([[makeQuery(id+"F0.imprint","IMPRINT",EDGE,{"derivedFrom":sQuery(id+"F0.wireOp",EDGE,"E1505")}),1.0]])]});
            var Q18;
            Q18=makeQuery(id+"F0.imprint","IMPRINT",FACE,{"disambiguationData":[TD([[makeQuery(id+"F0.imprint","IMPRINT",EDGE,{"derivedFrom":sQuery(id+"F0.wireOp",EDGE,"E1373")}),1.0]])]});
            var Q19;
            Q19=makeQuery(id+"F0.imprint","IMPRINT",FACE,{"disambiguationData":[TD([[makeQuery(id+"F0.imprint","IMPRINT",EDGE,{"derivedFrom":sQuery(id+"F0.wireOp",EDGE,"E1325")}),1.0]])]});
            var Q20;
            Q20=makeQuery(id+"F0.imprint","IMPRINT",FACE,{"disambiguationData":[TD([[makeQuery(id+"F0.imprint","IMPRINT",EDGE,{"derivedFrom":sQuery(id+"F0.wireOp",EDGE,"E1221")}),1.0]])]});
            var Q21;
            Q21=makeQuery(id+"F0.imprint","IMPRINT",FACE,{"disambiguationData":[TD([[makeQuery(id+"F0.imprint","IMPRINT",EDGE,{"derivedFrom":sQuery(id+"F0.wireOp",EDGE,"E1198")}),1.0]])]});
            var Q22;
            Q22=makeQuery(id+"F0.imprint","IMPRINT",FACE,{"disambiguationData":[TD([[makeQuery(id+"F0.imprint","IMPRINT",EDGE,{"derivedFrom":sQuery(id+"F0.wireOp",EDGE,"E1613")}),1.0]])]});
            var Q23;
            Q23=makeQuery(id+"F0.imprint","IMPRINT",FACE,{"disambiguationData":[TD([[makeQuery(id+"F0.imprint","IMPRINT",EDGE,{"derivedFrom":sQuery(id+"F0.wireOp",EDGE,"E1468")}),-1.0]])]});
            var Q24;
            Q24=makeQuery(id+"F0.imprint","IMPRINT",FACE,{"disambiguationData":[TD([[makeQuery(id+"F0.imprint","IMPRINT",EDGE,{"derivedFrom":sQuery(id+"F0.wireOp",EDGE,"E1396")}),-1.0]])]});
            var Q25;
            Q25=makeQuery(id+"F0.imprint","IMPRINT",FACE,{"disambiguationData":[TD([[makeQuery(id+"F0.imprint","IMPRINT",EDGE,{"derivedFrom":sQuery(id+"F0.wireOp",EDGE,"E1322")}),-1.0]])]});
            var Q26;
            Q26=makeQuery(id+"F0.imprint","IMPRINT",FACE,{"disambiguationData":[TD([[makeQuery(id+"F0.imprint","IMPRINT",EDGE,{"derivedFrom":sQuery(id+"F0.wireOp",EDGE,"E1888")}),-1.0]])]});
            var Q27;
            Q27=makeQuery(id+"F0.imprint","IMPRINT",FACE,{"disambiguationData":[TD([[makeQuery(id+"F0.imprint","IMPRINT",EDGE,{"derivedFrom":sQuery(id+"F0.wireOp",EDGE,"E1093")}),1.0]])]});
            var Q28;
            Q28=makeQuery(id+"F0.imprint","IMPRINT",FACE,{"disambiguationData":[TD([[makeQuery(id+"F0.imprint","IMPRINT",EDGE,{"derivedFrom":sQuery(id+"F0.wireOp",EDGE,"E1979")}),1.0]])]});
            var Q29;
            Q29=makeQuery(id+"F0.imprint","IMPRINT",FACE,{"disambiguationData":[TD([[makeQuery(id+"F0.imprint","IMPRINT",EDGE,{"derivedFrom":sQuery(id+"F0.wireOp",EDGE,"E2282")}),1.0]])]});
            var Q30;
            Q30=makeQuery(id+"F0.imprint","IMPRINT",FACE,{"disambiguationData":[TD([[makeQuery(id+"F0.imprint","IMPRINT",EDGE,{"derivedFrom":sQuery(id+"F0.wireOp",EDGE,"E2311")}),1.0]])]});
            var Q31;
            Q31=makeQuery(id+"F0.imprint","IMPRINT",FACE,{"disambiguationData":[TD([[makeQuery(id+"F0.imprint","IMPRINT",EDGE,{"derivedFrom":sQuery(id+"F0.wireOp",EDGE,"E825")}),1.0]])]});
            var Q32;
            Q32=makeQuery(id+"F0.imprint","IMPRINT",FACE,{"disambiguationData":[TD([[makeQuery(id+"F0.imprint","IMPRINT",EDGE,{"derivedFrom":sQuery(id+"F0.wireOp",EDGE,"E958")}),1.0]])]});
            var Q33;
            Q33=makeQuery(id+"F0.imprint","IMPRINT",FACE,{"disambiguationData":[TD([[makeQuery(id+"F0.imprint","IMPRINT",EDGE,{"derivedFrom":sQuery(id+"F0.wireOp",EDGE,"E826")}),1.0]])]});
            var Q34;
            Q34=makeQuery(id+"F0.imprint","IMPRINT",FACE,{"disambiguationData":[TD([[makeQuery(id+"F0.imprint","IMPRINT",EDGE,{"derivedFrom":sQuery(id+"F0.wireOp",EDGE,"E722")}),1.0]])]});
            var Q35;
            Q35=makeQuery(id+"F0.imprint","IMPRINT",FACE,{"disambiguationData":[TD([[makeQuery(id+"F0.imprint","IMPRINT",EDGE,{"derivedFrom":sQuery(id+"F0.wireOp",EDGE,"E517")}),-1.0]])]});
            var Q36;
            Q36=makeQuery(id+"F0.imprint","IMPRINT",FACE,{"disambiguationData":[TD([[makeQuery(id+"F0.imprint","IMPRINT",EDGE,{"derivedFrom":sQuery(id+"F0.wireOp",EDGE,"E468")}),-1.0]])]});
            var Q37;
            Q37=makeQuery(id+"F0.imprint","IMPRINT",FACE,{"disambiguationData":[TD([[makeQuery(id+"F0.imprint","IMPRINT",EDGE,{"derivedFrom":sQuery(id+"F0.wireOp",EDGE,"E553")}),1.0]])]});
            var Q38;
            Q38=makeQuery(id+"F0.imprint","IMPRINT",FACE,{"disambiguationData":[TD([[makeQuery(id+"F0.imprint","IMPRINT",EDGE,{"derivedFrom":sQuery(id+"F0.wireOp",EDGE,"E106")}),-1.0]])]});
            var Q39;
            Q39=makeQuery(id+"F0.imprint","IMPRINT",FACE,{"disambiguationData":[TD([[makeQuery(id+"F0.imprint","IMPRINT",EDGE,{"derivedFrom":sQuery(id+"F0.wireOp",EDGE,"E1602")}),1.0]])]});
            var Q40;
            Q40=makeQuery(id+"F0.imprint","IMPRINT",FACE,{"disambiguationData":[TD([[makeQuery(id+"F0.imprint","IMPRINT",EDGE,{"derivedFrom":sQuery(id+"F0.wireOp",EDGE,"E1572")}),-1.0]])]});
            var Q41;
            Q41=makeQuery(id+"F0.imprint","IMPRINT",FACE,{"disambiguationData":[TD([[makeQuery(id+"F0.imprint","IMPRINT",EDGE,{"derivedFrom":sQuery(id+"F0.wireOp",EDGE,"E1607")}),-1.0]])]});
            var Q42;
            Q42=makeQuery(id+"F0.imprint","IMPRINT",FACE,{"disambiguationData":[TD([[makeQuery(id+"F0.imprint","IMPRINT",EDGE,{"derivedFrom":sQuery(id+"F0.wireOp",EDGE,"E1640")}),-1.0]])]});
            var Q43;
            Q43=makeQuery(id+"F0.imprint","IMPRINT",FACE,{"disambiguationData":[TD([[makeQuery(id+"F0.imprint","IMPRINT",EDGE,{"derivedFrom":sQuery(id+"F0.wireOp",EDGE,"E1668")}),1.0]])]});
            var Q44;
            Q44=makeQuery(id+"F0.imprint","IMPRINT",FACE,{"disambiguationData":[TD([[makeQuery(id+"F0.imprint","IMPRINT",EDGE,{"derivedFrom":sQuery(id+"F0.wireOp",EDGE,"E1755")}),1.0]])]});
            var Q45;
            Q45=makeQuery(id+"F0.imprint","IMPRINT",FACE,{"disambiguationData":[TD([[makeQuery(id+"F0.imprint","IMPRINT",EDGE,{"derivedFrom":sQuery(id+"F0.wireOp",EDGE,"E1739")}),1.0]])]});
            var Q46;
            Q46=makeQuery(id+"F0.imprint","IMPRINT",FACE,{"disambiguationData":[TD([[makeQuery(id+"F0.imprint","IMPRINT",EDGE,{"derivedFrom":sQuery(id+"F0.wireOp",EDGE,"E1811")}),1.0]])]});
            var Q47;
            Q47=makeQuery(id+"F0.imprint","IMPRINT",FACE,{"disambiguationData":[TD([[makeQuery(id+"F0.imprint","IMPRINT",EDGE,{"derivedFrom":sQuery(id+"F0.wireOp",EDGE,"E1759")}),1.0]])]});
            var Q48;
            Q48=makeQuery(id+"F0.imprint","IMPRINT",FACE,{"disambiguationData":[TD([[makeQuery(id+"F0.imprint","IMPRINT",EDGE,{"derivedFrom":sQuery(id+"F0.wireOp",EDGE,"E1508")}),1.0]])]});
            var Q49;
            Q49=makeQuery(id+"F0.imprint","IMPRINT",FACE,{"disambiguationData":[TD([[makeQuery(id+"F0.imprint","IMPRINT",EDGE,{"derivedFrom":sQuery(id+"F0.wireOp",EDGE,"E1428")}),-1.0]])]});
            var Q50;
            Q50=makeQuery(id+"F0.imprint","IMPRINT",FACE,{"disambiguationData":[TD([[makeQuery(id+"F0.imprint","IMPRINT",EDGE,{"derivedFrom":sQuery(id+"F0.wireOp",EDGE,"E1456")}),1.0]])]});
            var Q51;
            Q51=makeQuery(id+"F0.imprint","IMPRINT",FACE,{"disambiguationData":[TD([[makeQuery(id+"F0.imprint","IMPRINT",EDGE,{"derivedFrom":sQuery(id+"F0.wireOp",EDGE,"E1556")}),1.0]])]});
            var Q52;
            Q52=makeQuery(id+"F0.imprint","IMPRINT",FACE,{"disambiguationData":[TD([[makeQuery(id+"F0.imprint","IMPRINT",EDGE,{"derivedFrom":sQuery(id+"F0.wireOp",EDGE,"E1499")}),1.0]])]});
            var Q53;
            Q53=makeQuery(id+"F0.imprint","IMPRINT",FACE,{"disambiguationData":[TD([[makeQuery(id+"F0.imprint","IMPRINT",EDGE,{"derivedFrom":sQuery(id+"F0.wireOp",EDGE,"E1646")}),1.0]])]});
            var Q54;
            Q54=makeQuery(id+"F0.imprint","IMPRINT",FACE,{"disambiguationData":[TD([[makeQuery(id+"F0.imprint","IMPRINT",EDGE,{"derivedFrom":sQuery(id+"F0.wireOp",EDGE,"E1678")}),1.0]])]});
            var Q55;
            Q55=makeQuery(id+"F0.imprint","IMPRINT",FACE,{"disambiguationData":[TD([[makeQuery(id+"F0.imprint","IMPRINT",EDGE,{"derivedFrom":sQuery(id+"F0.wireOp",EDGE,"E1816")}),1.0]])]});
            var Q56;
            Q56=makeQuery(id+"F0.imprint","IMPRINT",FACE,{"disambiguationData":[TD([[makeQuery(id+"F0.imprint","IMPRINT",EDGE,{"derivedFrom":sQuery(id+"F0.wireOp",EDGE,"E1899")}),-1.0]])]});
            var Q57;
            Q57=makeQuery(id+"F0.imprint","IMPRINT",FACE,{"disambiguationData":[TD([[makeQuery(id+"F0.imprint","IMPRINT",EDGE,{"derivedFrom":sQuery(id+"F0.wireOp",EDGE,"E770")}),1.0]])]});
            var Q58;
            Q58=makeQuery(id+"F0.imprint","IMPRINT",FACE,{"disambiguationData":[TD([[makeQuery(id+"F0.imprint","IMPRINT",EDGE,{"derivedFrom":sQuery(id+"F0.wireOp",EDGE,"E673")}),-1.0]])]});
            var Q59;
            Q59=makeQuery(id+"F0.imprint","IMPRINT",FACE,{"disambiguationData":[TD([[makeQuery(id+"F0.imprint","IMPRINT",EDGE,{"derivedFrom":sQuery(id+"F0.wireOp",EDGE,"E865")}),-1.0]])]});
            var Q60;
            Q60=makeQuery(id+"F0.imprint","IMPRINT",FACE,{"disambiguationData":[TD([[makeQuery(id+"F0.imprint","IMPRINT",EDGE,{"derivedFrom":sQuery(id+"F0.wireOp",EDGE,"E558")}),1.0]])]});
            var Q61;
            Q61=makeQuery(id+"F0.imprint","IMPRINT",FACE,{"disambiguationData":[TD([[makeQuery(id+"F0.imprint","IMPRINT",EDGE,{"derivedFrom":sQuery(id+"F0.wireOp",EDGE,"E497")}),1.0]])]});
            var Q62;
            Q62=makeQuery(id+"F0.imprint","IMPRINT",FACE,{"disambiguationData":[TD([[makeQuery(id+"F0.imprint","IMPRINT",EDGE,{"derivedFrom":sQuery(id+"F0.wireOp",EDGE,"E254")}),1.0]])]});
            var Q63;
            Q63=makeQuery(id+"F0.imprint","IMPRINT",FACE,{"disambiguationData":[TD([[makeQuery(id+"F0.imprint","IMPRINT",EDGE,{"derivedFrom":sQuery(id+"F0.wireOp",EDGE,"E797")}),-1.0]])]});
            var Q64;
            Q64=makeQuery(id+"F0.imprint","IMPRINT",FACE,{"disambiguationData":[TD([[makeQuery(id+"F0.imprint","IMPRINT",EDGE,{"derivedFrom":sQuery(id+"F0.wireOp",EDGE,"E57")}),1.0]])]});
            var Q65;
            Q65=makeQuery(id+"F0.imprint","IMPRINT",FACE,{"disambiguationData":[TD([[makeQuery(id+"F0.imprint","IMPRINT",EDGE,{"derivedFrom":sQuery(id+"F0.wireOp",EDGE,"E1254")}),1.0]])]});
            var Q66;
            Q66=makeQuery(id+"F0.imprint","IMPRINT",FACE,{"disambiguationData":[TD([[makeQuery(id+"F0.imprint","IMPRINT",EDGE,{"derivedFrom":sQuery(id+"F0.wireOp",EDGE,"E1305")}),1.0]])]});
            var Q67;
            Q67=makeQuery(id+"F0.imprint","IMPRINT",FACE,{"disambiguationData":[TD([[makeQuery(id+"F0.imprint","IMPRINT",EDGE,{"derivedFrom":sQuery(id+"F0.wireOp",EDGE,"E1362")}),1.0]])]});
            var Q68;
            Q68=makeQuery(id+"F0.imprint","IMPRINT",FACE,{"disambiguationData":[TD([[makeQuery(id+"F0.imprint","IMPRINT",EDGE,{"derivedFrom":sQuery(id+"F0.wireOp",EDGE,"E1200")}),1.0]])]});
            var Q69;
            Q69=makeQuery(id+"F0.imprint","IMPRINT",FACE,{"disambiguationData":[TD([[makeQuery(id+"F0.imprint","IMPRINT",EDGE,{"derivedFrom":sQuery(id+"F0.wireOp",EDGE,"E2362")}),1.0]])]});
            var Q70;
            Q70=makeQuery(id+"F0.imprint","IMPRINT",FACE,{"disambiguationData":[TD([[makeQuery(id+"F0.imprint","IMPRINT",EDGE,{"derivedFrom":sQuery(id+"F0.wireOp",EDGE,"E2315")}),1.0]])]});
            var Q71;
            Q71=makeQuery(id+"F0.imprint","IMPRINT",FACE,{"disambiguationData":[TD([[makeQuery(id+"F0.imprint","IMPRINT",EDGE,{"derivedFrom":sQuery(id+"F0.wireOp",EDGE,"E2382")}),1.0]])]});
            var Q72;
            Q72=makeQuery(id+"F0.imprint","IMPRINT",FACE,{"disambiguationData":[TD([[makeQuery(id+"F0.imprint","IMPRINT",EDGE,{"derivedFrom":sQuery(id+"F0.wireOp",EDGE,"E2473")}),1.0]])]});
            var Q73;
            Q73=makeQuery(id+"F0.imprint","IMPRINT",FACE,{"disambiguationData":[TD([[makeQuery(id+"F0.imprint","IMPRINT",EDGE,{"derivedFrom":sQuery(id+"F0.wireOp",EDGE,"E2513")}),1.0]])]});
            var Q74;
            Q74=makeQuery(id+"F0.imprint","IMPRINT",FACE,{"disambiguationData":[TD([[makeQuery(id+"F0.imprint","IMPRINT",EDGE,{"derivedFrom":sQuery(id+"F0.wireOp",EDGE,"E2204")}),-1.0]])]});
            var Q75;
            Q75=makeQuery(id+"F0.imprint","IMPRINT",FACE,{"disambiguationData":[TD([[makeQuery(id+"F0.imprint","IMPRINT",EDGE,{"derivedFrom":sQuery(id+"F0.wireOp",EDGE,"E2175")}),-1.0]])]});
            var Q76;
            Q76=makeQuery(id+"F0.imprint","IMPRINT",FACE,{"disambiguationData":[TD([[makeQuery(id+"F0.imprint","IMPRINT",EDGE,{"derivedFrom":sQuery(id+"F0.wireOp",EDGE,"E2164")}),1.0]])]});
            var Q77;
            Q77=makeQuery(id+"F0.imprint","IMPRINT",FACE,{"disambiguationData":[TD([[makeQuery(id+"F0.imprint","IMPRINT",EDGE,{"derivedFrom":sQuery(id+"F0.wireOp",EDGE,"E2099")}),-1.0]])]});
            var Q78;
            Q78=makeQuery(id+"F0.imprint","IMPRINT",FACE,{"disambiguationData":[TD([[makeQuery(id+"F0.imprint","IMPRINT",EDGE,{"derivedFrom":sQuery(id+"F0.wireOp",EDGE,"E2082")}),1.0]])]});
            var Q79;
            Q79=makeQuery(id+"F0.imprint","IMPRINT",FACE,{"disambiguationData":[TD([[makeQuery(id+"F0.imprint","IMPRINT",EDGE,{"derivedFrom":sQuery(id+"F0.wireOp",EDGE,"E2053")}),1.0]])]});
            var Q80;
            Q80=makeQuery(id+"F0.imprint","IMPRINT",FACE,{"disambiguationData":[TD([[makeQuery(id+"F0.imprint","IMPRINT",EDGE,{"derivedFrom":sQuery(id+"F0.wireOp",EDGE,"E2073")}),-1.0]])]});
            extrude(context, id + "F3", {"entities" : qUnion([Q0, Q1, Q2, Q3, Q4, Q5, Q6, Q7, Q8, Q9, Q10, Q11, Q12, Q13, Q14, Q15, Q16, Q17, Q18, Q19, Q20, Q21, Q22, Q23, Q24, Q25, Q26, Q27, Q28, Q29, Q30, Q31, Q32, Q33, Q34, Q35, Q36, Q37, Q38, Q39, Q40, Q41, Q42, Q43, Q44, Q45, Q46, Q47, Q48, Q49, Q50, Q51, Q52, Q53, Q54, Q55, Q56, Q57, Q58, Q59, Q60, Q61, Q62, Q63, Q64, Q65, Q66, Q67, Q68, Q69, Q70, Q71, Q72, Q73, Q74, Q75, Q76, Q77, Q78, Q79, Q80]), "depth" : 1.27 * mm, "hasDraft" : true, "draftAngle" : 5 * degree, "draftPullDirection" : true});
        }
    });
